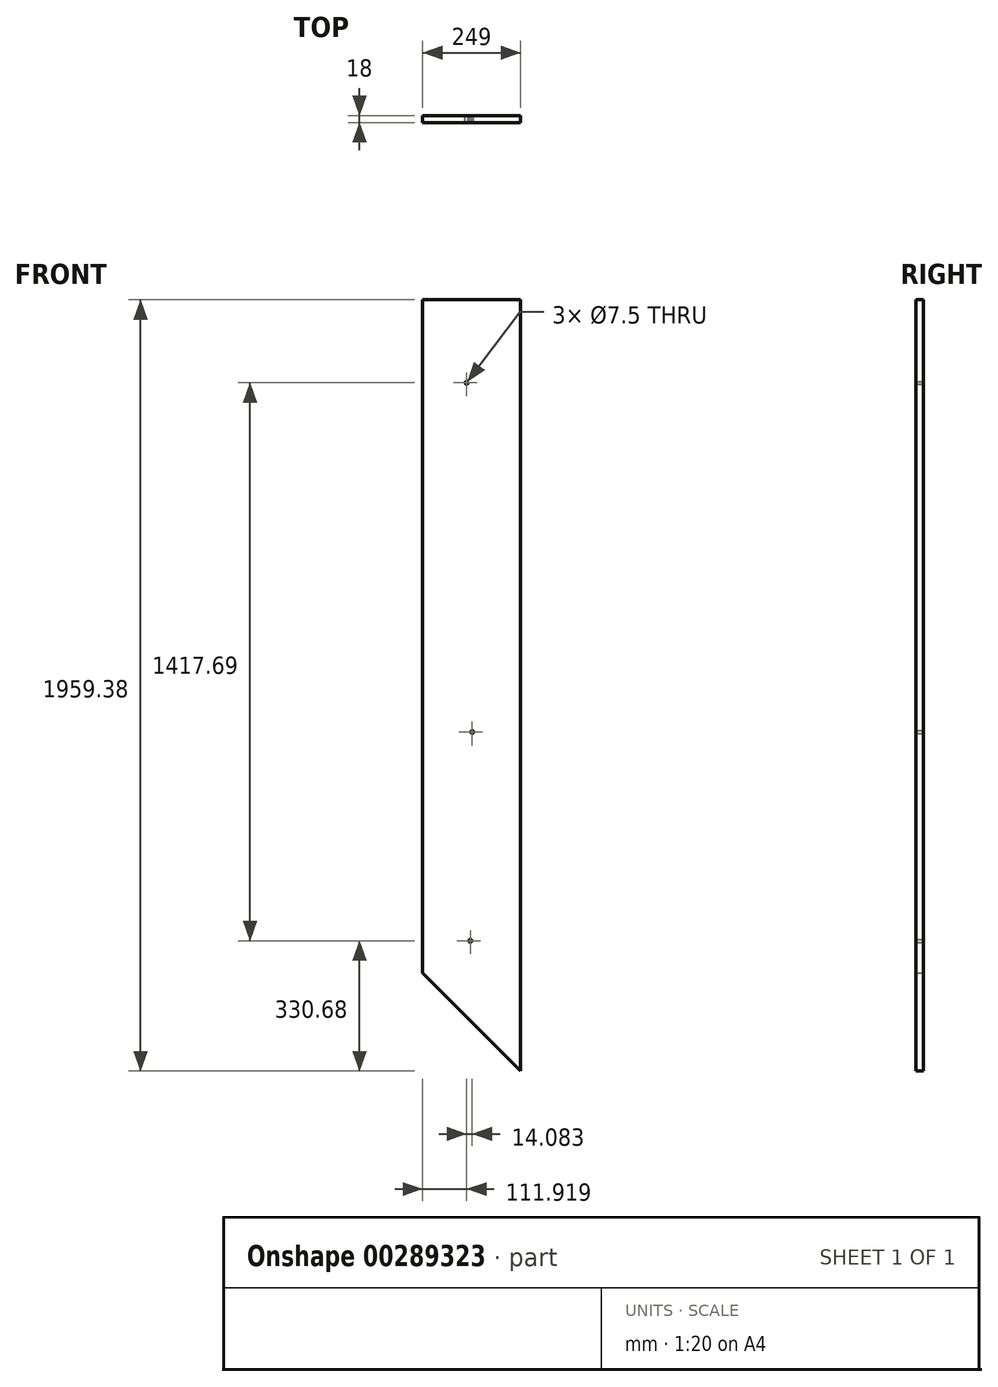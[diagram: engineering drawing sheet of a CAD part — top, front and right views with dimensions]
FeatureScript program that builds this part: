
annotation { "Feature Type Name" : "Feature", "Feature Type Description" : "" }
export const myFeature = defineFeature(function(context is Context, id is Id, definition is map)
    precondition{}
    {
        {
            var Q0;
            Q0=qCreatedBy(makeId("Front.planeOp"),FACE);
            var sketch = newSketch(context, id + "F0", { "sketchPlane" : qUnion([Q0])});
            skLineSegment(sketch, "E0", {"start": v(-600, -1200) * mm, "end": v(600, -1200) * mm});
            skLineSegment(sketch, "E1", {"start": v(600, -1200) * mm, "end": v(600, 1200) * mm});
            skLineSegment(sketch, "E2", {"start": v(600, 1200) * mm, "end": v(-600, 1200) * mm});
            skLineSegment(sketch, "E3", {"start": v(-600, 1200) * mm, "end": v(-600, -1200) * mm});
            skLineSegment(sketch, "E4", {"start": v(-283.65, 1167.87) * mm, "end": v(-532.65, 1167.87) * mm});
            skLineSegment(sketch, "E5", {"start": v(-532.65, 1167.87) * mm, "end": v(-532.65, -542.5) * mm});
            skLineSegment(sketch, "E6", {"start": v(-532.65, -542.5) * mm, "end": v(-283.65, -791.5) * mm});
            skLineSegment(sketch, "E7", {"start": v(-283.65, -791.5) * mm, "end": v(-283.65, 1167.87) * mm});
            skLineSegment(sketch, "E8", {"start": v(276.35, 1167.87) * mm, "end": v(27.35, 1167.87) * mm});
            skLineSegment(sketch, "E9", {"start": v(27.35, 1167.87) * mm, "end": v(27.35, -791.5) * mm});
            skLineSegment(sketch, "E10", {"start": v(27.35, -791.5) * mm, "end": v(276.35, -542.5) * mm});
            skLineSegment(sketch, "E11", {"start": v(276.35, -542.5) * mm, "end": v(276.35, 1167.87) * mm});
            skLineSegment(sketch, "E12", {"start": v(-3.65, 1167.87) * mm, "end": v(-252.65, 1167.87) * mm});
            skLineSegment(sketch, "E13", {"start": v(-252.65, 1167.87) * mm, "end": v(-252.65, -791.5) * mm});
            skLineSegment(sketch, "E14", {"start": v(-252.65, -791.5) * mm, "end": v(-3.65, -542.5) * mm});
            skLineSegment(sketch, "E15", {"start": v(-3.65, -542.5) * mm, "end": v(-3.65, 1167.87) * mm});
            skLineSegment(sketch, "E16", {"start": v(556.35, 1167.87) * mm, "end": v(307.35, 1167.87) * mm});
            skLineSegment(sketch, "E17", {"start": v(307.35, 1167.87) * mm, "end": v(307.35, -542.5) * mm});
            skLineSegment(sketch, "E18", {"start": v(307.35, -542.5) * mm, "end": v(556.35, -791.5) * mm});
            skLineSegment(sketch, "E19", {"start": v(556.35, -791.5) * mm, "end": v(556.35, 1167.87) * mm});
            skLineSegment(sketch, "E20", {"start": v(454.53, 163.58) * mm, "end": v(414.54, 163.58) * mm});
            skLineSegment(sketch, "E21", {"start": v(414.54, 163.58) * mm, "end": v(414.54, 188.44) * mm});
            skLineSegment(sketch, "E22", {"start": v(433.65, 163.58) * mm, "end": v(433.65, 186.65) * mm});
            skLineSegment(sketch, "E23", {"start": v(454.5, 220.74) * mm, "end": v(454.5, 197.24) * mm});
            skLineSegment(sketch, "E24", {"start": v(454.5, 197.24) * mm, "end": v(414.55, 197.24) * mm});
            skLineSegment(sketch, "E25", {"start": v(455.07, 235.9) * mm, "end": v(455.07, 235.48) * mm});
            skLineSegment(sketch, "E26", {"start": v(455.07, 235.48) * mm, "end": v(455.06, 235.06) * mm});
            skLineSegment(sketch, "E27", {"start": v(455.06, 235.06) * mm, "end": v(455.04, 234.64) * mm});
            skLineSegment(sketch, "E28", {"start": v(455.04, 234.64) * mm, "end": v(455.02, 234.22) * mm});
            skLineSegment(sketch, "E29", {"start": v(455.02, 234.22) * mm, "end": v(454.98, 233.8) * mm});
            skLineSegment(sketch, "E30", {"start": v(454.98, 233.8) * mm, "end": v(454.93, 233.4) * mm});
            skLineSegment(sketch, "E31", {"start": v(454.93, 233.4) * mm, "end": v(454.87, 232.98) * mm});
            skLineSegment(sketch, "E32", {"start": v(454.87, 232.98) * mm, "end": v(454.8, 232.58) * mm});
            skLineSegment(sketch, "E33", {"start": v(454.8, 232.58) * mm, "end": v(454.72, 232.17) * mm});
            skLineSegment(sketch, "E34", {"start": v(454.72, 232.17) * mm, "end": v(454.63, 231.76) * mm});
            skLineSegment(sketch, "E35", {"start": v(454.63, 231.76) * mm, "end": v(454.53, 231.36) * mm});
            skLineSegment(sketch, "E36", {"start": v(454.53, 231.36) * mm, "end": v(454.42, 230.96) * mm});
            skLineSegment(sketch, "E37", {"start": v(454.42, 230.96) * mm, "end": v(454.3, 230.56) * mm});
            skLineSegment(sketch, "E38", {"start": v(454.3, 230.56) * mm, "end": v(454.17, 230.17) * mm});
            skLineSegment(sketch, "E39", {"start": v(454.17, 230.17) * mm, "end": v(454.03, 229.78) * mm});
            skLineSegment(sketch, "E40", {"start": v(454.03, 229.78) * mm, "end": v(453.89, 229.4) * mm});
            skLineSegment(sketch, "E41", {"start": v(453.89, 229.4) * mm, "end": v(453.73, 229.01) * mm});
            skLineSegment(sketch, "E42", {"start": v(453.73, 229.01) * mm, "end": v(453.56, 228.64) * mm});
            skLineSegment(sketch, "E43", {"start": v(453.56, 228.64) * mm, "end": v(453.38, 228.26) * mm});
            skLineSegment(sketch, "E44", {"start": v(453.38, 228.26) * mm, "end": v(453.2, 227.9) * mm});
            skLineSegment(sketch, "E45", {"start": v(453.2, 227.9) * mm, "end": v(453, 227.53) * mm});
            skLineSegment(sketch, "E46", {"start": v(453, 227.53) * mm, "end": v(452.8, 227.17) * mm});
            skLineSegment(sketch, "E47", {"start": v(452.8, 227.17) * mm, "end": v(452.58, 226.8) * mm});
            skLineSegment(sketch, "E48", {"start": v(452.58, 226.8) * mm, "end": v(452.36, 226.46) * mm});
            skLineSegment(sketch, "E49", {"start": v(452.36, 226.46) * mm, "end": v(452.13, 226.11) * mm});
            skLineSegment(sketch, "E50", {"start": v(452.13, 226.11) * mm, "end": v(451.9, 225.77) * mm});
            skLineSegment(sketch, "E51", {"start": v(451.9, 225.77) * mm, "end": v(451.64, 225.44) * mm});
            skLineSegment(sketch, "E52", {"start": v(451.64, 225.44) * mm, "end": v(451.39, 225.11) * mm});
            skLineSegment(sketch, "E53", {"start": v(451.39, 225.11) * mm, "end": v(451.12, 224.8) * mm});
            skLineSegment(sketch, "E54", {"start": v(451.12, 224.8) * mm, "end": v(450.85, 224.47) * mm});
            skLineSegment(sketch, "E55", {"start": v(450.85, 224.47) * mm, "end": v(450.56, 224.17) * mm});
            skLineSegment(sketch, "E56", {"start": v(450.56, 224.17) * mm, "end": v(450.27, 223.86) * mm});
            skLineSegment(sketch, "E57", {"start": v(450.27, 223.86) * mm, "end": v(449.9, 223.51) * mm});
            skLineSegment(sketch, "E58", {"start": v(449.9, 223.51) * mm, "end": v(449.5, 223.17) * mm});
            skLineSegment(sketch, "E59", {"start": v(449.5, 223.17) * mm, "end": v(449.1, 222.85) * mm});
            skLineSegment(sketch, "E60", {"start": v(449.1, 222.85) * mm, "end": v(448.7, 222.53) * mm});
            skLineSegment(sketch, "E61", {"start": v(448.7, 222.53) * mm, "end": v(448.3, 222.22) * mm});
            skLineSegment(sketch, "E62", {"start": v(448.3, 222.22) * mm, "end": v(447.88, 221.92) * mm});
            skLineSegment(sketch, "E63", {"start": v(447.88, 221.92) * mm, "end": v(447.45, 221.63) * mm});
            skLineSegment(sketch, "E64", {"start": v(447.45, 221.63) * mm, "end": v(447.02, 221.36) * mm});
            skLineSegment(sketch, "E65", {"start": v(447.02, 221.36) * mm, "end": v(446.58, 221.1) * mm});
            skLineSegment(sketch, "E66", {"start": v(446.58, 221.1) * mm, "end": v(446.14, 220.84) * mm});
            skLineSegment(sketch, "E67", {"start": v(446.14, 220.84) * mm, "end": v(445.7, 220.6) * mm});
            skLineSegment(sketch, "E68", {"start": v(445.7, 220.6) * mm, "end": v(445.24, 220.37) * mm});
            skLineSegment(sketch, "E69", {"start": v(445.24, 220.37) * mm, "end": v(444.78, 220.15) * mm});
            skLineSegment(sketch, "E70", {"start": v(444.78, 220.15) * mm, "end": v(444.31, 219.94) * mm});
            skLineSegment(sketch, "E71", {"start": v(444.31, 219.94) * mm, "end": v(443.84, 219.74) * mm});
            skLineSegment(sketch, "E72", {"start": v(443.84, 219.74) * mm, "end": v(443.37, 219.56) * mm});
            skLineSegment(sketch, "E73", {"start": v(443.37, 219.56) * mm, "end": v(442.89, 219.38) * mm});
            skLineSegment(sketch, "E74", {"start": v(442.89, 219.38) * mm, "end": v(442.4, 219.22) * mm});
            skLineSegment(sketch, "E75", {"start": v(442.4, 219.22) * mm, "end": v(441.92, 219.07) * mm});
            skLineSegment(sketch, "E76", {"start": v(441.92, 219.07) * mm, "end": v(441.43, 218.93) * mm});
            skLineSegment(sketch, "E77", {"start": v(441.43, 218.93) * mm, "end": v(440.94, 218.8) * mm});
            skLineSegment(sketch, "E78", {"start": v(440.94, 218.8) * mm, "end": v(440.44, 218.7) * mm});
            skLineSegment(sketch, "E79", {"start": v(440.44, 218.7) * mm, "end": v(439.94, 218.59) * mm});
            skLineSegment(sketch, "E80", {"start": v(439.94, 218.59) * mm, "end": v(439.44, 218.5) * mm});
            skLineSegment(sketch, "E81", {"start": v(439.44, 218.5) * mm, "end": v(438.93, 218.42) * mm});
            skLineSegment(sketch, "E82", {"start": v(438.93, 218.42) * mm, "end": v(438.42, 218.36) * mm});
            skLineSegment(sketch, "E83", {"start": v(438.42, 218.36) * mm, "end": v(437.91, 218.3) * mm});
            skLineSegment(sketch, "E84", {"start": v(437.91, 218.3) * mm, "end": v(437.4, 218.27) * mm});
            skLineSegment(sketch, "E85", {"start": v(437.4, 218.27) * mm, "end": v(436.89, 218.24) * mm});
            skLineSegment(sketch, "E86", {"start": v(436.89, 218.24) * mm, "end": v(436.37, 218.23) * mm});
            skLineSegment(sketch, "E87", {"start": v(436.37, 218.23) * mm, "end": v(435.86, 218.22) * mm});
            skLineSegment(sketch, "E88", {"start": v(435.86, 218.22) * mm, "end": v(435.34, 218.24) * mm});
            skLineSegment(sketch, "E89", {"start": v(435.34, 218.24) * mm, "end": v(434.78, 218.22) * mm});
            skLineSegment(sketch, "E90", {"start": v(434.78, 218.22) * mm, "end": v(434.22, 218.22) * mm});
            skLineSegment(sketch, "E91", {"start": v(434.22, 218.22) * mm, "end": v(433.66, 218.23) * mm});
            skLineSegment(sketch, "E92", {"start": v(433.66, 218.23) * mm, "end": v(433.1, 218.26) * mm});
            skLineSegment(sketch, "E93", {"start": v(433.1, 218.26) * mm, "end": v(432.55, 218.3) * mm});
            skLineSegment(sketch, "E94", {"start": v(432.55, 218.3) * mm, "end": v(432, 218.35) * mm});
            skLineSegment(sketch, "E95", {"start": v(432, 218.35) * mm, "end": v(431.44, 218.42) * mm});
            skLineSegment(sketch, "E96", {"start": v(431.44, 218.42) * mm, "end": v(430.9, 218.5) * mm});
            skLineSegment(sketch, "E97", {"start": v(430.9, 218.5) * mm, "end": v(430.35, 218.6) * mm});
            skLineSegment(sketch, "E98", {"start": v(430.35, 218.6) * mm, "end": v(429.8, 218.7) * mm});
            skLineSegment(sketch, "E99", {"start": v(429.8, 218.7) * mm, "end": v(429.26, 218.83) * mm});
            skLineSegment(sketch, "E100", {"start": v(429.26, 218.83) * mm, "end": v(428.73, 218.97) * mm});
            skLineSegment(sketch, "E101", {"start": v(428.73, 218.97) * mm, "end": v(428.2, 219.11) * mm});
            skLineSegment(sketch, "E102", {"start": v(428.2, 219.11) * mm, "end": v(427.66, 219.28) * mm});
            skLineSegment(sketch, "E103", {"start": v(427.66, 219.28) * mm, "end": v(427.14, 219.45) * mm});
            skLineSegment(sketch, "E104", {"start": v(427.14, 219.45) * mm, "end": v(426.62, 219.64) * mm});
            skLineSegment(sketch, "E105", {"start": v(426.62, 219.64) * mm, "end": v(426.1, 219.84) * mm});
            skLineSegment(sketch, "E106", {"start": v(426.1, 219.84) * mm, "end": v(425.6, 220.05) * mm});
            skLineSegment(sketch, "E107", {"start": v(425.6, 220.05) * mm, "end": v(425.09, 220.28) * mm});
            skLineSegment(sketch, "E108", {"start": v(425.09, 220.28) * mm, "end": v(424.6, 220.52) * mm});
            skLineSegment(sketch, "E109", {"start": v(424.6, 220.52) * mm, "end": v(424.1, 220.77) * mm});
            skLineSegment(sketch, "E110", {"start": v(424.1, 220.77) * mm, "end": v(423.6, 221.03) * mm});
            skLineSegment(sketch, "E111", {"start": v(423.6, 221.03) * mm, "end": v(423.13, 221.31) * mm});
            skLineSegment(sketch, "E112", {"start": v(423.13, 221.31) * mm, "end": v(422.65, 221.6) * mm});
            skLineSegment(sketch, "E113", {"start": v(422.65, 221.6) * mm, "end": v(422.19, 221.9) * mm});
            skLineSegment(sketch, "E114", {"start": v(422.19, 221.9) * mm, "end": v(421.73, 222.21) * mm});
            skLineSegment(sketch, "E115", {"start": v(421.73, 222.21) * mm, "end": v(421.27, 222.53) * mm});
            skLineSegment(sketch, "E116", {"start": v(421.27, 222.53) * mm, "end": v(420.83, 222.87) * mm});
            skLineSegment(sketch, "E117", {"start": v(420.83, 222.87) * mm, "end": v(420.4, 223.22) * mm});
            skLineSegment(sketch, "E118", {"start": v(420.4, 223.22) * mm, "end": v(419.96, 223.58) * mm});
            skLineSegment(sketch, "E119", {"start": v(419.96, 223.58) * mm, "end": v(419.54, 223.95) * mm});
            skLineSegment(sketch, "E120", {"start": v(419.54, 223.95) * mm, "end": v(419.13, 224.33) * mm});
            skLineSegment(sketch, "E121", {"start": v(419.13, 224.33) * mm, "end": v(418.84, 224.61) * mm});
            skLineSegment(sketch, "E122", {"start": v(418.84, 224.61) * mm, "end": v(418.56, 224.9) * mm});
            skLineSegment(sketch, "E123", {"start": v(418.56, 224.9) * mm, "end": v(418.28, 225.2) * mm});
            skLineSegment(sketch, "E124", {"start": v(418.28, 225.2) * mm, "end": v(418.02, 225.51) * mm});
            skLineSegment(sketch, "E125", {"start": v(418.02, 225.51) * mm, "end": v(417.76, 225.82) * mm});
            skLineSegment(sketch, "E126", {"start": v(417.76, 225.82) * mm, "end": v(417.51, 226.14) * mm});
            skLineSegment(sketch, "E127", {"start": v(417.51, 226.14) * mm, "end": v(417.27, 226.47) * mm});
            skLineSegment(sketch, "E128", {"start": v(417.27, 226.47) * mm, "end": v(417.04, 226.8) * mm});
            skLineSegment(sketch, "E129", {"start": v(417.04, 226.8) * mm, "end": v(416.82, 227.13) * mm});
            skLineSegment(sketch, "E130", {"start": v(416.82, 227.13) * mm, "end": v(416.6, 227.47) * mm});
            skLineSegment(sketch, "E131", {"start": v(416.6, 227.47) * mm, "end": v(416.4, 227.82) * mm});
            skLineSegment(sketch, "E132", {"start": v(416.4, 227.82) * mm, "end": v(416.2, 228.17) * mm});
            skLineSegment(sketch, "E133", {"start": v(416.2, 228.17) * mm, "end": v(416.02, 228.52) * mm});
            skLineSegment(sketch, "E134", {"start": v(416.02, 228.52) * mm, "end": v(415.84, 228.88) * mm});
            skLineSegment(sketch, "E135", {"start": v(415.84, 228.88) * mm, "end": v(415.67, 229.25) * mm});
            skLineSegment(sketch, "E136", {"start": v(415.67, 229.25) * mm, "end": v(415.51, 229.61) * mm});
            skLineSegment(sketch, "E137", {"start": v(415.51, 229.61) * mm, "end": v(415.36, 229.99) * mm});
            skLineSegment(sketch, "E138", {"start": v(415.36, 229.99) * mm, "end": v(415.22, 230.36) * mm});
            skLineSegment(sketch, "E139", {"start": v(415.22, 230.36) * mm, "end": v(415.1, 230.74) * mm});
            skLineSegment(sketch, "E140", {"start": v(415.1, 230.74) * mm, "end": v(414.97, 231.12) * mm});
            skLineSegment(sketch, "E141", {"start": v(414.97, 231.12) * mm, "end": v(414.86, 231.5) * mm});
            skLineSegment(sketch, "E142", {"start": v(414.86, 231.5) * mm, "end": v(414.76, 231.9) * mm});
            skLineSegment(sketch, "E143", {"start": v(414.76, 231.9) * mm, "end": v(414.67, 232.3) * mm});
            skLineSegment(sketch, "E144", {"start": v(414.67, 232.3) * mm, "end": v(414.59, 232.68) * mm});
            skLineSegment(sketch, "E145", {"start": v(414.59, 232.68) * mm, "end": v(414.51, 233.08) * mm});
            skLineSegment(sketch, "E146", {"start": v(414.51, 233.08) * mm, "end": v(414.45, 233.48) * mm});
            skLineSegment(sketch, "E147", {"start": v(414.45, 233.48) * mm, "end": v(414.4, 233.88) * mm});
            skLineSegment(sketch, "E148", {"start": v(414.4, 233.88) * mm, "end": v(414.36, 234.28) * mm});
            skLineSegment(sketch, "E149", {"start": v(414.36, 234.28) * mm, "end": v(414.33, 234.69) * mm});
            skLineSegment(sketch, "E150", {"start": v(414.33, 234.69) * mm, "end": v(414.31, 235.1) * mm});
            skLineSegment(sketch, "E151", {"start": v(414.31, 235.1) * mm, "end": v(414.3, 235.5) * mm});
            skLineSegment(sketch, "E152", {"start": v(414.3, 235.5) * mm, "end": v(414.3, 235.9) * mm});
            skLineSegment(sketch, "E153", {"start": v(414.3, 235.9) * mm, "end": v(414.3, 236.32) * mm});
            skLineSegment(sketch, "E154", {"start": v(414.3, 236.32) * mm, "end": v(414.32, 236.73) * mm});
            skLineSegment(sketch, "E155", {"start": v(414.32, 236.73) * mm, "end": v(414.35, 237.15) * mm});
            skLineSegment(sketch, "E156", {"start": v(414.35, 237.15) * mm, "end": v(414.38, 237.56) * mm});
            skLineSegment(sketch, "E157", {"start": v(414.38, 237.56) * mm, "end": v(414.43, 237.96) * mm});
            skLineSegment(sketch, "E158", {"start": v(414.43, 237.96) * mm, "end": v(414.49, 238.37) * mm});
            skLineSegment(sketch, "E159", {"start": v(414.49, 238.37) * mm, "end": v(414.55, 238.78) * mm});
            skLineSegment(sketch, "E160", {"start": v(414.55, 238.78) * mm, "end": v(414.63, 239.18) * mm});
            skLineSegment(sketch, "E161", {"start": v(414.63, 239.18) * mm, "end": v(414.72, 239.58) * mm});
            skLineSegment(sketch, "E162", {"start": v(414.72, 239.58) * mm, "end": v(414.82, 239.97) * mm});
            skLineSegment(sketch, "E163", {"start": v(414.82, 239.97) * mm, "end": v(414.93, 240.37) * mm});
            skLineSegment(sketch, "E164", {"start": v(414.93, 240.37) * mm, "end": v(415.04, 240.76) * mm});
            skLineSegment(sketch, "E165", {"start": v(415.04, 240.76) * mm, "end": v(415.17, 241.15) * mm});
            skLineSegment(sketch, "E166", {"start": v(415.17, 241.15) * mm, "end": v(415.3, 241.53) * mm});
            skLineSegment(sketch, "E167", {"start": v(415.3, 241.53) * mm, "end": v(415.46, 241.91) * mm});
            skLineSegment(sketch, "E168", {"start": v(415.46, 241.91) * mm, "end": v(415.61, 242.29) * mm});
            skLineSegment(sketch, "E169", {"start": v(415.61, 242.29) * mm, "end": v(415.78, 242.66) * mm});
            skLineSegment(sketch, "E170", {"start": v(415.78, 242.66) * mm, "end": v(415.95, 243.03) * mm});
            skLineSegment(sketch, "E171", {"start": v(415.95, 243.03) * mm, "end": v(416.14, 243.4) * mm});
            skLineSegment(sketch, "E172", {"start": v(416.14, 243.4) * mm, "end": v(416.33, 243.75) * mm});
            skLineSegment(sketch, "E173", {"start": v(416.33, 243.75) * mm, "end": v(416.54, 244.1) * mm});
            skLineSegment(sketch, "E174", {"start": v(416.54, 244.1) * mm, "end": v(416.75, 244.45) * mm});
            skLineSegment(sketch, "E175", {"start": v(416.75, 244.45) * mm, "end": v(416.97, 244.8) * mm});
            skLineSegment(sketch, "E176", {"start": v(416.97, 244.8) * mm, "end": v(417.2, 245.13) * mm});
            skLineSegment(sketch, "E177", {"start": v(417.2, 245.13) * mm, "end": v(417.44, 245.47) * mm});
            skLineSegment(sketch, "E178", {"start": v(417.44, 245.47) * mm, "end": v(417.69, 245.8) * mm});
            skLineSegment(sketch, "E179", {"start": v(417.69, 245.8) * mm, "end": v(417.94, 246.11) * mm});
            skLineSegment(sketch, "E180", {"start": v(417.94, 246.11) * mm, "end": v(418.21, 246.43) * mm});
            skLineSegment(sketch, "E181", {"start": v(418.21, 246.43) * mm, "end": v(418.48, 246.73) * mm});
            skLineSegment(sketch, "E182", {"start": v(418.48, 246.73) * mm, "end": v(418.77, 247.03) * mm});
            skLineSegment(sketch, "E183", {"start": v(418.77, 247.03) * mm, "end": v(419.06, 247.33) * mm});
            skLineSegment(sketch, "E184", {"start": v(419.06, 247.33) * mm, "end": v(419.36, 247.62) * mm});
            skLineSegment(sketch, "E185", {"start": v(419.36, 247.62) * mm, "end": v(419.77, 247.99) * mm});
            skLineSegment(sketch, "E186", {"start": v(419.77, 247.99) * mm, "end": v(420.18, 248.34) * mm});
            skLineSegment(sketch, "E187", {"start": v(420.18, 248.34) * mm, "end": v(420.6, 248.7) * mm});
            skLineSegment(sketch, "E188", {"start": v(420.6, 248.7) * mm, "end": v(421.04, 249.03) * mm});
            skLineSegment(sketch, "E189", {"start": v(421.04, 249.03) * mm, "end": v(421.49, 249.35) * mm});
            skLineSegment(sketch, "E190", {"start": v(421.49, 249.35) * mm, "end": v(421.93, 249.67) * mm});
            skLineSegment(sketch, "E191", {"start": v(421.93, 249.67) * mm, "end": v(422.39, 249.97) * mm});
            skLineSegment(sketch, "E192", {"start": v(422.39, 249.97) * mm, "end": v(422.85, 250.26) * mm});
            skLineSegment(sketch, "E193", {"start": v(422.85, 250.26) * mm, "end": v(423.32, 250.54) * mm});
            skLineSegment(sketch, "E194", {"start": v(423.32, 250.54) * mm, "end": v(423.8, 250.8) * mm});
            skLineSegment(sketch, "E195", {"start": v(423.8, 250.8) * mm, "end": v(424.28, 251.06) * mm});
            skLineSegment(sketch, "E196", {"start": v(424.28, 251.06) * mm, "end": v(424.77, 251.3) * mm});
            skLineSegment(sketch, "E197", {"start": v(424.77, 251.3) * mm, "end": v(425.26, 251.53) * mm});
            skLineSegment(sketch, "E198", {"start": v(425.26, 251.53) * mm, "end": v(425.76, 251.75) * mm});
            skLineSegment(sketch, "E199", {"start": v(425.76, 251.75) * mm, "end": v(426.26, 251.95) * mm});
            skLineSegment(sketch, "E200", {"start": v(426.26, 251.95) * mm, "end": v(426.77, 252.14) * mm});
            skLineSegment(sketch, "E201", {"start": v(426.77, 252.14) * mm, "end": v(427.29, 252.32) * mm});
            skLineSegment(sketch, "E202", {"start": v(427.29, 252.32) * mm, "end": v(427.8, 252.5) * mm});
            skLineSegment(sketch, "E203", {"start": v(427.8, 252.5) * mm, "end": v(428.33, 252.64) * mm});
            skLineSegment(sketch, "E204", {"start": v(428.33, 252.64) * mm, "end": v(428.85, 252.79) * mm});
            skLineSegment(sketch, "E205", {"start": v(428.85, 252.79) * mm, "end": v(429.38, 252.91) * mm});
            skLineSegment(sketch, "E206", {"start": v(429.38, 252.91) * mm, "end": v(429.91, 253.03) * mm});
            skLineSegment(sketch, "E207", {"start": v(429.91, 253.03) * mm, "end": v(430.45, 253.13) * mm});
            skLineSegment(sketch, "E208", {"start": v(430.45, 253.13) * mm, "end": v(430.99, 253.22) * mm});
            skLineSegment(sketch, "E209", {"start": v(430.99, 253.22) * mm, "end": v(431.53, 253.3) * mm});
            skLineSegment(sketch, "E210", {"start": v(431.53, 253.3) * mm, "end": v(432.07, 253.36) * mm});
            skLineSegment(sketch, "E211", {"start": v(432.07, 253.36) * mm, "end": v(432.62, 253.41) * mm});
            skLineSegment(sketch, "E212", {"start": v(432.62, 253.41) * mm, "end": v(433.16, 253.45) * mm});
            skLineSegment(sketch, "E213", {"start": v(433.16, 253.45) * mm, "end": v(433.71, 253.47) * mm});
            skLineSegment(sketch, "E214", {"start": v(433.71, 253.47) * mm, "end": v(434.26, 253.48) * mm});
            skLineSegment(sketch, "E215", {"start": v(434.26, 253.48) * mm, "end": v(434.81, 253.47) * mm});
            skLineSegment(sketch, "E216", {"start": v(434.81, 253.47) * mm, "end": v(435.36, 253.45) * mm});
            skLineSegment(sketch, "E217", {"start": v(435.36, 253.45) * mm, "end": v(435.88, 253.46) * mm});
            skLineSegment(sketch, "E218", {"start": v(435.88, 253.46) * mm, "end": v(436.4, 253.45) * mm});
            skLineSegment(sketch, "E219", {"start": v(436.4, 253.45) * mm, "end": v(436.9, 253.44) * mm});
            skLineSegment(sketch, "E220", {"start": v(436.9, 253.44) * mm, "end": v(437.42, 253.4) * mm});
            skLineSegment(sketch, "E221", {"start": v(437.42, 253.4) * mm, "end": v(437.93, 253.36) * mm});
            skLineSegment(sketch, "E222", {"start": v(437.93, 253.36) * mm, "end": v(438.43, 253.3) * mm});
            skLineSegment(sketch, "E223", {"start": v(438.43, 253.3) * mm, "end": v(438.94, 253.24) * mm});
            skLineSegment(sketch, "E224", {"start": v(438.94, 253.24) * mm, "end": v(439.44, 253.16) * mm});
            skLineSegment(sketch, "E225", {"start": v(439.44, 253.16) * mm, "end": v(439.94, 253.06) * mm});
            skLineSegment(sketch, "E226", {"start": v(439.94, 253.06) * mm, "end": v(440.44, 252.96) * mm});
            skLineSegment(sketch, "E227", {"start": v(440.44, 252.96) * mm, "end": v(440.93, 252.84) * mm});
            skLineSegment(sketch, "E228", {"start": v(440.93, 252.84) * mm, "end": v(441.42, 252.7) * mm});
            skLineSegment(sketch, "E229", {"start": v(441.42, 252.7) * mm, "end": v(441.91, 252.57) * mm});
            skLineSegment(sketch, "E230", {"start": v(441.91, 252.57) * mm, "end": v(442.4, 252.41) * mm});
            skLineSegment(sketch, "E231", {"start": v(442.4, 252.41) * mm, "end": v(442.87, 252.24) * mm});
            skLineSegment(sketch, "E232", {"start": v(442.87, 252.24) * mm, "end": v(443.35, 252.07) * mm});
            skLineSegment(sketch, "E233", {"start": v(443.35, 252.07) * mm, "end": v(443.82, 251.88) * mm});
            skLineSegment(sketch, "E234", {"start": v(443.82, 251.88) * mm, "end": v(444.28, 251.68) * mm});
            skLineSegment(sketch, "E235", {"start": v(444.28, 251.68) * mm, "end": v(444.74, 251.46) * mm});
            skLineSegment(sketch, "E236", {"start": v(444.74, 251.46) * mm, "end": v(445.2, 251.24) * mm});
            skLineSegment(sketch, "E237", {"start": v(445.2, 251.24) * mm, "end": v(445.65, 251) * mm});
            skLineSegment(sketch, "E238", {"start": v(445.65, 251) * mm, "end": v(446.1, 250.76) * mm});
            skLineSegment(sketch, "E239", {"start": v(446.1, 250.76) * mm, "end": v(446.53, 250.5) * mm});
            skLineSegment(sketch, "E240", {"start": v(446.53, 250.5) * mm, "end": v(446.96, 250.23) * mm});
            skLineSegment(sketch, "E241", {"start": v(446.96, 250.23) * mm, "end": v(447.39, 249.95) * mm});
            skLineSegment(sketch, "E242", {"start": v(447.39, 249.95) * mm, "end": v(447.8, 249.66) * mm});
            skLineSegment(sketch, "E243", {"start": v(447.8, 249.66) * mm, "end": v(448.22, 249.36) * mm});
            skLineSegment(sketch, "E244", {"start": v(448.22, 249.36) * mm, "end": v(448.62, 249.04) * mm});
            skLineSegment(sketch, "E245", {"start": v(448.62, 249.04) * mm, "end": v(449.02, 248.72) * mm});
            skLineSegment(sketch, "E246", {"start": v(449.02, 248.72) * mm, "end": v(449.41, 248.39) * mm});
            skLineSegment(sketch, "E247", {"start": v(449.41, 248.39) * mm, "end": v(449.8, 248.04) * mm});
            skLineSegment(sketch, "E248", {"start": v(449.8, 248.04) * mm, "end": v(450.17, 247.69) * mm});
            skLineSegment(sketch, "E249", {"start": v(450.17, 247.69) * mm, "end": v(450.46, 247.4) * mm});
            skLineSegment(sketch, "E250", {"start": v(450.46, 247.4) * mm, "end": v(450.74, 247.1) * mm});
            skLineSegment(sketch, "E251", {"start": v(450.74, 247.1) * mm, "end": v(451.02, 246.79) * mm});
            skLineSegment(sketch, "E252", {"start": v(451.02, 246.79) * mm, "end": v(451.28, 246.47) * mm});
            skLineSegment(sketch, "E253", {"start": v(451.28, 246.47) * mm, "end": v(451.54, 246.15) * mm});
            skLineSegment(sketch, "E254", {"start": v(451.54, 246.15) * mm, "end": v(451.8, 245.83) * mm});
            skLineSegment(sketch, "E255", {"start": v(451.8, 245.83) * mm, "end": v(452.03, 245.5) * mm});
            skLineSegment(sketch, "E256", {"start": v(452.03, 245.5) * mm, "end": v(452.26, 245.16) * mm});
            skLineSegment(sketch, "E257", {"start": v(452.26, 245.16) * mm, "end": v(452.49, 244.82) * mm});
            skLineSegment(sketch, "E258", {"start": v(452.49, 244.82) * mm, "end": v(452.7, 244.47) * mm});
            skLineSegment(sketch, "E259", {"start": v(452.7, 244.47) * mm, "end": v(452.91, 244.12) * mm});
            skLineSegment(sketch, "E260", {"start": v(452.91, 244.12) * mm, "end": v(453.1, 243.76) * mm});
            skLineSegment(sketch, "E261", {"start": v(453.1, 243.76) * mm, "end": v(453.3, 243.4) * mm});
            skLineSegment(sketch, "E262", {"start": v(453.3, 243.4) * mm, "end": v(453.48, 243.03) * mm});
            skLineSegment(sketch, "E263", {"start": v(453.48, 243.03) * mm, "end": v(453.65, 242.66) * mm});
            skLineSegment(sketch, "E264", {"start": v(453.65, 242.66) * mm, "end": v(453.8, 242.29) * mm});
            skLineSegment(sketch, "E265", {"start": v(453.8, 242.29) * mm, "end": v(453.96, 241.9) * mm});
            skLineSegment(sketch, "E266", {"start": v(453.96, 241.9) * mm, "end": v(454.1, 241.53) * mm});
            skLineSegment(sketch, "E267", {"start": v(454.1, 241.53) * mm, "end": v(454.23, 241.14) * mm});
            skLineSegment(sketch, "E268", {"start": v(454.23, 241.14) * mm, "end": v(454.36, 240.75) * mm});
            skLineSegment(sketch, "E269", {"start": v(454.36, 240.75) * mm, "end": v(454.47, 240.36) * mm});
            skLineSegment(sketch, "E270", {"start": v(454.47, 240.36) * mm, "end": v(454.58, 239.97) * mm});
            skLineSegment(sketch, "E271", {"start": v(454.58, 239.97) * mm, "end": v(454.67, 239.57) * mm});
            skLineSegment(sketch, "E272", {"start": v(454.67, 239.57) * mm, "end": v(454.75, 239.17) * mm});
            skLineSegment(sketch, "E273", {"start": v(454.75, 239.17) * mm, "end": v(454.83, 238.77) * mm});
            skLineSegment(sketch, "E274", {"start": v(454.83, 238.77) * mm, "end": v(454.9, 238.36) * mm});
            skLineSegment(sketch, "E275", {"start": v(454.9, 238.36) * mm, "end": v(454.95, 237.95) * mm});
            skLineSegment(sketch, "E276", {"start": v(454.95, 237.95) * mm, "end": v(455, 237.55) * mm});
            skLineSegment(sketch, "E277", {"start": v(455, 237.55) * mm, "end": v(455.03, 237.14) * mm});
            skLineSegment(sketch, "E278", {"start": v(455.03, 237.14) * mm, "end": v(455.05, 236.72) * mm});
            skLineSegment(sketch, "E279", {"start": v(455.05, 236.72) * mm, "end": v(455.06, 236.31) * mm});
            skLineSegment(sketch, "E280", {"start": v(455.06, 236.31) * mm, "end": v(455.07, 235.9) * mm});
            skLineSegment(sketch, "E281", {"start": v(455.07, 280.14) * mm, "end": v(455.07, 279.72) * mm});
            skLineSegment(sketch, "E282", {"start": v(455.07, 279.72) * mm, "end": v(455.06, 279.3) * mm});
            skLineSegment(sketch, "E283", {"start": v(455.06, 279.3) * mm, "end": v(455.04, 278.89) * mm});
            skLineSegment(sketch, "E284", {"start": v(455.04, 278.89) * mm, "end": v(455.02, 278.47) * mm});
            skLineSegment(sketch, "E285", {"start": v(455.02, 278.47) * mm, "end": v(454.98, 278.06) * mm});
            skLineSegment(sketch, "E286", {"start": v(454.98, 278.06) * mm, "end": v(454.93, 277.64) * mm});
            skLineSegment(sketch, "E287", {"start": v(454.93, 277.64) * mm, "end": v(454.87, 277.23) * mm});
            skLineSegment(sketch, "E288", {"start": v(454.87, 277.23) * mm, "end": v(454.8, 276.82) * mm});
            skLineSegment(sketch, "E289", {"start": v(454.8, 276.82) * mm, "end": v(454.72, 276.41) * mm});
            skLineSegment(sketch, "E290", {"start": v(454.72, 276.41) * mm, "end": v(454.63, 276) * mm});
            skLineSegment(sketch, "E291", {"start": v(454.63, 276) * mm, "end": v(454.53, 275.6) * mm});
            skLineSegment(sketch, "E292", {"start": v(454.53, 275.6) * mm, "end": v(454.42, 275.2) * mm});
            skLineSegment(sketch, "E293", {"start": v(454.42, 275.2) * mm, "end": v(454.3, 274.81) * mm});
            skLineSegment(sketch, "E294", {"start": v(454.3, 274.81) * mm, "end": v(454.17, 274.42) * mm});
            skLineSegment(sketch, "E295", {"start": v(454.17, 274.42) * mm, "end": v(454.03, 274.03) * mm});
            skLineSegment(sketch, "E296", {"start": v(454.03, 274.03) * mm, "end": v(453.89, 273.64) * mm});
            skLineSegment(sketch, "E297", {"start": v(453.89, 273.64) * mm, "end": v(453.73, 273.26) * mm});
            skLineSegment(sketch, "E298", {"start": v(453.73, 273.26) * mm, "end": v(453.56, 272.88) * mm});
            skLineSegment(sketch, "E299", {"start": v(453.56, 272.88) * mm, "end": v(453.38, 272.5) * mm});
            skLineSegment(sketch, "E300", {"start": v(453.38, 272.5) * mm, "end": v(453.2, 272.14) * mm});
            skLineSegment(sketch, "E301", {"start": v(453.2, 272.14) * mm, "end": v(453, 271.77) * mm});
            skLineSegment(sketch, "E302", {"start": v(453, 271.77) * mm, "end": v(452.8, 271.41) * mm});
            skLineSegment(sketch, "E303", {"start": v(452.8, 271.41) * mm, "end": v(452.58, 271.05) * mm});
            skLineSegment(sketch, "E304", {"start": v(452.58, 271.05) * mm, "end": v(452.36, 270.7) * mm});
            skLineSegment(sketch, "E305", {"start": v(452.36, 270.7) * mm, "end": v(452.13, 270.36) * mm});
            skLineSegment(sketch, "E306", {"start": v(452.13, 270.36) * mm, "end": v(451.9, 270.02) * mm});
            skLineSegment(sketch, "E307", {"start": v(451.9, 270.02) * mm, "end": v(451.64, 269.69) * mm});
            skLineSegment(sketch, "E308", {"start": v(451.64, 269.69) * mm, "end": v(451.39, 269.36) * mm});
            skLineSegment(sketch, "E309", {"start": v(451.39, 269.36) * mm, "end": v(451.12, 269.04) * mm});
            skLineSegment(sketch, "E310", {"start": v(451.12, 269.04) * mm, "end": v(450.85, 268.72) * mm});
            skLineSegment(sketch, "E311", {"start": v(450.85, 268.72) * mm, "end": v(450.56, 268.41) * mm});
            skLineSegment(sketch, "E312", {"start": v(450.56, 268.41) * mm, "end": v(450.27, 268.1) * mm});
            skLineSegment(sketch, "E313", {"start": v(450.27, 268.1) * mm, "end": v(449.9, 267.76) * mm});
            skLineSegment(sketch, "E314", {"start": v(449.9, 267.76) * mm, "end": v(449.5, 267.42) * mm});
            skLineSegment(sketch, "E315", {"start": v(449.5, 267.42) * mm, "end": v(449.1, 267.1) * mm});
            skLineSegment(sketch, "E316", {"start": v(449.1, 267.1) * mm, "end": v(448.7, 266.77) * mm});
            skLineSegment(sketch, "E317", {"start": v(448.7, 266.77) * mm, "end": v(448.3, 266.46) * mm});
            skLineSegment(sketch, "E318", {"start": v(448.3, 266.46) * mm, "end": v(447.88, 266.17) * mm});
            skLineSegment(sketch, "E319", {"start": v(447.88, 266.17) * mm, "end": v(447.45, 265.88) * mm});
            skLineSegment(sketch, "E320", {"start": v(447.45, 265.88) * mm, "end": v(447.02, 265.6) * mm});
            skLineSegment(sketch, "E321", {"start": v(447.02, 265.6) * mm, "end": v(446.58, 265.34) * mm});
            skLineSegment(sketch, "E322", {"start": v(446.58, 265.34) * mm, "end": v(446.14, 265.09) * mm});
            skLineSegment(sketch, "E323", {"start": v(446.14, 265.09) * mm, "end": v(445.7, 264.84) * mm});
            skLineSegment(sketch, "E324", {"start": v(445.7, 264.84) * mm, "end": v(445.24, 264.61) * mm});
            skLineSegment(sketch, "E325", {"start": v(445.24, 264.61) * mm, "end": v(444.78, 264.4) * mm});
            skLineSegment(sketch, "E326", {"start": v(444.78, 264.4) * mm, "end": v(444.31, 264.18) * mm});
            skLineSegment(sketch, "E327", {"start": v(444.31, 264.18) * mm, "end": v(443.84, 263.99) * mm});
            skLineSegment(sketch, "E328", {"start": v(443.84, 263.99) * mm, "end": v(443.37, 263.8) * mm});
            skLineSegment(sketch, "E329", {"start": v(443.37, 263.8) * mm, "end": v(442.89, 263.63) * mm});
            skLineSegment(sketch, "E330", {"start": v(442.89, 263.63) * mm, "end": v(442.4, 263.47) * mm});
            skLineSegment(sketch, "E331", {"start": v(442.4, 263.47) * mm, "end": v(441.92, 263.32) * mm});
            skLineSegment(sketch, "E332", {"start": v(441.92, 263.32) * mm, "end": v(441.43, 263.18) * mm});
            skLineSegment(sketch, "E333", {"start": v(441.43, 263.18) * mm, "end": v(440.94, 263.05) * mm});
            skLineSegment(sketch, "E334", {"start": v(440.94, 263.05) * mm, "end": v(440.44, 262.94) * mm});
            skLineSegment(sketch, "E335", {"start": v(440.44, 262.94) * mm, "end": v(439.94, 262.84) * mm});
            skLineSegment(sketch, "E336", {"start": v(439.94, 262.84) * mm, "end": v(439.44, 262.75) * mm});
            skLineSegment(sketch, "E337", {"start": v(439.44, 262.75) * mm, "end": v(438.93, 262.67) * mm});
            skLineSegment(sketch, "E338", {"start": v(438.93, 262.67) * mm, "end": v(438.42, 262.6) * mm});
            skLineSegment(sketch, "E339", {"start": v(438.42, 262.6) * mm, "end": v(437.91, 262.55) * mm});
            skLineSegment(sketch, "E340", {"start": v(437.91, 262.55) * mm, "end": v(437.4, 262.51) * mm});
            skLineSegment(sketch, "E341", {"start": v(437.4, 262.51) * mm, "end": v(436.89, 262.49) * mm});
            skLineSegment(sketch, "E342", {"start": v(436.89, 262.49) * mm, "end": v(436.37, 262.47) * mm});
            skLineSegment(sketch, "E343", {"start": v(436.37, 262.47) * mm, "end": v(435.86, 262.47) * mm});
            skLineSegment(sketch, "E344", {"start": v(435.86, 262.47) * mm, "end": v(435.34, 262.48) * mm});
            skLineSegment(sketch, "E345", {"start": v(435.34, 262.48) * mm, "end": v(434.78, 262.47) * mm});
            skLineSegment(sketch, "E346", {"start": v(434.78, 262.47) * mm, "end": v(434.22, 262.46) * mm});
            skLineSegment(sketch, "E347", {"start": v(434.22, 262.46) * mm, "end": v(433.66, 262.48) * mm});
            skLineSegment(sketch, "E348", {"start": v(433.66, 262.48) * mm, "end": v(433.1, 262.5) * mm});
            skLineSegment(sketch, "E349", {"start": v(433.1, 262.5) * mm, "end": v(432.55, 262.54) * mm});
            skLineSegment(sketch, "E350", {"start": v(432.55, 262.54) * mm, "end": v(432, 262.6) * mm});
            skLineSegment(sketch, "E351", {"start": v(432, 262.6) * mm, "end": v(431.44, 262.67) * mm});
            skLineSegment(sketch, "E352", {"start": v(431.44, 262.67) * mm, "end": v(430.9, 262.75) * mm});
            skLineSegment(sketch, "E353", {"start": v(430.9, 262.75) * mm, "end": v(430.35, 262.84) * mm});
            skLineSegment(sketch, "E354", {"start": v(430.35, 262.84) * mm, "end": v(429.8, 262.95) * mm});
            skLineSegment(sketch, "E355", {"start": v(429.8, 262.95) * mm, "end": v(429.26, 263.08) * mm});
            skLineSegment(sketch, "E356", {"start": v(429.26, 263.08) * mm, "end": v(428.73, 263.21) * mm});
            skLineSegment(sketch, "E357", {"start": v(428.73, 263.21) * mm, "end": v(428.2, 263.36) * mm});
            skLineSegment(sketch, "E358", {"start": v(428.2, 263.36) * mm, "end": v(427.66, 263.52) * mm});
            skLineSegment(sketch, "E359", {"start": v(427.66, 263.52) * mm, "end": v(427.14, 263.7) * mm});
            skLineSegment(sketch, "E360", {"start": v(427.14, 263.7) * mm, "end": v(426.62, 263.89) * mm});
            skLineSegment(sketch, "E361", {"start": v(426.62, 263.89) * mm, "end": v(426.1, 264.09) * mm});
            skLineSegment(sketch, "E362", {"start": v(426.1, 264.09) * mm, "end": v(425.6, 264.3) * mm});
            skLineSegment(sketch, "E363", {"start": v(425.6, 264.3) * mm, "end": v(425.09, 264.53) * mm});
            skLineSegment(sketch, "E364", {"start": v(425.09, 264.53) * mm, "end": v(424.6, 264.77) * mm});
            skLineSegment(sketch, "E365", {"start": v(424.6, 264.77) * mm, "end": v(424.1, 265.02) * mm});
            skLineSegment(sketch, "E366", {"start": v(424.1, 265.02) * mm, "end": v(423.6, 265.28) * mm});
            skLineSegment(sketch, "E367", {"start": v(423.6, 265.28) * mm, "end": v(423.13, 265.56) * mm});
            skLineSegment(sketch, "E368", {"start": v(423.13, 265.56) * mm, "end": v(422.65, 265.84) * mm});
            skLineSegment(sketch, "E369", {"start": v(422.65, 265.84) * mm, "end": v(422.19, 266.14) * mm});
            skLineSegment(sketch, "E370", {"start": v(422.19, 266.14) * mm, "end": v(421.73, 266.46) * mm});
            skLineSegment(sketch, "E371", {"start": v(421.73, 266.46) * mm, "end": v(421.27, 266.78) * mm});
            skLineSegment(sketch, "E372", {"start": v(421.27, 266.78) * mm, "end": v(420.83, 267.11) * mm});
            skLineSegment(sketch, "E373", {"start": v(420.83, 267.11) * mm, "end": v(420.4, 267.46) * mm});
            skLineSegment(sketch, "E374", {"start": v(420.4, 267.46) * mm, "end": v(419.96, 267.82) * mm});
            skLineSegment(sketch, "E375", {"start": v(419.96, 267.82) * mm, "end": v(419.54, 268.2) * mm});
            skLineSegment(sketch, "E376", {"start": v(419.54, 268.2) * mm, "end": v(419.13, 268.57) * mm});
            skLineSegment(sketch, "E377", {"start": v(419.13, 268.57) * mm, "end": v(418.84, 268.86) * mm});
            skLineSegment(sketch, "E378", {"start": v(418.84, 268.86) * mm, "end": v(418.56, 269.15) * mm});
            skLineSegment(sketch, "E379", {"start": v(418.56, 269.15) * mm, "end": v(418.28, 269.45) * mm});
            skLineSegment(sketch, "E380", {"start": v(418.28, 269.45) * mm, "end": v(418.02, 269.76) * mm});
            skLineSegment(sketch, "E381", {"start": v(418.02, 269.76) * mm, "end": v(417.76, 270.07) * mm});
            skLineSegment(sketch, "E382", {"start": v(417.76, 270.07) * mm, "end": v(417.51, 270.39) * mm});
            skLineSegment(sketch, "E383", {"start": v(417.51, 270.39) * mm, "end": v(417.27, 270.71) * mm});
            skLineSegment(sketch, "E384", {"start": v(417.27, 270.71) * mm, "end": v(417.04, 271.04) * mm});
            skLineSegment(sketch, "E385", {"start": v(417.04, 271.04) * mm, "end": v(416.82, 271.38) * mm});
            skLineSegment(sketch, "E386", {"start": v(416.82, 271.38) * mm, "end": v(416.6, 271.72) * mm});
            skLineSegment(sketch, "E387", {"start": v(416.6, 271.72) * mm, "end": v(416.4, 272.06) * mm});
            skLineSegment(sketch, "E388", {"start": v(416.4, 272.06) * mm, "end": v(416.2, 272.41) * mm});
            skLineSegment(sketch, "E389", {"start": v(416.2, 272.41) * mm, "end": v(416.02, 272.77) * mm});
            skLineSegment(sketch, "E390", {"start": v(416.02, 272.77) * mm, "end": v(415.84, 273.13) * mm});
            skLineSegment(sketch, "E391", {"start": v(415.84, 273.13) * mm, "end": v(415.67, 273.5) * mm});
            skLineSegment(sketch, "E392", {"start": v(415.67, 273.5) * mm, "end": v(415.51, 273.86) * mm});
            skLineSegment(sketch, "E393", {"start": v(415.51, 273.86) * mm, "end": v(415.36, 274.23) * mm});
            skLineSegment(sketch, "E394", {"start": v(415.36, 274.23) * mm, "end": v(415.22, 274.6) * mm});
            skLineSegment(sketch, "E395", {"start": v(415.22, 274.6) * mm, "end": v(415.1, 274.99) * mm});
            skLineSegment(sketch, "E396", {"start": v(415.1, 274.99) * mm, "end": v(414.97, 275.37) * mm});
            skLineSegment(sketch, "E397", {"start": v(414.97, 275.37) * mm, "end": v(414.86, 275.76) * mm});
            skLineSegment(sketch, "E398", {"start": v(414.86, 275.76) * mm, "end": v(414.76, 276.14) * mm});
            skLineSegment(sketch, "E399", {"start": v(414.76, 276.14) * mm, "end": v(414.67, 276.54) * mm});
            skLineSegment(sketch, "E400", {"start": v(414.67, 276.54) * mm, "end": v(414.59, 276.93) * mm});
            skLineSegment(sketch, "E401", {"start": v(414.59, 276.93) * mm, "end": v(414.51, 277.33) * mm});
            skLineSegment(sketch, "E402", {"start": v(414.51, 277.33) * mm, "end": v(414.45, 277.72) * mm});
            skLineSegment(sketch, "E403", {"start": v(414.45, 277.72) * mm, "end": v(414.4, 278.13) * mm});
            skLineSegment(sketch, "E404", {"start": v(414.4, 278.13) * mm, "end": v(414.36, 278.53) * mm});
            skLineSegment(sketch, "E405", {"start": v(414.36, 278.53) * mm, "end": v(414.33, 278.93) * mm});
            skLineSegment(sketch, "E406", {"start": v(414.33, 278.93) * mm, "end": v(414.31, 279.34) * mm});
            skLineSegment(sketch, "E407", {"start": v(414.31, 279.34) * mm, "end": v(414.3, 279.74) * mm});
            skLineSegment(sketch, "E408", {"start": v(414.3, 279.74) * mm, "end": v(414.3, 280.15) * mm});
            skLineSegment(sketch, "E409", {"start": v(414.3, 280.15) * mm, "end": v(414.3, 280.57) * mm});
            skLineSegment(sketch, "E410", {"start": v(414.3, 280.57) * mm, "end": v(414.32, 280.98) * mm});
            skLineSegment(sketch, "E411", {"start": v(414.32, 280.98) * mm, "end": v(414.35, 281.4) * mm});
            skLineSegment(sketch, "E412", {"start": v(414.35, 281.4) * mm, "end": v(414.38, 281.8) * mm});
            skLineSegment(sketch, "E413", {"start": v(414.38, 281.8) * mm, "end": v(414.43, 282.2) * mm});
            skLineSegment(sketch, "E414", {"start": v(414.43, 282.2) * mm, "end": v(414.49, 282.62) * mm});
            skLineSegment(sketch, "E415", {"start": v(414.49, 282.62) * mm, "end": v(414.55, 283.02) * mm});
            skLineSegment(sketch, "E416", {"start": v(414.55, 283.02) * mm, "end": v(414.63, 283.42) * mm});
            skLineSegment(sketch, "E417", {"start": v(414.63, 283.42) * mm, "end": v(414.72, 283.82) * mm});
            skLineSegment(sketch, "E418", {"start": v(414.72, 283.82) * mm, "end": v(414.82, 284.22) * mm});
            skLineSegment(sketch, "E419", {"start": v(414.82, 284.22) * mm, "end": v(414.93, 284.61) * mm});
            skLineSegment(sketch, "E420", {"start": v(414.93, 284.61) * mm, "end": v(415.04, 285) * mm});
            skLineSegment(sketch, "E421", {"start": v(415.04, 285) * mm, "end": v(415.17, 285.4) * mm});
            skLineSegment(sketch, "E422", {"start": v(415.17, 285.4) * mm, "end": v(415.3, 285.78) * mm});
            skLineSegment(sketch, "E423", {"start": v(415.3, 285.78) * mm, "end": v(415.46, 286.16) * mm});
            skLineSegment(sketch, "E424", {"start": v(415.46, 286.16) * mm, "end": v(415.61, 286.53) * mm});
            skLineSegment(sketch, "E425", {"start": v(415.61, 286.53) * mm, "end": v(415.78, 286.9) * mm});
            skLineSegment(sketch, "E426", {"start": v(415.78, 286.9) * mm, "end": v(415.95, 287.27) * mm});
            skLineSegment(sketch, "E427", {"start": v(415.95, 287.27) * mm, "end": v(416.14, 287.64) * mm});
            skLineSegment(sketch, "E428", {"start": v(416.14, 287.64) * mm, "end": v(416.33, 288) * mm});
            skLineSegment(sketch, "E429", {"start": v(416.33, 288) * mm, "end": v(416.54, 288.35) * mm});
            skLineSegment(sketch, "E430", {"start": v(416.54, 288.35) * mm, "end": v(416.75, 288.7) * mm});
            skLineSegment(sketch, "E431", {"start": v(416.75, 288.7) * mm, "end": v(416.97, 289.04) * mm});
            skLineSegment(sketch, "E432", {"start": v(416.97, 289.04) * mm, "end": v(417.2, 289.38) * mm});
            skLineSegment(sketch, "E433", {"start": v(417.2, 289.38) * mm, "end": v(417.44, 289.71) * mm});
            skLineSegment(sketch, "E434", {"start": v(417.44, 289.71) * mm, "end": v(417.69, 290.04) * mm});
            skLineSegment(sketch, "E435", {"start": v(417.69, 290.04) * mm, "end": v(417.94, 290.36) * mm});
            skLineSegment(sketch, "E436", {"start": v(417.94, 290.36) * mm, "end": v(418.21, 290.67) * mm});
            skLineSegment(sketch, "E437", {"start": v(418.21, 290.67) * mm, "end": v(418.48, 290.98) * mm});
            skLineSegment(sketch, "E438", {"start": v(418.48, 290.98) * mm, "end": v(418.77, 291.28) * mm});
            skLineSegment(sketch, "E439", {"start": v(418.77, 291.28) * mm, "end": v(419.06, 291.57) * mm});
            skLineSegment(sketch, "E440", {"start": v(419.06, 291.57) * mm, "end": v(419.36, 291.86) * mm});
            skLineSegment(sketch, "E441", {"start": v(419.36, 291.86) * mm, "end": v(419.77, 292.23) * mm});
            skLineSegment(sketch, "E442", {"start": v(419.77, 292.23) * mm, "end": v(420.18, 292.59) * mm});
            skLineSegment(sketch, "E443", {"start": v(420.18, 292.59) * mm, "end": v(420.6, 292.94) * mm});
            skLineSegment(sketch, "E444", {"start": v(420.6, 292.94) * mm, "end": v(421.04, 293.27) * mm});
            skLineSegment(sketch, "E445", {"start": v(421.04, 293.27) * mm, "end": v(421.49, 293.6) * mm});
            skLineSegment(sketch, "E446", {"start": v(421.49, 293.6) * mm, "end": v(421.93, 293.91) * mm});
            skLineSegment(sketch, "E447", {"start": v(421.93, 293.91) * mm, "end": v(422.39, 294.21) * mm});
            skLineSegment(sketch, "E448", {"start": v(422.39, 294.21) * mm, "end": v(422.85, 294.5) * mm});
            skLineSegment(sketch, "E449", {"start": v(422.85, 294.5) * mm, "end": v(423.32, 294.78) * mm});
            skLineSegment(sketch, "E450", {"start": v(423.32, 294.78) * mm, "end": v(423.8, 295.05) * mm});
            skLineSegment(sketch, "E451", {"start": v(423.8, 295.05) * mm, "end": v(424.28, 295.3) * mm});
            skLineSegment(sketch, "E452", {"start": v(424.28, 295.3) * mm, "end": v(424.77, 295.54) * mm});
            skLineSegment(sketch, "E453", {"start": v(424.77, 295.54) * mm, "end": v(425.26, 295.77) * mm});
            skLineSegment(sketch, "E454", {"start": v(425.26, 295.77) * mm, "end": v(425.76, 296) * mm});
            skLineSegment(sketch, "E455", {"start": v(425.76, 296) * mm, "end": v(426.26, 296.2) * mm});
            skLineSegment(sketch, "E456", {"start": v(426.26, 296.2) * mm, "end": v(426.77, 296.39) * mm});
            skLineSegment(sketch, "E457", {"start": v(426.77, 296.39) * mm, "end": v(427.29, 296.57) * mm});
            skLineSegment(sketch, "E458", {"start": v(427.29, 296.57) * mm, "end": v(427.8, 296.74) * mm});
            skLineSegment(sketch, "E459", {"start": v(427.8, 296.74) * mm, "end": v(428.33, 296.89) * mm});
            skLineSegment(sketch, "E460", {"start": v(428.33, 296.89) * mm, "end": v(428.85, 297.03) * mm});
            skLineSegment(sketch, "E461", {"start": v(428.85, 297.03) * mm, "end": v(429.38, 297.16) * mm});
            skLineSegment(sketch, "E462", {"start": v(429.38, 297.16) * mm, "end": v(429.91, 297.28) * mm});
            skLineSegment(sketch, "E463", {"start": v(429.91, 297.28) * mm, "end": v(430.45, 297.38) * mm});
            skLineSegment(sketch, "E464", {"start": v(430.45, 297.38) * mm, "end": v(430.99, 297.47) * mm});
            skLineSegment(sketch, "E465", {"start": v(430.99, 297.47) * mm, "end": v(431.53, 297.54) * mm});
            skLineSegment(sketch, "E466", {"start": v(431.53, 297.54) * mm, "end": v(432.07, 297.6) * mm});
            skLineSegment(sketch, "E467", {"start": v(432.07, 297.6) * mm, "end": v(432.62, 297.66) * mm});
            skLineSegment(sketch, "E468", {"start": v(432.62, 297.66) * mm, "end": v(433.16, 297.7) * mm});
            skLineSegment(sketch, "E469", {"start": v(433.16, 297.7) * mm, "end": v(433.71, 297.71) * mm});
            skLineSegment(sketch, "E470", {"start": v(433.71, 297.71) * mm, "end": v(434.26, 297.72) * mm});
            skLineSegment(sketch, "E471", {"start": v(434.26, 297.72) * mm, "end": v(434.81, 297.72) * mm});
            skLineSegment(sketch, "E472", {"start": v(434.81, 297.72) * mm, "end": v(435.36, 297.7) * mm});
            skLineSegment(sketch, "E473", {"start": v(435.36, 297.7) * mm, "end": v(435.88, 297.7) * mm});
            skLineSegment(sketch, "E474", {"start": v(435.88, 297.7) * mm, "end": v(436.4, 297.7) * mm});
            skLineSegment(sketch, "E475", {"start": v(436.4, 297.7) * mm, "end": v(436.9, 297.68) * mm});
            skLineSegment(sketch, "E476", {"start": v(436.9, 297.68) * mm, "end": v(437.42, 297.65) * mm});
            skLineSegment(sketch, "E477", {"start": v(437.42, 297.65) * mm, "end": v(437.93, 297.6) * mm});
            skLineSegment(sketch, "E478", {"start": v(437.93, 297.6) * mm, "end": v(438.43, 297.55) * mm});
            skLineSegment(sketch, "E479", {"start": v(438.43, 297.55) * mm, "end": v(438.94, 297.48) * mm});
            skLineSegment(sketch, "E480", {"start": v(438.94, 297.48) * mm, "end": v(439.44, 297.4) * mm});
            skLineSegment(sketch, "E481", {"start": v(439.44, 297.4) * mm, "end": v(439.94, 297.3) * mm});
            skLineSegment(sketch, "E482", {"start": v(439.94, 297.3) * mm, "end": v(440.44, 297.2) * mm});
            skLineSegment(sketch, "E483", {"start": v(440.44, 297.2) * mm, "end": v(440.93, 297.08) * mm});
            skLineSegment(sketch, "E484", {"start": v(440.93, 297.08) * mm, "end": v(441.42, 296.95) * mm});
            skLineSegment(sketch, "E485", {"start": v(441.42, 296.95) * mm, "end": v(441.91, 296.81) * mm});
            skLineSegment(sketch, "E486", {"start": v(441.91, 296.81) * mm, "end": v(442.4, 296.66) * mm});
            skLineSegment(sketch, "E487", {"start": v(442.4, 296.66) * mm, "end": v(442.87, 296.5) * mm});
            skLineSegment(sketch, "E488", {"start": v(442.87, 296.5) * mm, "end": v(443.35, 296.31) * mm});
            skLineSegment(sketch, "E489", {"start": v(443.35, 296.31) * mm, "end": v(443.82, 296.12) * mm});
            skLineSegment(sketch, "E490", {"start": v(443.82, 296.12) * mm, "end": v(444.28, 295.92) * mm});
            skLineSegment(sketch, "E491", {"start": v(444.28, 295.92) * mm, "end": v(444.74, 295.7) * mm});
            skLineSegment(sketch, "E492", {"start": v(444.74, 295.7) * mm, "end": v(445.2, 295.48) * mm});
            skLineSegment(sketch, "E493", {"start": v(445.2, 295.48) * mm, "end": v(445.65, 295.25) * mm});
            skLineSegment(sketch, "E494", {"start": v(445.65, 295.25) * mm, "end": v(446.1, 295) * mm});
            skLineSegment(sketch, "E495", {"start": v(446.1, 295) * mm, "end": v(446.53, 294.74) * mm});
            skLineSegment(sketch, "E496", {"start": v(446.53, 294.74) * mm, "end": v(446.96, 294.47) * mm});
            skLineSegment(sketch, "E497", {"start": v(446.96, 294.47) * mm, "end": v(447.39, 294.2) * mm});
            skLineSegment(sketch, "E498", {"start": v(447.39, 294.2) * mm, "end": v(447.8, 293.9) * mm});
            skLineSegment(sketch, "E499", {"start": v(447.8, 293.9) * mm, "end": v(448.22, 293.6) * mm});
            skLineSegment(sketch, "E500", {"start": v(448.22, 293.6) * mm, "end": v(448.62, 293.29) * mm});
            skLineSegment(sketch, "E501", {"start": v(448.62, 293.29) * mm, "end": v(449.02, 292.96) * mm});
            skLineSegment(sketch, "E502", {"start": v(449.02, 292.96) * mm, "end": v(449.41, 292.63) * mm});
            skLineSegment(sketch, "E503", {"start": v(449.41, 292.63) * mm, "end": v(449.8, 292.29) * mm});
            skLineSegment(sketch, "E504", {"start": v(449.8, 292.29) * mm, "end": v(450.17, 291.93) * mm});
            skLineSegment(sketch, "E505", {"start": v(450.17, 291.93) * mm, "end": v(450.46, 291.64) * mm});
            skLineSegment(sketch, "E506", {"start": v(450.46, 291.64) * mm, "end": v(450.74, 291.34) * mm});
            skLineSegment(sketch, "E507", {"start": v(450.74, 291.34) * mm, "end": v(451.02, 291.03) * mm});
            skLineSegment(sketch, "E508", {"start": v(451.02, 291.03) * mm, "end": v(451.28, 290.72) * mm});
            skLineSegment(sketch, "E509", {"start": v(451.28, 290.72) * mm, "end": v(451.54, 290.4) * mm});
            skLineSegment(sketch, "E510", {"start": v(451.54, 290.4) * mm, "end": v(451.8, 290.07) * mm});
            skLineSegment(sketch, "E511", {"start": v(451.8, 290.07) * mm, "end": v(452.03, 289.74) * mm});
            skLineSegment(sketch, "E512", {"start": v(452.03, 289.74) * mm, "end": v(452.26, 289.4) * mm});
            skLineSegment(sketch, "E513", {"start": v(452.26, 289.4) * mm, "end": v(452.49, 289.06) * mm});
            skLineSegment(sketch, "E514", {"start": v(452.49, 289.06) * mm, "end": v(452.7, 288.72) * mm});
            skLineSegment(sketch, "E515", {"start": v(452.7, 288.72) * mm, "end": v(452.91, 288.36) * mm});
            skLineSegment(sketch, "E516", {"start": v(452.91, 288.36) * mm, "end": v(453.1, 288) * mm});
            skLineSegment(sketch, "E517", {"start": v(453.1, 288) * mm, "end": v(453.3, 287.64) * mm});
            skLineSegment(sketch, "E518", {"start": v(453.3, 287.64) * mm, "end": v(453.48, 287.28) * mm});
            skLineSegment(sketch, "E519", {"start": v(453.48, 287.28) * mm, "end": v(453.65, 286.9) * mm});
            skLineSegment(sketch, "E520", {"start": v(453.65, 286.9) * mm, "end": v(453.8, 286.53) * mm});
            skLineSegment(sketch, "E521", {"start": v(453.8, 286.53) * mm, "end": v(453.96, 286.15) * mm});
            skLineSegment(sketch, "E522", {"start": v(453.96, 286.15) * mm, "end": v(454.1, 285.77) * mm});
            skLineSegment(sketch, "E523", {"start": v(454.1, 285.77) * mm, "end": v(454.23, 285.39) * mm});
            skLineSegment(sketch, "E524", {"start": v(454.23, 285.39) * mm, "end": v(454.36, 285) * mm});
            skLineSegment(sketch, "E525", {"start": v(454.36, 285) * mm, "end": v(454.47, 284.6) * mm});
            skLineSegment(sketch, "E526", {"start": v(454.47, 284.6) * mm, "end": v(454.58, 284.21) * mm});
            skLineSegment(sketch, "E527", {"start": v(454.58, 284.21) * mm, "end": v(454.67, 283.81) * mm});
            skLineSegment(sketch, "E528", {"start": v(454.67, 283.81) * mm, "end": v(454.75, 283.41) * mm});
            skLineSegment(sketch, "E529", {"start": v(454.75, 283.41) * mm, "end": v(454.83, 283.01) * mm});
            skLineSegment(sketch, "E530", {"start": v(454.83, 283.01) * mm, "end": v(454.9, 282.6) * mm});
            skLineSegment(sketch, "E531", {"start": v(454.9, 282.6) * mm, "end": v(454.95, 282.2) * mm});
            skLineSegment(sketch, "E532", {"start": v(454.95, 282.2) * mm, "end": v(455, 281.8) * mm});
            skLineSegment(sketch, "E533", {"start": v(455, 281.8) * mm, "end": v(455.03, 281.38) * mm});
            skLineSegment(sketch, "E534", {"start": v(455.03, 281.38) * mm, "end": v(455.05, 280.97) * mm});
            skLineSegment(sketch, "E535", {"start": v(455.05, 280.97) * mm, "end": v(455.06, 280.56) * mm});
            skLineSegment(sketch, "E536", {"start": v(455.06, 280.56) * mm, "end": v(455.07, 280.14) * mm});
            skLineSegment(sketch, "E537", {"start": v(454.5, 306.72) * mm, "end": v(414.55, 306.72) * mm});
            skLineSegment(sketch, "E538", {"start": v(414.55, 306.72) * mm, "end": v(414.55, 324.28) * mm});
            skLineSegment(sketch, "E539", {"start": v(414.55, 324.28) * mm, "end": v(414.55, 324.77) * mm});
            skLineSegment(sketch, "E540", {"start": v(414.55, 324.77) * mm, "end": v(414.58, 325.26) * mm});
            skLineSegment(sketch, "E541", {"start": v(414.58, 325.26) * mm, "end": v(414.63, 325.75) * mm});
            skLineSegment(sketch, "E542", {"start": v(414.63, 325.75) * mm, "end": v(414.71, 326.23) * mm});
            skLineSegment(sketch, "E543", {"start": v(414.71, 326.23) * mm, "end": v(414.81, 326.71) * mm});
            skLineSegment(sketch, "E544", {"start": v(414.81, 326.71) * mm, "end": v(414.94, 327.18) * mm});
            skLineSegment(sketch, "E545", {"start": v(414.94, 327.18) * mm, "end": v(415.1, 327.64) * mm});
            skLineSegment(sketch, "E546", {"start": v(415.1, 327.64) * mm, "end": v(415.27, 328.1) * mm});
            skLineSegment(sketch, "E547", {"start": v(415.27, 328.1) * mm, "end": v(415.46, 328.54) * mm});
            skLineSegment(sketch, "E548", {"start": v(415.46, 328.54) * mm, "end": v(415.68, 328.98) * mm});
            skLineSegment(sketch, "E549", {"start": v(415.68, 328.98) * mm, "end": v(415.92, 329.4) * mm});
            skLineSegment(sketch, "E550", {"start": v(415.92, 329.4) * mm, "end": v(416.19, 329.81) * mm});
            skLineSegment(sketch, "E551", {"start": v(416.19, 329.81) * mm, "end": v(416.47, 330.21) * mm});
            skLineSegment(sketch, "E552", {"start": v(416.47, 330.21) * mm, "end": v(416.78, 330.6) * mm});
            skLineSegment(sketch, "E553", {"start": v(416.78, 330.6) * mm, "end": v(417.1, 330.97) * mm});
            skLineSegment(sketch, "E554", {"start": v(417.1, 330.97) * mm, "end": v(417.45, 331.32) * mm});
            skLineSegment(sketch, "E555", {"start": v(417.45, 331.32) * mm, "end": v(417.8, 331.66) * mm});
            skLineSegment(sketch, "E556", {"start": v(417.8, 331.66) * mm, "end": v(418.17, 331.98) * mm});
            skLineSegment(sketch, "E557", {"start": v(418.17, 331.98) * mm, "end": v(418.55, 332.28) * mm});
            skLineSegment(sketch, "E558", {"start": v(418.55, 332.28) * mm, "end": v(418.94, 332.56) * mm});
            skLineSegment(sketch, "E559", {"start": v(418.94, 332.56) * mm, "end": v(419.35, 332.82) * mm});
            skLineSegment(sketch, "E560", {"start": v(419.35, 332.82) * mm, "end": v(419.77, 333.06) * mm});
            skLineSegment(sketch, "E561", {"start": v(419.77, 333.06) * mm, "end": v(420.2, 333.28) * mm});
            skLineSegment(sketch, "E562", {"start": v(420.2, 333.28) * mm, "end": v(420.64, 333.48) * mm});
            skLineSegment(sketch, "E563", {"start": v(420.64, 333.48) * mm, "end": v(421.1, 333.66) * mm});
            skLineSegment(sketch, "E564", {"start": v(421.1, 333.66) * mm, "end": v(421.55, 333.8) * mm});
            skLineSegment(sketch, "E565", {"start": v(421.55, 333.8) * mm, "end": v(422.01, 333.94) * mm});
            skLineSegment(sketch, "E566", {"start": v(422.01, 333.94) * mm, "end": v(422.49, 334.05) * mm});
            skLineSegment(sketch, "E567", {"start": v(422.49, 334.05) * mm, "end": v(422.96, 334.13) * mm});
            skLineSegment(sketch, "E568", {"start": v(422.96, 334.13) * mm, "end": v(423.45, 334.19) * mm});
            skLineSegment(sketch, "E569", {"start": v(423.45, 334.19) * mm, "end": v(423.93, 334.23) * mm});
            skLineSegment(sketch, "E570", {"start": v(423.93, 334.23) * mm, "end": v(424.42, 334.24) * mm});
            skLineSegment(sketch, "E571", {"start": v(424.42, 334.24) * mm, "end": v(424.92, 334.24) * mm});
            skLineSegment(sketch, "E572", {"start": v(424.92, 334.24) * mm, "end": v(425.42, 334.22) * mm});
            skLineSegment(sketch, "E573", {"start": v(425.42, 334.22) * mm, "end": v(425.92, 334.17) * mm});
            skLineSegment(sketch, "E574", {"start": v(425.92, 334.17) * mm, "end": v(426.41, 334.1) * mm});
            skLineSegment(sketch, "E575", {"start": v(426.41, 334.1) * mm, "end": v(426.9, 334) * mm});
            skLineSegment(sketch, "E576", {"start": v(426.9, 334) * mm, "end": v(427.38, 333.88) * mm});
            skLineSegment(sketch, "E577", {"start": v(427.38, 333.88) * mm, "end": v(427.85, 333.73) * mm});
            skLineSegment(sketch, "E578", {"start": v(427.85, 333.73) * mm, "end": v(428.31, 333.56) * mm});
            skLineSegment(sketch, "E579", {"start": v(428.31, 333.56) * mm, "end": v(428.77, 333.37) * mm});
            skLineSegment(sketch, "E580", {"start": v(428.77, 333.37) * mm, "end": v(429.21, 333.15) * mm});
            skLineSegment(sketch, "E581", {"start": v(429.21, 333.15) * mm, "end": v(429.65, 332.91) * mm});
            skLineSegment(sketch, "E582", {"start": v(429.65, 332.91) * mm, "end": v(430.07, 332.65) * mm});
            skLineSegment(sketch, "E583", {"start": v(430.07, 332.65) * mm, "end": v(430.48, 332.37) * mm});
            skLineSegment(sketch, "E584", {"start": v(430.48, 332.37) * mm, "end": v(430.87, 332.07) * mm});
            skLineSegment(sketch, "E585", {"start": v(430.87, 332.07) * mm, "end": v(431.25, 331.74) * mm});
            skLineSegment(sketch, "E586", {"start": v(431.25, 331.74) * mm, "end": v(431.62, 331.4) * mm});
            skLineSegment(sketch, "E587", {"start": v(431.62, 331.4) * mm, "end": v(431.96, 331.04) * mm});
            skLineSegment(sketch, "E588", {"start": v(431.96, 331.04) * mm, "end": v(432.29, 330.66) * mm});
            skLineSegment(sketch, "E589", {"start": v(432.29, 330.66) * mm, "end": v(432.59, 330.27) * mm});
            skLineSegment(sketch, "E590", {"start": v(432.59, 330.27) * mm, "end": v(432.87, 329.87) * mm});
            skLineSegment(sketch, "E591", {"start": v(432.87, 329.87) * mm, "end": v(433.13, 329.45) * mm});
            skLineSegment(sketch, "E592", {"start": v(433.13, 329.45) * mm, "end": v(433.37, 329.02) * mm});
            skLineSegment(sketch, "E593", {"start": v(433.37, 329.02) * mm, "end": v(433.6, 328.58) * mm});
            skLineSegment(sketch, "E594", {"start": v(433.6, 328.58) * mm, "end": v(433.79, 328.13) * mm});
            skLineSegment(sketch, "E595", {"start": v(433.79, 328.13) * mm, "end": v(433.96, 327.67) * mm});
            skLineSegment(sketch, "E596", {"start": v(433.96, 327.67) * mm, "end": v(434.11, 327.2) * mm});
            skLineSegment(sketch, "E597", {"start": v(434.11, 327.2) * mm, "end": v(434.24, 326.73) * mm});
            skLineSegment(sketch, "E598", {"start": v(434.24, 326.73) * mm, "end": v(434.35, 326.25) * mm});
            skLineSegment(sketch, "E599", {"start": v(434.35, 326.25) * mm, "end": v(434.43, 325.76) * mm});
            skLineSegment(sketch, "E600", {"start": v(434.43, 325.76) * mm, "end": v(434.48, 325.27) * mm});
            skLineSegment(sketch, "E601", {"start": v(434.48, 325.27) * mm, "end": v(434.51, 324.77) * mm});
            skLineSegment(sketch, "E602", {"start": v(434.51, 324.77) * mm, "end": v(434.52, 324.28) * mm});
            skLineSegment(sketch, "E603", {"start": v(434.52, 324.28) * mm, "end": v(434.52, 306.72) * mm});
            skLineSegment(sketch, "E604", {"start": v(434.52, 324.28) * mm, "end": v(434.52, 324.69) * mm});
            skLineSegment(sketch, "E605", {"start": v(434.52, 324.69) * mm, "end": v(434.54, 325.1) * mm});
            skLineSegment(sketch, "E606", {"start": v(434.54, 325.1) * mm, "end": v(434.58, 325.5) * mm});
            skLineSegment(sketch, "E607", {"start": v(434.58, 325.5) * mm, "end": v(434.65, 325.9) * mm});
            skLineSegment(sketch, "E608", {"start": v(434.65, 325.9) * mm, "end": v(434.73, 326.3) * mm});
            skLineSegment(sketch, "E609", {"start": v(434.73, 326.3) * mm, "end": v(434.84, 326.69) * mm});
            skLineSegment(sketch, "E610", {"start": v(434.84, 326.69) * mm, "end": v(434.96, 327.07) * mm});
            skLineSegment(sketch, "E611", {"start": v(434.96, 327.07) * mm, "end": v(435.1, 327.45) * mm});
            skLineSegment(sketch, "E612", {"start": v(435.1, 327.45) * mm, "end": v(435.26, 327.82) * mm});
            skLineSegment(sketch, "E613", {"start": v(435.26, 327.82) * mm, "end": v(435.45, 328.18) * mm});
            skLineSegment(sketch, "E614", {"start": v(435.45, 328.18) * mm, "end": v(435.64, 328.53) * mm});
            skLineSegment(sketch, "E615", {"start": v(435.64, 328.53) * mm, "end": v(435.86, 328.87) * mm});
            skLineSegment(sketch, "E616", {"start": v(435.86, 328.87) * mm, "end": v(436.1, 329.2) * mm});
            skLineSegment(sketch, "E617", {"start": v(436.1, 329.2) * mm, "end": v(436.35, 329.53) * mm});
            skLineSegment(sketch, "E618", {"start": v(436.35, 329.53) * mm, "end": v(436.61, 329.83) * mm});
            skLineSegment(sketch, "E619", {"start": v(436.61, 329.83) * mm, "end": v(436.9, 330.13) * mm});
            skLineSegment(sketch, "E620", {"start": v(436.9, 330.13) * mm, "end": v(437.4, 330.47) * mm});
            skLineSegment(sketch, "E621", {"start": v(437.4, 330.47) * mm, "end": v(437.91, 330.79) * mm});
            skLineSegment(sketch, "E622", {"start": v(437.91, 330.79) * mm, "end": v(438.44, 331.08) * mm});
            skLineSegment(sketch, "E623", {"start": v(438.44, 331.08) * mm, "end": v(438.98, 331.35) * mm});
            skLineSegment(sketch, "E624", {"start": v(438.98, 331.35) * mm, "end": v(439.52, 331.6) * mm});
            skLineSegment(sketch, "E625", {"start": v(439.52, 331.6) * mm, "end": v(440.08, 331.81) * mm});
            skLineSegment(sketch, "E626", {"start": v(440.08, 331.81) * mm, "end": v(440.65, 332) * mm});
            skLineSegment(sketch, "E627", {"start": v(440.65, 332) * mm, "end": v(441.22, 332.18) * mm});
            skLineSegment(sketch, "E628", {"start": v(441.22, 332.18) * mm, "end": v(441.8, 332.32) * mm});
            skLineSegment(sketch, "E629", {"start": v(441.8, 332.32) * mm, "end": v(442.39, 332.44) * mm});
            skLineSegment(sketch, "E630", {"start": v(442.39, 332.44) * mm, "end": v(442.98, 332.53) * mm});
            skLineSegment(sketch, "E631", {"start": v(442.98, 332.53) * mm, "end": v(443.58, 332.6) * mm});
            skLineSegment(sketch, "E632", {"start": v(443.58, 332.6) * mm, "end": v(444.18, 332.63) * mm});
            skLineSegment(sketch, "E633", {"start": v(444.18, 332.63) * mm, "end": v(444.78, 332.65) * mm});
            skLineSegment(sketch, "E634", {"start": v(444.78, 332.65) * mm, "end": v(445.38, 332.63) * mm});
            skLineSegment(sketch, "E635", {"start": v(445.38, 332.63) * mm, "end": v(445.99, 332.59) * mm});
            skLineSegment(sketch, "E636", {"start": v(445.99, 332.59) * mm, "end": v(446.52, 332.58) * mm});
            skLineSegment(sketch, "E637", {"start": v(446.52, 332.58) * mm, "end": v(447.06, 332.58) * mm});
            skLineSegment(sketch, "E638", {"start": v(447.06, 332.58) * mm, "end": v(447.6, 332.6) * mm});
            skLineSegment(sketch, "E639", {"start": v(447.6, 332.6) * mm, "end": v(448.14, 332.62) * mm});
            skLineSegment(sketch, "E640", {"start": v(448.14, 332.62) * mm, "end": v(448.67, 332.65) * mm});
            skLineSegment(sketch, "E641", {"start": v(448.67, 332.65) * mm, "end": v(449.21, 332.69) * mm});
            skLineSegment(sketch, "E642", {"start": v(449.21, 332.69) * mm, "end": v(449.75, 332.74) * mm});
            skLineSegment(sketch, "E643", {"start": v(449.75, 332.74) * mm, "end": v(450.28, 332.8) * mm});
            skLineSegment(sketch, "E644", {"start": v(450.28, 332.8) * mm, "end": v(450.82, 332.87) * mm});
            skLineSegment(sketch, "E645", {"start": v(450.82, 332.87) * mm, "end": v(451.35, 332.95) * mm});
            skLineSegment(sketch, "E646", {"start": v(451.35, 332.95) * mm, "end": v(451.88, 333.03) * mm});
            skLineSegment(sketch, "E647", {"start": v(451.88, 333.03) * mm, "end": v(452.4, 333.13) * mm});
            skLineSegment(sketch, "E648", {"start": v(452.4, 333.13) * mm, "end": v(452.94, 333.24) * mm});
            skLineSegment(sketch, "E649", {"start": v(452.94, 333.24) * mm, "end": v(453.46, 333.36) * mm});
            skLineSegment(sketch, "E650", {"start": v(453.46, 333.36) * mm, "end": v(453.99, 333.48) * mm});
            skLineSegment(sketch, "E651", {"start": v(453.99, 333.48) * mm, "end": v(454.5, 333.62) * mm});
            skLineSegment(sketch, "E652", {"start": v(129.17, 345.3) * mm, "end": v(169.16, 345.3) * mm});
            skLineSegment(sketch, "E653", {"start": v(169.16, 345.3) * mm, "end": v(169.16, 320.43) * mm});
            skLineSegment(sketch, "E654", {"start": v(150.05, 345.3) * mm, "end": v(150.05, 322.22) * mm});
            skLineSegment(sketch, "E655", {"start": v(129.2, 288.13) * mm, "end": v(129.2, 311.63) * mm});
            skLineSegment(sketch, "E656", {"start": v(129.2, 311.63) * mm, "end": v(169.14, 311.63) * mm});
            skLineSegment(sketch, "E657", {"start": v(128.63, 272.97) * mm, "end": v(128.63, 273.39) * mm});
            skLineSegment(sketch, "E658", {"start": v(128.63, 273.39) * mm, "end": v(128.64, 273.8) * mm});
            skLineSegment(sketch, "E659", {"start": v(128.64, 273.8) * mm, "end": v(128.65, 274.23) * mm});
            skLineSegment(sketch, "E660", {"start": v(128.65, 274.23) * mm, "end": v(128.68, 274.64) * mm});
            skLineSegment(sketch, "E661", {"start": v(128.68, 274.64) * mm, "end": v(128.72, 275.06) * mm});
            skLineSegment(sketch, "E662", {"start": v(128.72, 275.06) * mm, "end": v(128.77, 275.47) * mm});
            skLineSegment(sketch, "E663", {"start": v(128.77, 275.47) * mm, "end": v(128.83, 275.88) * mm});
            skLineSegment(sketch, "E664", {"start": v(128.83, 275.88) * mm, "end": v(128.9, 276.3) * mm});
            skLineSegment(sketch, "E665", {"start": v(128.9, 276.3) * mm, "end": v(128.98, 276.7) * mm});
            skLineSegment(sketch, "E666", {"start": v(128.98, 276.7) * mm, "end": v(129.07, 277.1) * mm});
            skLineSegment(sketch, "E667", {"start": v(129.07, 277.1) * mm, "end": v(129.17, 277.5) * mm});
            skLineSegment(sketch, "E668", {"start": v(129.17, 277.5) * mm, "end": v(129.28, 277.9) * mm});
            skLineSegment(sketch, "E669", {"start": v(129.28, 277.9) * mm, "end": v(129.4, 278.3) * mm});
            skLineSegment(sketch, "E670", {"start": v(129.4, 278.3) * mm, "end": v(129.52, 278.7) * mm});
            skLineSegment(sketch, "E671", {"start": v(129.52, 278.7) * mm, "end": v(129.66, 279.08) * mm});
            skLineSegment(sketch, "E672", {"start": v(129.66, 279.08) * mm, "end": v(129.81, 279.47) * mm});
            skLineSegment(sketch, "E673", {"start": v(129.81, 279.47) * mm, "end": v(129.97, 279.85) * mm});
            skLineSegment(sketch, "E674", {"start": v(129.97, 279.85) * mm, "end": v(130.14, 280.23) * mm});
            skLineSegment(sketch, "E675", {"start": v(130.14, 280.23) * mm, "end": v(130.31, 280.6) * mm});
            skLineSegment(sketch, "E676", {"start": v(130.31, 280.6) * mm, "end": v(130.5, 280.98) * mm});
            skLineSegment(sketch, "E677", {"start": v(130.5, 280.98) * mm, "end": v(130.7, 281.34) * mm});
            skLineSegment(sketch, "E678", {"start": v(130.7, 281.34) * mm, "end": v(130.9, 281.7) * mm});
            skLineSegment(sketch, "E679", {"start": v(130.9, 281.7) * mm, "end": v(131.11, 282.06) * mm});
            skLineSegment(sketch, "E680", {"start": v(131.11, 282.06) * mm, "end": v(131.33, 282.4) * mm});
            skLineSegment(sketch, "E681", {"start": v(131.33, 282.4) * mm, "end": v(131.57, 282.75) * mm});
            skLineSegment(sketch, "E682", {"start": v(131.57, 282.75) * mm, "end": v(131.8, 283.1) * mm});
            skLineSegment(sketch, "E683", {"start": v(131.8, 283.1) * mm, "end": v(132.05, 283.43) * mm});
            skLineSegment(sketch, "E684", {"start": v(132.05, 283.43) * mm, "end": v(132.31, 283.75) * mm});
            skLineSegment(sketch, "E685", {"start": v(132.31, 283.75) * mm, "end": v(132.58, 284.08) * mm});
            skLineSegment(sketch, "E686", {"start": v(132.58, 284.08) * mm, "end": v(132.85, 284.4) * mm});
            skLineSegment(sketch, "E687", {"start": v(132.85, 284.4) * mm, "end": v(133.13, 284.7) * mm});
            skLineSegment(sketch, "E688", {"start": v(133.13, 284.7) * mm, "end": v(133.43, 285) * mm});
            skLineSegment(sketch, "E689", {"start": v(133.43, 285) * mm, "end": v(133.8, 285.35) * mm});
            skLineSegment(sketch, "E690", {"start": v(133.8, 285.35) * mm, "end": v(134.2, 285.7) * mm});
            skLineSegment(sketch, "E691", {"start": v(134.2, 285.7) * mm, "end": v(134.6, 286.02) * mm});
            skLineSegment(sketch, "E692", {"start": v(134.6, 286.02) * mm, "end": v(135, 286.34) * mm});
            skLineSegment(sketch, "E693", {"start": v(135, 286.34) * mm, "end": v(135.4, 286.65) * mm});
            skLineSegment(sketch, "E694", {"start": v(135.4, 286.65) * mm, "end": v(135.82, 286.95) * mm});
            skLineSegment(sketch, "E695", {"start": v(135.82, 286.95) * mm, "end": v(136.25, 287.23) * mm});
            skLineSegment(sketch, "E696", {"start": v(136.25, 287.23) * mm, "end": v(136.68, 287.5) * mm});
            skLineSegment(sketch, "E697", {"start": v(136.68, 287.5) * mm, "end": v(137.11, 287.77) * mm});
            skLineSegment(sketch, "E698", {"start": v(137.11, 287.77) * mm, "end": v(137.56, 288.03) * mm});
            skLineSegment(sketch, "E699", {"start": v(137.56, 288.03) * mm, "end": v(138, 288.27) * mm});
            skLineSegment(sketch, "E700", {"start": v(138, 288.27) * mm, "end": v(138.46, 288.5) * mm});
            skLineSegment(sketch, "E701", {"start": v(138.46, 288.5) * mm, "end": v(138.92, 288.72) * mm});
            skLineSegment(sketch, "E702", {"start": v(138.92, 288.72) * mm, "end": v(139.38, 288.93) * mm});
            skLineSegment(sketch, "E703", {"start": v(139.38, 288.93) * mm, "end": v(139.85, 289.13) * mm});
            skLineSegment(sketch, "E704", {"start": v(139.85, 289.13) * mm, "end": v(140.33, 289.31) * mm});
            skLineSegment(sketch, "E705", {"start": v(140.33, 289.31) * mm, "end": v(140.8, 289.48) * mm});
            skLineSegment(sketch, "E706", {"start": v(140.8, 289.48) * mm, "end": v(141.29, 289.65) * mm});
            skLineSegment(sketch, "E707", {"start": v(141.29, 289.65) * mm, "end": v(141.78, 289.8) * mm});
            skLineSegment(sketch, "E708", {"start": v(141.78, 289.8) * mm, "end": v(142.27, 289.93) * mm});
            skLineSegment(sketch, "E709", {"start": v(142.27, 289.93) * mm, "end": v(142.76, 290.06) * mm});
            skLineSegment(sketch, "E710", {"start": v(142.76, 290.06) * mm, "end": v(143.26, 290.18) * mm});
            skLineSegment(sketch, "E711", {"start": v(143.26, 290.18) * mm, "end": v(143.76, 290.28) * mm});
            skLineSegment(sketch, "E712", {"start": v(143.76, 290.28) * mm, "end": v(144.26, 290.37) * mm});
            skLineSegment(sketch, "E713", {"start": v(144.26, 290.37) * mm, "end": v(144.77, 290.44) * mm});
            skLineSegment(sketch, "E714", {"start": v(144.77, 290.44) * mm, "end": v(145.27, 290.5) * mm});
            skLineSegment(sketch, "E715", {"start": v(145.27, 290.5) * mm, "end": v(145.78, 290.56) * mm});
            skLineSegment(sketch, "E716", {"start": v(145.78, 290.56) * mm, "end": v(146.3, 290.6) * mm});
            skLineSegment(sketch, "E717", {"start": v(146.3, 290.6) * mm, "end": v(146.8, 290.63) * mm});
            skLineSegment(sketch, "E718", {"start": v(146.8, 290.63) * mm, "end": v(147.32, 290.64) * mm});
            skLineSegment(sketch, "E719", {"start": v(147.32, 290.64) * mm, "end": v(147.84, 290.64) * mm});
            skLineSegment(sketch, "E720", {"start": v(147.84, 290.64) * mm, "end": v(148.36, 290.63) * mm});
            skLineSegment(sketch, "E721", {"start": v(148.36, 290.63) * mm, "end": v(148.92, 290.65) * mm});
            skLineSegment(sketch, "E722", {"start": v(148.92, 290.65) * mm, "end": v(149.48, 290.65) * mm});
            skLineSegment(sketch, "E723", {"start": v(149.48, 290.65) * mm, "end": v(150.04, 290.64) * mm});
            skLineSegment(sketch, "E724", {"start": v(150.04, 290.64) * mm, "end": v(150.6, 290.6) * mm});
            skLineSegment(sketch, "E725", {"start": v(150.6, 290.6) * mm, "end": v(151.15, 290.57) * mm});
            skLineSegment(sketch, "E726", {"start": v(151.15, 290.57) * mm, "end": v(151.7, 290.51) * mm});
            skLineSegment(sketch, "E727", {"start": v(151.7, 290.51) * mm, "end": v(152.26, 290.45) * mm});
            skLineSegment(sketch, "E728", {"start": v(152.26, 290.45) * mm, "end": v(152.8, 290.36) * mm});
            skLineSegment(sketch, "E729", {"start": v(152.8, 290.36) * mm, "end": v(153.35, 290.27) * mm});
            skLineSegment(sketch, "E730", {"start": v(153.35, 290.27) * mm, "end": v(153.9, 290.16) * mm});
            skLineSegment(sketch, "E731", {"start": v(153.9, 290.16) * mm, "end": v(154.44, 290.04) * mm});
            skLineSegment(sketch, "E732", {"start": v(154.44, 290.04) * mm, "end": v(154.97, 289.9) * mm});
            skLineSegment(sketch, "E733", {"start": v(154.97, 289.9) * mm, "end": v(155.5, 289.75) * mm});
            skLineSegment(sketch, "E734", {"start": v(155.5, 289.75) * mm, "end": v(156.03, 289.59) * mm});
            skLineSegment(sketch, "E735", {"start": v(156.03, 289.59) * mm, "end": v(156.56, 289.41) * mm});
            skLineSegment(sketch, "E736", {"start": v(156.56, 289.41) * mm, "end": v(157.08, 289.23) * mm});
            skLineSegment(sketch, "E737", {"start": v(157.08, 289.23) * mm, "end": v(157.6, 289.03) * mm});
            skLineSegment(sketch, "E738", {"start": v(157.6, 289.03) * mm, "end": v(158.1, 288.81) * mm});
            skLineSegment(sketch, "E739", {"start": v(158.1, 288.81) * mm, "end": v(158.6, 288.59) * mm});
            skLineSegment(sketch, "E740", {"start": v(158.6, 288.59) * mm, "end": v(159.1, 288.35) * mm});
            skLineSegment(sketch, "E741", {"start": v(159.1, 288.35) * mm, "end": v(159.6, 288.1) * mm});
            skLineSegment(sketch, "E742", {"start": v(159.6, 288.1) * mm, "end": v(160.09, 287.83) * mm});
            skLineSegment(sketch, "E743", {"start": v(160.09, 287.83) * mm, "end": v(160.57, 287.56) * mm});
            skLineSegment(sketch, "E744", {"start": v(160.57, 287.56) * mm, "end": v(161.04, 287.27) * mm});
            skLineSegment(sketch, "E745", {"start": v(161.04, 287.27) * mm, "end": v(161.5, 286.97) * mm});
            skLineSegment(sketch, "E746", {"start": v(161.5, 286.97) * mm, "end": v(161.97, 286.66) * mm});
            skLineSegment(sketch, "E747", {"start": v(161.97, 286.66) * mm, "end": v(162.42, 286.33) * mm});
            skLineSegment(sketch, "E748", {"start": v(162.42, 286.33) * mm, "end": v(162.87, 286) * mm});
            skLineSegment(sketch, "E749", {"start": v(162.87, 286) * mm, "end": v(163.3, 285.65) * mm});
            skLineSegment(sketch, "E750", {"start": v(163.3, 285.65) * mm, "end": v(163.73, 285.3) * mm});
            skLineSegment(sketch, "E751", {"start": v(163.73, 285.3) * mm, "end": v(164.15, 284.92) * mm});
            skLineSegment(sketch, "E752", {"start": v(164.15, 284.92) * mm, "end": v(164.56, 284.54) * mm});
            skLineSegment(sketch, "E753", {"start": v(164.56, 284.54) * mm, "end": v(164.86, 284.25) * mm});
            skLineSegment(sketch, "E754", {"start": v(164.86, 284.25) * mm, "end": v(165.14, 283.96) * mm});
            skLineSegment(sketch, "E755", {"start": v(165.14, 283.96) * mm, "end": v(165.41, 283.66) * mm});
            skLineSegment(sketch, "E756", {"start": v(165.41, 283.66) * mm, "end": v(165.68, 283.36) * mm});
            skLineSegment(sketch, "E757", {"start": v(165.68, 283.36) * mm, "end": v(165.94, 283.04) * mm});
            skLineSegment(sketch, "E758", {"start": v(165.94, 283.04) * mm, "end": v(166.18, 282.73) * mm});
            skLineSegment(sketch, "E759", {"start": v(166.18, 282.73) * mm, "end": v(166.42, 282.4) * mm});
            skLineSegment(sketch, "E760", {"start": v(166.42, 282.4) * mm, "end": v(166.66, 282.07) * mm});
            skLineSegment(sketch, "E761", {"start": v(166.66, 282.07) * mm, "end": v(166.88, 281.74) * mm});
            skLineSegment(sketch, "E762", {"start": v(166.88, 281.74) * mm, "end": v(167.1, 281.4) * mm});
            skLineSegment(sketch, "E763", {"start": v(167.1, 281.4) * mm, "end": v(167.3, 281.05) * mm});
            skLineSegment(sketch, "E764", {"start": v(167.3, 281.05) * mm, "end": v(167.5, 280.7) * mm});
            skLineSegment(sketch, "E765", {"start": v(167.5, 280.7) * mm, "end": v(167.68, 280.34) * mm});
            skLineSegment(sketch, "E766", {"start": v(167.68, 280.34) * mm, "end": v(167.86, 279.99) * mm});
            skLineSegment(sketch, "E767", {"start": v(167.86, 279.99) * mm, "end": v(168.03, 279.62) * mm});
            skLineSegment(sketch, "E768", {"start": v(168.03, 279.62) * mm, "end": v(168.19, 279.25) * mm});
            skLineSegment(sketch, "E769", {"start": v(168.19, 279.25) * mm, "end": v(168.33, 278.88) * mm});
            skLineSegment(sketch, "E770", {"start": v(168.33, 278.88) * mm, "end": v(168.47, 278.5) * mm});
            skLineSegment(sketch, "E771", {"start": v(168.47, 278.5) * mm, "end": v(168.6, 278.13) * mm});
            skLineSegment(sketch, "E772", {"start": v(168.6, 278.13) * mm, "end": v(168.73, 277.74) * mm});
            skLineSegment(sketch, "E773", {"start": v(168.73, 277.74) * mm, "end": v(168.84, 277.36) * mm});
            skLineSegment(sketch, "E774", {"start": v(168.84, 277.36) * mm, "end": v(168.94, 276.97) * mm});
            skLineSegment(sketch, "E775", {"start": v(168.94, 276.97) * mm, "end": v(169.03, 276.58) * mm});
            skLineSegment(sketch, "E776", {"start": v(169.03, 276.58) * mm, "end": v(169.11, 276.18) * mm});
            skLineSegment(sketch, "E777", {"start": v(169.11, 276.18) * mm, "end": v(169.18, 275.79) * mm});
            skLineSegment(sketch, "E778", {"start": v(169.18, 275.79) * mm, "end": v(169.24, 275.39) * mm});
            skLineSegment(sketch, "E779", {"start": v(169.24, 275.39) * mm, "end": v(169.3, 274.99) * mm});
            skLineSegment(sketch, "E780", {"start": v(169.3, 274.99) * mm, "end": v(169.33, 274.58) * mm});
            skLineSegment(sketch, "E781", {"start": v(169.33, 274.58) * mm, "end": v(169.36, 274.18) * mm});
            skLineSegment(sketch, "E782", {"start": v(169.36, 274.18) * mm, "end": v(169.38, 273.77) * mm});
            skLineSegment(sketch, "E783", {"start": v(169.38, 273.77) * mm, "end": v(169.4, 273.37) * mm});
            skLineSegment(sketch, "E784", {"start": v(169.4, 273.37) * mm, "end": v(169.4, 272.96) * mm});
            skLineSegment(sketch, "E785", {"start": v(169.4, 272.96) * mm, "end": v(169.39, 272.55) * mm});
            skLineSegment(sketch, "E786", {"start": v(169.39, 272.55) * mm, "end": v(169.37, 272.13) * mm});
            skLineSegment(sketch, "E787", {"start": v(169.37, 272.13) * mm, "end": v(169.35, 271.72) * mm});
            skLineSegment(sketch, "E788", {"start": v(169.35, 271.72) * mm, "end": v(169.31, 271.31) * mm});
            skLineSegment(sketch, "E789", {"start": v(169.31, 271.31) * mm, "end": v(169.27, 270.9) * mm});
            skLineSegment(sketch, "E790", {"start": v(169.27, 270.9) * mm, "end": v(169.2, 270.5) * mm});
            skLineSegment(sketch, "E791", {"start": v(169.2, 270.5) * mm, "end": v(169.14, 270.1) * mm});
            skLineSegment(sketch, "E792", {"start": v(169.14, 270.1) * mm, "end": v(169.06, 269.69) * mm});
            skLineSegment(sketch, "E793", {"start": v(169.06, 269.69) * mm, "end": v(168.98, 269.29) * mm});
            skLineSegment(sketch, "E794", {"start": v(168.98, 269.29) * mm, "end": v(168.88, 268.9) * mm});
            skLineSegment(sketch, "E795", {"start": v(168.88, 268.9) * mm, "end": v(168.77, 268.5) * mm});
            skLineSegment(sketch, "E796", {"start": v(168.77, 268.5) * mm, "end": v(168.65, 268.1) * mm});
            skLineSegment(sketch, "E797", {"start": v(168.65, 268.1) * mm, "end": v(168.53, 267.72) * mm});
            skLineSegment(sketch, "E798", {"start": v(168.53, 267.72) * mm, "end": v(168.39, 267.34) * mm});
            skLineSegment(sketch, "E799", {"start": v(168.39, 267.34) * mm, "end": v(168.24, 266.96) * mm});
            skLineSegment(sketch, "E800", {"start": v(168.24, 266.96) * mm, "end": v(168.09, 266.58) * mm});
            skLineSegment(sketch, "E801", {"start": v(168.09, 266.58) * mm, "end": v(167.92, 266.2) * mm});
            skLineSegment(sketch, "E802", {"start": v(167.92, 266.2) * mm, "end": v(167.74, 265.84) * mm});
            skLineSegment(sketch, "E803", {"start": v(167.74, 265.84) * mm, "end": v(167.56, 265.48) * mm});
            skLineSegment(sketch, "E804", {"start": v(167.56, 265.48) * mm, "end": v(167.36, 265.12) * mm});
            skLineSegment(sketch, "E805", {"start": v(167.36, 265.12) * mm, "end": v(167.16, 264.76) * mm});
            skLineSegment(sketch, "E806", {"start": v(167.16, 264.76) * mm, "end": v(166.95, 264.41) * mm});
            skLineSegment(sketch, "E807", {"start": v(166.95, 264.41) * mm, "end": v(166.73, 264.07) * mm});
            skLineSegment(sketch, "E808", {"start": v(166.73, 264.07) * mm, "end": v(166.5, 263.73) * mm});
            skLineSegment(sketch, "E809", {"start": v(166.5, 263.73) * mm, "end": v(166.26, 263.4) * mm});
            skLineSegment(sketch, "E810", {"start": v(166.26, 263.4) * mm, "end": v(166, 263.07) * mm});
            skLineSegment(sketch, "E811", {"start": v(166, 263.07) * mm, "end": v(165.75, 262.75) * mm});
            skLineSegment(sketch, "E812", {"start": v(165.75, 262.75) * mm, "end": v(165.49, 262.44) * mm});
            skLineSegment(sketch, "E813", {"start": v(165.49, 262.44) * mm, "end": v(165.21, 262.13) * mm});
            skLineSegment(sketch, "E814", {"start": v(165.21, 262.13) * mm, "end": v(164.93, 261.83) * mm});
            skLineSegment(sketch, "E815", {"start": v(164.93, 261.83) * mm, "end": v(164.64, 261.54) * mm});
            skLineSegment(sketch, "E816", {"start": v(164.64, 261.54) * mm, "end": v(164.34, 261.25) * mm});
            skLineSegment(sketch, "E817", {"start": v(164.34, 261.25) * mm, "end": v(163.93, 260.88) * mm});
            skLineSegment(sketch, "E818", {"start": v(163.93, 260.88) * mm, "end": v(163.51, 260.52) * mm});
            skLineSegment(sketch, "E819", {"start": v(163.51, 260.52) * mm, "end": v(163.09, 260.17) * mm});
            skLineSegment(sketch, "E820", {"start": v(163.09, 260.17) * mm, "end": v(162.65, 259.84) * mm});
            skLineSegment(sketch, "E821", {"start": v(162.65, 259.84) * mm, "end": v(162.21, 259.51) * mm});
            skLineSegment(sketch, "E822", {"start": v(162.21, 259.51) * mm, "end": v(161.76, 259.2) * mm});
            skLineSegment(sketch, "E823", {"start": v(161.76, 259.2) * mm, "end": v(161.3, 258.9) * mm});
            skLineSegment(sketch, "E824", {"start": v(161.3, 258.9) * mm, "end": v(160.84, 258.6) * mm});
            skLineSegment(sketch, "E825", {"start": v(160.84, 258.6) * mm, "end": v(160.37, 258.33) * mm});
            skLineSegment(sketch, "E826", {"start": v(160.37, 258.33) * mm, "end": v(159.9, 258.06) * mm});
            skLineSegment(sketch, "E827", {"start": v(159.9, 258.06) * mm, "end": v(159.42, 257.81) * mm});
            skLineSegment(sketch, "E828", {"start": v(159.42, 257.81) * mm, "end": v(158.93, 257.57) * mm});
            skLineSegment(sketch, "E829", {"start": v(158.93, 257.57) * mm, "end": v(158.44, 257.34) * mm});
            skLineSegment(sketch, "E830", {"start": v(158.44, 257.34) * mm, "end": v(157.94, 257.12) * mm});
            skLineSegment(sketch, "E831", {"start": v(157.94, 257.12) * mm, "end": v(157.43, 256.92) * mm});
            skLineSegment(sketch, "E832", {"start": v(157.43, 256.92) * mm, "end": v(156.92, 256.72) * mm});
            skLineSegment(sketch, "E833", {"start": v(156.92, 256.72) * mm, "end": v(156.41, 256.54) * mm});
            skLineSegment(sketch, "E834", {"start": v(156.41, 256.54) * mm, "end": v(155.9, 256.38) * mm});
            skLineSegment(sketch, "E835", {"start": v(155.9, 256.38) * mm, "end": v(155.37, 256.22) * mm});
            skLineSegment(sketch, "E836", {"start": v(155.37, 256.22) * mm, "end": v(154.85, 256.08) * mm});
            skLineSegment(sketch, "E837", {"start": v(154.85, 256.08) * mm, "end": v(154.32, 255.95) * mm});
            skLineSegment(sketch, "E838", {"start": v(154.32, 255.95) * mm, "end": v(153.78, 255.84) * mm});
            skLineSegment(sketch, "E839", {"start": v(153.78, 255.84) * mm, "end": v(153.25, 255.73) * mm});
            skLineSegment(sketch, "E840", {"start": v(153.25, 255.73) * mm, "end": v(152.71, 255.64) * mm});
            skLineSegment(sketch, "E841", {"start": v(152.71, 255.64) * mm, "end": v(152.17, 255.57) * mm});
            skLineSegment(sketch, "E842", {"start": v(152.17, 255.57) * mm, "end": v(151.63, 255.5) * mm});
            skLineSegment(sketch, "E843", {"start": v(151.63, 255.5) * mm, "end": v(151.08, 255.46) * mm});
            skLineSegment(sketch, "E844", {"start": v(151.08, 255.46) * mm, "end": v(150.53, 255.42) * mm});
            skLineSegment(sketch, "E845", {"start": v(150.53, 255.42) * mm, "end": v(149.99, 255.4) * mm});
            skLineSegment(sketch, "E846", {"start": v(149.99, 255.4) * mm, "end": v(149.44, 255.4) * mm});
            skLineSegment(sketch, "E847", {"start": v(149.44, 255.4) * mm, "end": v(148.88, 255.4) * mm});
            skLineSegment(sketch, "E848", {"start": v(148.88, 255.4) * mm, "end": v(148.33, 255.42) * mm});
            skLineSegment(sketch, "E849", {"start": v(148.33, 255.42) * mm, "end": v(147.82, 255.4) * mm});
            skLineSegment(sketch, "E850", {"start": v(147.82, 255.4) * mm, "end": v(147.3, 255.41) * mm});
            skLineSegment(sketch, "E851", {"start": v(147.3, 255.41) * mm, "end": v(146.8, 255.43) * mm});
            skLineSegment(sketch, "E852", {"start": v(146.8, 255.43) * mm, "end": v(146.28, 255.46) * mm});
            skLineSegment(sketch, "E853", {"start": v(146.28, 255.46) * mm, "end": v(145.77, 255.5) * mm});
            skLineSegment(sketch, "E854", {"start": v(145.77, 255.5) * mm, "end": v(145.26, 255.56) * mm});
            skLineSegment(sketch, "E855", {"start": v(145.26, 255.56) * mm, "end": v(144.76, 255.63) * mm});
            skLineSegment(sketch, "E856", {"start": v(144.76, 255.63) * mm, "end": v(144.26, 255.71) * mm});
            skLineSegment(sketch, "E857", {"start": v(144.26, 255.71) * mm, "end": v(143.76, 255.8) * mm});
            skLineSegment(sketch, "E858", {"start": v(143.76, 255.8) * mm, "end": v(143.26, 255.9) * mm});
            skLineSegment(sketch, "E859", {"start": v(143.26, 255.9) * mm, "end": v(142.76, 256.03) * mm});
            skLineSegment(sketch, "E860", {"start": v(142.76, 256.03) * mm, "end": v(142.27, 256.16) * mm});
            skLineSegment(sketch, "E861", {"start": v(142.27, 256.16) * mm, "end": v(141.79, 256.3) * mm});
            skLineSegment(sketch, "E862", {"start": v(141.79, 256.3) * mm, "end": v(141.3, 256.46) * mm});
            skLineSegment(sketch, "E863", {"start": v(141.3, 256.46) * mm, "end": v(140.82, 256.62) * mm});
            skLineSegment(sketch, "E864", {"start": v(140.82, 256.62) * mm, "end": v(140.35, 256.8) * mm});
            skLineSegment(sketch, "E865", {"start": v(140.35, 256.8) * mm, "end": v(139.88, 256.99) * mm});
            skLineSegment(sketch, "E866", {"start": v(139.88, 256.99) * mm, "end": v(139.41, 257.2) * mm});
            skLineSegment(sketch, "E867", {"start": v(139.41, 257.2) * mm, "end": v(138.95, 257.4) * mm});
            skLineSegment(sketch, "E868", {"start": v(138.95, 257.4) * mm, "end": v(138.5, 257.63) * mm});
            skLineSegment(sketch, "E869", {"start": v(138.5, 257.63) * mm, "end": v(138.05, 257.86) * mm});
            skLineSegment(sketch, "E870", {"start": v(138.05, 257.86) * mm, "end": v(137.6, 258.11) * mm});
            skLineSegment(sketch, "E871", {"start": v(137.6, 258.11) * mm, "end": v(137.16, 258.37) * mm});
            skLineSegment(sketch, "E872", {"start": v(137.16, 258.37) * mm, "end": v(136.73, 258.64) * mm});
            skLineSegment(sketch, "E873", {"start": v(136.73, 258.64) * mm, "end": v(136.3, 258.92) * mm});
            skLineSegment(sketch, "E874", {"start": v(136.3, 258.92) * mm, "end": v(135.89, 259.2) * mm});
            skLineSegment(sketch, "E875", {"start": v(135.89, 259.2) * mm, "end": v(135.48, 259.51) * mm});
            skLineSegment(sketch, "E876", {"start": v(135.48, 259.51) * mm, "end": v(135.07, 259.82) * mm});
            skLineSegment(sketch, "E877", {"start": v(135.07, 259.82) * mm, "end": v(134.68, 260.15) * mm});
            skLineSegment(sketch, "E878", {"start": v(134.68, 260.15) * mm, "end": v(134.29, 260.48) * mm});
            skLineSegment(sketch, "E879", {"start": v(134.29, 260.48) * mm, "end": v(133.9, 260.82) * mm});
            skLineSegment(sketch, "E880", {"start": v(133.9, 260.82) * mm, "end": v(133.53, 261.18) * mm});
            skLineSegment(sketch, "E881", {"start": v(133.53, 261.18) * mm, "end": v(133.24, 261.47) * mm});
            skLineSegment(sketch, "E882", {"start": v(133.24, 261.47) * mm, "end": v(132.96, 261.77) * mm});
            skLineSegment(sketch, "E883", {"start": v(132.96, 261.77) * mm, "end": v(132.68, 262.08) * mm});
            skLineSegment(sketch, "E884", {"start": v(132.68, 262.08) * mm, "end": v(132.41, 262.4) * mm});
            skLineSegment(sketch, "E885", {"start": v(132.41, 262.4) * mm, "end": v(132.16, 262.71) * mm});
            skLineSegment(sketch, "E886", {"start": v(132.16, 262.71) * mm, "end": v(131.9, 263.04) * mm});
            skLineSegment(sketch, "E887", {"start": v(131.9, 263.04) * mm, "end": v(131.66, 263.37) * mm});
            skLineSegment(sketch, "E888", {"start": v(131.66, 263.37) * mm, "end": v(131.43, 263.7) * mm});
            skLineSegment(sketch, "E889", {"start": v(131.43, 263.7) * mm, "end": v(131.2, 264.05) * mm});
            skLineSegment(sketch, "E890", {"start": v(131.2, 264.05) * mm, "end": v(131, 264.4) * mm});
            skLineSegment(sketch, "E891", {"start": v(131, 264.4) * mm, "end": v(130.79, 264.75) * mm});
            skLineSegment(sketch, "E892", {"start": v(130.79, 264.75) * mm, "end": v(130.59, 265.1) * mm});
            skLineSegment(sketch, "E893", {"start": v(130.59, 265.1) * mm, "end": v(130.4, 265.47) * mm});
            skLineSegment(sketch, "E894", {"start": v(130.4, 265.47) * mm, "end": v(130.22, 265.83) * mm});
            skLineSegment(sketch, "E895", {"start": v(130.22, 265.83) * mm, "end": v(130.05, 266.2) * mm});
            skLineSegment(sketch, "E896", {"start": v(130.05, 266.2) * mm, "end": v(129.89, 266.58) * mm});
            skLineSegment(sketch, "E897", {"start": v(129.89, 266.58) * mm, "end": v(129.74, 266.96) * mm});
            skLineSegment(sketch, "E898", {"start": v(129.74, 266.96) * mm, "end": v(129.6, 267.34) * mm});
            skLineSegment(sketch, "E899", {"start": v(129.6, 267.34) * mm, "end": v(129.46, 267.72) * mm});
            skLineSegment(sketch, "E900", {"start": v(129.46, 267.72) * mm, "end": v(129.34, 268.11) * mm});
            skLineSegment(sketch, "E901", {"start": v(129.34, 268.11) * mm, "end": v(129.23, 268.5) * mm});
            skLineSegment(sketch, "E902", {"start": v(129.23, 268.5) * mm, "end": v(129.12, 268.9) * mm});
            skLineSegment(sketch, "E903", {"start": v(129.12, 268.9) * mm, "end": v(129.03, 269.3) * mm});
            skLineSegment(sketch, "E904", {"start": v(129.03, 269.3) * mm, "end": v(128.94, 269.7) * mm});
            skLineSegment(sketch, "E905", {"start": v(128.94, 269.7) * mm, "end": v(128.87, 270.1) * mm});
            skLineSegment(sketch, "E906", {"start": v(128.87, 270.1) * mm, "end": v(128.8, 270.5) * mm});
            skLineSegment(sketch, "E907", {"start": v(128.8, 270.5) * mm, "end": v(128.75, 270.91) * mm});
            skLineSegment(sketch, "E908", {"start": v(128.75, 270.91) * mm, "end": v(128.7, 271.32) * mm});
            skLineSegment(sketch, "E909", {"start": v(128.7, 271.32) * mm, "end": v(128.67, 271.73) * mm});
            skLineSegment(sketch, "E910", {"start": v(128.67, 271.73) * mm, "end": v(128.65, 272.14) * mm});
            skLineSegment(sketch, "E911", {"start": v(128.65, 272.14) * mm, "end": v(128.63, 272.55) * mm});
            skLineSegment(sketch, "E912", {"start": v(128.63, 272.55) * mm, "end": v(128.63, 272.97) * mm});
            skLineSegment(sketch, "E913", {"start": v(128.63, 228.72) * mm, "end": v(128.63, 229.14) * mm});
            skLineSegment(sketch, "E914", {"start": v(128.63, 229.14) * mm, "end": v(128.64, 229.56) * mm});
            skLineSegment(sketch, "E915", {"start": v(128.64, 229.56) * mm, "end": v(128.65, 229.98) * mm});
            skLineSegment(sketch, "E916", {"start": v(128.65, 229.98) * mm, "end": v(128.68, 230.4) * mm});
            skLineSegment(sketch, "E917", {"start": v(128.68, 230.4) * mm, "end": v(128.72, 230.81) * mm});
            skLineSegment(sketch, "E918", {"start": v(128.72, 230.81) * mm, "end": v(128.77, 231.23) * mm});
            skLineSegment(sketch, "E919", {"start": v(128.77, 231.23) * mm, "end": v(128.83, 231.64) * mm});
            skLineSegment(sketch, "E920", {"start": v(128.83, 231.64) * mm, "end": v(128.9, 232.05) * mm});
            skLineSegment(sketch, "E921", {"start": v(128.9, 232.05) * mm, "end": v(128.98, 232.45) * mm});
            skLineSegment(sketch, "E922", {"start": v(128.98, 232.45) * mm, "end": v(129.07, 232.86) * mm});
            skLineSegment(sketch, "E923", {"start": v(129.07, 232.86) * mm, "end": v(129.17, 233.26) * mm});
            skLineSegment(sketch, "E924", {"start": v(129.17, 233.26) * mm, "end": v(129.28, 233.66) * mm});
            skLineSegment(sketch, "E925", {"start": v(129.28, 233.66) * mm, "end": v(129.4, 234.06) * mm});
            skLineSegment(sketch, "E926", {"start": v(129.4, 234.06) * mm, "end": v(129.52, 234.45) * mm});
            skLineSegment(sketch, "E927", {"start": v(129.52, 234.45) * mm, "end": v(129.66, 234.84) * mm});
            skLineSegment(sketch, "E928", {"start": v(129.66, 234.84) * mm, "end": v(129.81, 235.23) * mm});
            skLineSegment(sketch, "E929", {"start": v(129.81, 235.23) * mm, "end": v(129.97, 235.6) * mm});
            skLineSegment(sketch, "E930", {"start": v(129.97, 235.6) * mm, "end": v(130.14, 235.99) * mm});
            skLineSegment(sketch, "E931", {"start": v(130.14, 235.99) * mm, "end": v(130.31, 236.36) * mm});
            skLineSegment(sketch, "E932", {"start": v(130.31, 236.36) * mm, "end": v(130.5, 236.73) * mm});
            skLineSegment(sketch, "E933", {"start": v(130.5, 236.73) * mm, "end": v(130.7, 237.1) * mm});
            skLineSegment(sketch, "E934", {"start": v(130.7, 237.1) * mm, "end": v(130.9, 237.46) * mm});
            skLineSegment(sketch, "E935", {"start": v(130.9, 237.46) * mm, "end": v(131.11, 237.81) * mm});
            skLineSegment(sketch, "E936", {"start": v(131.11, 237.81) * mm, "end": v(131.33, 238.16) * mm});
            skLineSegment(sketch, "E937", {"start": v(131.33, 238.16) * mm, "end": v(131.57, 238.5) * mm});
            skLineSegment(sketch, "E938", {"start": v(131.57, 238.5) * mm, "end": v(131.8, 238.85) * mm});
            skLineSegment(sketch, "E939", {"start": v(131.8, 238.85) * mm, "end": v(132.05, 239.18) * mm});
            skLineSegment(sketch, "E940", {"start": v(132.05, 239.18) * mm, "end": v(132.31, 239.5) * mm});
            skLineSegment(sketch, "E941", {"start": v(132.31, 239.5) * mm, "end": v(132.58, 239.83) * mm});
            skLineSegment(sketch, "E942", {"start": v(132.58, 239.83) * mm, "end": v(132.85, 240.15) * mm});
            skLineSegment(sketch, "E943", {"start": v(132.85, 240.15) * mm, "end": v(133.13, 240.46) * mm});
            skLineSegment(sketch, "E944", {"start": v(133.13, 240.46) * mm, "end": v(133.43, 240.76) * mm});
            skLineSegment(sketch, "E945", {"start": v(133.43, 240.76) * mm, "end": v(133.8, 241.1) * mm});
            skLineSegment(sketch, "E946", {"start": v(133.8, 241.1) * mm, "end": v(134.2, 241.45) * mm});
            skLineSegment(sketch, "E947", {"start": v(134.2, 241.45) * mm, "end": v(134.6, 241.78) * mm});
            skLineSegment(sketch, "E948", {"start": v(134.6, 241.78) * mm, "end": v(135, 242.1) * mm});
            skLineSegment(sketch, "E949", {"start": v(135, 242.1) * mm, "end": v(135.4, 242.4) * mm});
            skLineSegment(sketch, "E950", {"start": v(135.4, 242.4) * mm, "end": v(135.82, 242.7) * mm});
            skLineSegment(sketch, "E951", {"start": v(135.82, 242.7) * mm, "end": v(136.25, 242.99) * mm});
            skLineSegment(sketch, "E952", {"start": v(136.25, 242.99) * mm, "end": v(136.68, 243.26) * mm});
            skLineSegment(sketch, "E953", {"start": v(136.68, 243.26) * mm, "end": v(137.11, 243.53) * mm});
            skLineSegment(sketch, "E954", {"start": v(137.11, 243.53) * mm, "end": v(137.56, 243.78) * mm});
            skLineSegment(sketch, "E955", {"start": v(137.56, 243.78) * mm, "end": v(138, 244.02) * mm});
            skLineSegment(sketch, "E956", {"start": v(138, 244.02) * mm, "end": v(138.46, 244.25) * mm});
            skLineSegment(sketch, "E957", {"start": v(138.46, 244.25) * mm, "end": v(138.92, 244.47) * mm});
            skLineSegment(sketch, "E958", {"start": v(138.92, 244.47) * mm, "end": v(139.38, 244.68) * mm});
            skLineSegment(sketch, "E959", {"start": v(139.38, 244.68) * mm, "end": v(139.85, 244.88) * mm});
            skLineSegment(sketch, "E960", {"start": v(139.85, 244.88) * mm, "end": v(140.33, 245.07) * mm});
            skLineSegment(sketch, "E961", {"start": v(140.33, 245.07) * mm, "end": v(140.8, 245.24) * mm});
            skLineSegment(sketch, "E962", {"start": v(140.8, 245.24) * mm, "end": v(141.29, 245.4) * mm});
            skLineSegment(sketch, "E963", {"start": v(141.29, 245.4) * mm, "end": v(141.78, 245.55) * mm});
            skLineSegment(sketch, "E964", {"start": v(141.78, 245.55) * mm, "end": v(142.27, 245.69) * mm});
            skLineSegment(sketch, "E965", {"start": v(142.27, 245.69) * mm, "end": v(142.76, 245.82) * mm});
            skLineSegment(sketch, "E966", {"start": v(142.76, 245.82) * mm, "end": v(143.26, 245.93) * mm});
            skLineSegment(sketch, "E967", {"start": v(143.26, 245.93) * mm, "end": v(143.76, 246.03) * mm});
            skLineSegment(sketch, "E968", {"start": v(143.76, 246.03) * mm, "end": v(144.26, 246.12) * mm});
            skLineSegment(sketch, "E969", {"start": v(144.26, 246.12) * mm, "end": v(144.77, 246.2) * mm});
            skLineSegment(sketch, "E970", {"start": v(144.77, 246.2) * mm, "end": v(145.27, 246.26) * mm});
            skLineSegment(sketch, "E971", {"start": v(145.27, 246.26) * mm, "end": v(145.78, 246.32) * mm});
            skLineSegment(sketch, "E972", {"start": v(145.78, 246.32) * mm, "end": v(146.3, 246.35) * mm});
            skLineSegment(sketch, "E973", {"start": v(146.3, 246.35) * mm, "end": v(146.8, 246.38) * mm});
            skLineSegment(sketch, "E974", {"start": v(146.8, 246.38) * mm, "end": v(147.32, 246.4) * mm});
            skLineSegment(sketch, "E975", {"start": v(147.32, 246.4) * mm, "end": v(147.84, 246.4) * mm});
            skLineSegment(sketch, "E976", {"start": v(147.84, 246.4) * mm, "end": v(148.36, 246.38) * mm});
            skLineSegment(sketch, "E977", {"start": v(148.36, 246.38) * mm, "end": v(148.92, 246.4) * mm});
            skLineSegment(sketch, "E978", {"start": v(148.92, 246.4) * mm, "end": v(149.48, 246.4) * mm});
            skLineSegment(sketch, "E979", {"start": v(149.48, 246.4) * mm, "end": v(150.04, 246.4) * mm});
            skLineSegment(sketch, "E980", {"start": v(150.04, 246.4) * mm, "end": v(150.6, 246.36) * mm});
            skLineSegment(sketch, "E981", {"start": v(150.6, 246.36) * mm, "end": v(151.15, 246.32) * mm});
            skLineSegment(sketch, "E982", {"start": v(151.15, 246.32) * mm, "end": v(151.7, 246.27) * mm});
            skLineSegment(sketch, "E983", {"start": v(151.7, 246.27) * mm, "end": v(152.26, 246.2) * mm});
            skLineSegment(sketch, "E984", {"start": v(152.26, 246.2) * mm, "end": v(152.8, 246.12) * mm});
            skLineSegment(sketch, "E985", {"start": v(152.8, 246.12) * mm, "end": v(153.35, 246.02) * mm});
            skLineSegment(sketch, "E986", {"start": v(153.35, 246.02) * mm, "end": v(153.9, 245.91) * mm});
            skLineSegment(sketch, "E987", {"start": v(153.9, 245.91) * mm, "end": v(154.44, 245.8) * mm});
            skLineSegment(sketch, "E988", {"start": v(154.44, 245.8) * mm, "end": v(154.97, 245.66) * mm});
            skLineSegment(sketch, "E989", {"start": v(154.97, 245.66) * mm, "end": v(155.5, 245.5) * mm});
            skLineSegment(sketch, "E990", {"start": v(155.5, 245.5) * mm, "end": v(156.03, 245.34) * mm});
            skLineSegment(sketch, "E991", {"start": v(156.03, 245.34) * mm, "end": v(156.56, 245.17) * mm});
            skLineSegment(sketch, "E992", {"start": v(156.56, 245.17) * mm, "end": v(157.08, 244.98) * mm});
            skLineSegment(sketch, "E993", {"start": v(157.08, 244.98) * mm, "end": v(157.6, 244.78) * mm});
            skLineSegment(sketch, "E994", {"start": v(157.6, 244.78) * mm, "end": v(158.1, 244.57) * mm});
            skLineSegment(sketch, "E995", {"start": v(158.1, 244.57) * mm, "end": v(158.6, 244.34) * mm});
            skLineSegment(sketch, "E996", {"start": v(158.6, 244.34) * mm, "end": v(159.1, 244.1) * mm});
            skLineSegment(sketch, "E997", {"start": v(159.1, 244.1) * mm, "end": v(159.6, 243.85) * mm});
            skLineSegment(sketch, "E998", {"start": v(159.6, 243.85) * mm, "end": v(160.09, 243.59) * mm});
            skLineSegment(sketch, "E999", {"start": v(160.09, 243.59) * mm, "end": v(160.57, 243.31) * mm});
            skLineSegment(sketch, "E1000", {"start": v(160.57, 243.31) * mm, "end": v(161.04, 243.02) * mm});
            skLineSegment(sketch, "E1001", {"start": v(161.04, 243.02) * mm, "end": v(161.5, 242.72) * mm});
            skLineSegment(sketch, "E1002", {"start": v(161.5, 242.72) * mm, "end": v(161.97, 242.41) * mm});
            skLineSegment(sketch, "E1003", {"start": v(161.97, 242.41) * mm, "end": v(162.42, 242.09) * mm});
            skLineSegment(sketch, "E1004", {"start": v(162.42, 242.09) * mm, "end": v(162.87, 241.75) * mm});
            skLineSegment(sketch, "E1005", {"start": v(162.87, 241.75) * mm, "end": v(163.3, 241.4) * mm});
            skLineSegment(sketch, "E1006", {"start": v(163.3, 241.4) * mm, "end": v(163.73, 241.05) * mm});
            skLineSegment(sketch, "E1007", {"start": v(163.73, 241.05) * mm, "end": v(164.15, 240.68) * mm});
            skLineSegment(sketch, "E1008", {"start": v(164.15, 240.68) * mm, "end": v(164.56, 240.3) * mm});
            skLineSegment(sketch, "E1009", {"start": v(164.56, 240.3) * mm, "end": v(164.86, 240) * mm});
            skLineSegment(sketch, "E1010", {"start": v(164.86, 240) * mm, "end": v(165.14, 239.72) * mm});
            skLineSegment(sketch, "E1011", {"start": v(165.14, 239.72) * mm, "end": v(165.41, 239.42) * mm});
            skLineSegment(sketch, "E1012", {"start": v(165.41, 239.42) * mm, "end": v(165.68, 239.11) * mm});
            skLineSegment(sketch, "E1013", {"start": v(165.68, 239.11) * mm, "end": v(165.94, 238.8) * mm});
            skLineSegment(sketch, "E1014", {"start": v(165.94, 238.8) * mm, "end": v(166.18, 238.48) * mm});
            skLineSegment(sketch, "E1015", {"start": v(166.18, 238.48) * mm, "end": v(166.42, 238.16) * mm});
            skLineSegment(sketch, "E1016", {"start": v(166.42, 238.16) * mm, "end": v(166.66, 237.83) * mm});
            skLineSegment(sketch, "E1017", {"start": v(166.66, 237.83) * mm, "end": v(166.88, 237.5) * mm});
            skLineSegment(sketch, "E1018", {"start": v(166.88, 237.5) * mm, "end": v(167.1, 237.15) * mm});
            skLineSegment(sketch, "E1019", {"start": v(167.1, 237.15) * mm, "end": v(167.3, 236.8) * mm});
            skLineSegment(sketch, "E1020", {"start": v(167.3, 236.8) * mm, "end": v(167.5, 236.45) * mm});
            skLineSegment(sketch, "E1021", {"start": v(167.5, 236.45) * mm, "end": v(167.68, 236.1) * mm});
            skLineSegment(sketch, "E1022", {"start": v(167.68, 236.1) * mm, "end": v(167.86, 235.74) * mm});
            skLineSegment(sketch, "E1023", {"start": v(167.86, 235.74) * mm, "end": v(168.03, 235.38) * mm});
            skLineSegment(sketch, "E1024", {"start": v(168.03, 235.38) * mm, "end": v(168.19, 235) * mm});
            skLineSegment(sketch, "E1025", {"start": v(168.19, 235) * mm, "end": v(168.33, 234.64) * mm});
            skLineSegment(sketch, "E1026", {"start": v(168.33, 234.64) * mm, "end": v(168.47, 234.26) * mm});
            skLineSegment(sketch, "E1027", {"start": v(168.47, 234.26) * mm, "end": v(168.6, 233.88) * mm});
            skLineSegment(sketch, "E1028", {"start": v(168.6, 233.88) * mm, "end": v(168.73, 233.5) * mm});
            skLineSegment(sketch, "E1029", {"start": v(168.73, 233.5) * mm, "end": v(168.84, 233.11) * mm});
            skLineSegment(sketch, "E1030", {"start": v(168.84, 233.11) * mm, "end": v(168.94, 232.72) * mm});
            skLineSegment(sketch, "E1031", {"start": v(168.94, 232.72) * mm, "end": v(169.03, 232.33) * mm});
            skLineSegment(sketch, "E1032", {"start": v(169.03, 232.33) * mm, "end": v(169.11, 231.94) * mm});
            skLineSegment(sketch, "E1033", {"start": v(169.11, 231.94) * mm, "end": v(169.18, 231.54) * mm});
            skLineSegment(sketch, "E1034", {"start": v(169.18, 231.54) * mm, "end": v(169.24, 231.14) * mm});
            skLineSegment(sketch, "E1035", {"start": v(169.24, 231.14) * mm, "end": v(169.3, 230.74) * mm});
            skLineSegment(sketch, "E1036", {"start": v(169.3, 230.74) * mm, "end": v(169.33, 230.34) * mm});
            skLineSegment(sketch, "E1037", {"start": v(169.33, 230.34) * mm, "end": v(169.36, 229.93) * mm});
            skLineSegment(sketch, "E1038", {"start": v(169.36, 229.93) * mm, "end": v(169.38, 229.53) * mm});
            skLineSegment(sketch, "E1039", {"start": v(169.38, 229.53) * mm, "end": v(169.4, 229.12) * mm});
            skLineSegment(sketch, "E1040", {"start": v(169.4, 229.12) * mm, "end": v(169.4, 228.72) * mm});
            skLineSegment(sketch, "E1041", {"start": v(169.4, 228.72) * mm, "end": v(169.39, 228.3) * mm});
            skLineSegment(sketch, "E1042", {"start": v(169.39, 228.3) * mm, "end": v(169.37, 227.89) * mm});
            skLineSegment(sketch, "E1043", {"start": v(169.37, 227.89) * mm, "end": v(169.35, 227.48) * mm});
            skLineSegment(sketch, "E1044", {"start": v(169.35, 227.48) * mm, "end": v(169.31, 227.07) * mm});
            skLineSegment(sketch, "E1045", {"start": v(169.31, 227.07) * mm, "end": v(169.27, 226.66) * mm});
            skLineSegment(sketch, "E1046", {"start": v(169.27, 226.66) * mm, "end": v(169.2, 226.25) * mm});
            skLineSegment(sketch, "E1047", {"start": v(169.2, 226.25) * mm, "end": v(169.14, 225.85) * mm});
            skLineSegment(sketch, "E1048", {"start": v(169.14, 225.85) * mm, "end": v(169.06, 225.44) * mm});
            skLineSegment(sketch, "E1049", {"start": v(169.06, 225.44) * mm, "end": v(168.98, 225.04) * mm});
            skLineSegment(sketch, "E1050", {"start": v(168.98, 225.04) * mm, "end": v(168.88, 224.65) * mm});
            skLineSegment(sketch, "E1051", {"start": v(168.88, 224.65) * mm, "end": v(168.77, 224.25) * mm});
            skLineSegment(sketch, "E1052", {"start": v(168.77, 224.25) * mm, "end": v(168.65, 223.86) * mm});
            skLineSegment(sketch, "E1053", {"start": v(168.65, 223.86) * mm, "end": v(168.53, 223.48) * mm});
            skLineSegment(sketch, "E1054", {"start": v(168.53, 223.48) * mm, "end": v(168.39, 223.1) * mm});
            skLineSegment(sketch, "E1055", {"start": v(168.39, 223.1) * mm, "end": v(168.24, 222.71) * mm});
            skLineSegment(sketch, "E1056", {"start": v(168.24, 222.71) * mm, "end": v(168.09, 222.33) * mm});
            skLineSegment(sketch, "E1057", {"start": v(168.09, 222.33) * mm, "end": v(167.92, 221.96) * mm});
            skLineSegment(sketch, "E1058", {"start": v(167.92, 221.96) * mm, "end": v(167.74, 221.6) * mm});
            skLineSegment(sketch, "E1059", {"start": v(167.74, 221.6) * mm, "end": v(167.56, 221.23) * mm});
            skLineSegment(sketch, "E1060", {"start": v(167.56, 221.23) * mm, "end": v(167.36, 220.87) * mm});
            skLineSegment(sketch, "E1061", {"start": v(167.36, 220.87) * mm, "end": v(167.16, 220.52) * mm});
            skLineSegment(sketch, "E1062", {"start": v(167.16, 220.52) * mm, "end": v(166.95, 220.17) * mm});
            skLineSegment(sketch, "E1063", {"start": v(166.95, 220.17) * mm, "end": v(166.73, 219.83) * mm});
            skLineSegment(sketch, "E1064", {"start": v(166.73, 219.83) * mm, "end": v(166.5, 219.49) * mm});
            skLineSegment(sketch, "E1065", {"start": v(166.5, 219.49) * mm, "end": v(166.26, 219.16) * mm});
            skLineSegment(sketch, "E1066", {"start": v(166.26, 219.16) * mm, "end": v(166, 218.83) * mm});
            skLineSegment(sketch, "E1067", {"start": v(166, 218.83) * mm, "end": v(165.75, 218.5) * mm});
            skLineSegment(sketch, "E1068", {"start": v(165.75, 218.5) * mm, "end": v(165.49, 218.2) * mm});
            skLineSegment(sketch, "E1069", {"start": v(165.49, 218.2) * mm, "end": v(165.21, 217.89) * mm});
            skLineSegment(sketch, "E1070", {"start": v(165.21, 217.89) * mm, "end": v(164.93, 217.59) * mm});
            skLineSegment(sketch, "E1071", {"start": v(164.93, 217.59) * mm, "end": v(164.64, 217.3) * mm});
            skLineSegment(sketch, "E1072", {"start": v(164.64, 217.3) * mm, "end": v(164.34, 217) * mm});
            skLineSegment(sketch, "E1073", {"start": v(164.34, 217) * mm, "end": v(163.93, 216.64) * mm});
            skLineSegment(sketch, "E1074", {"start": v(163.93, 216.64) * mm, "end": v(163.51, 216.28) * mm});
            skLineSegment(sketch, "E1075", {"start": v(163.51, 216.28) * mm, "end": v(163.09, 215.93) * mm});
            skLineSegment(sketch, "E1076", {"start": v(163.09, 215.93) * mm, "end": v(162.65, 215.6) * mm});
            skLineSegment(sketch, "E1077", {"start": v(162.65, 215.6) * mm, "end": v(162.21, 215.27) * mm});
            skLineSegment(sketch, "E1078", {"start": v(162.21, 215.27) * mm, "end": v(161.76, 214.95) * mm});
            skLineSegment(sketch, "E1079", {"start": v(161.76, 214.95) * mm, "end": v(161.3, 214.65) * mm});
            skLineSegment(sketch, "E1080", {"start": v(161.3, 214.65) * mm, "end": v(160.84, 214.36) * mm});
            skLineSegment(sketch, "E1081", {"start": v(160.84, 214.36) * mm, "end": v(160.37, 214.09) * mm});
            skLineSegment(sketch, "E1082", {"start": v(160.37, 214.09) * mm, "end": v(159.9, 213.82) * mm});
            skLineSegment(sketch, "E1083", {"start": v(159.9, 213.82) * mm, "end": v(159.42, 213.57) * mm});
            skLineSegment(sketch, "E1084", {"start": v(159.42, 213.57) * mm, "end": v(158.93, 213.32) * mm});
            skLineSegment(sketch, "E1085", {"start": v(158.93, 213.32) * mm, "end": v(158.44, 213.1) * mm});
            skLineSegment(sketch, "E1086", {"start": v(158.44, 213.1) * mm, "end": v(157.94, 212.88) * mm});
            skLineSegment(sketch, "E1087", {"start": v(157.94, 212.88) * mm, "end": v(157.43, 212.67) * mm});
            skLineSegment(sketch, "E1088", {"start": v(157.43, 212.67) * mm, "end": v(156.92, 212.48) * mm});
            skLineSegment(sketch, "E1089", {"start": v(156.92, 212.48) * mm, "end": v(156.41, 212.3) * mm});
            skLineSegment(sketch, "E1090", {"start": v(156.41, 212.3) * mm, "end": v(155.9, 212.13) * mm});
            skLineSegment(sketch, "E1091", {"start": v(155.9, 212.13) * mm, "end": v(155.37, 211.98) * mm});
            skLineSegment(sketch, "E1092", {"start": v(155.37, 211.98) * mm, "end": v(154.85, 211.84) * mm});
            skLineSegment(sketch, "E1093", {"start": v(154.85, 211.84) * mm, "end": v(154.32, 211.7) * mm});
            skLineSegment(sketch, "E1094", {"start": v(154.32, 211.7) * mm, "end": v(153.78, 211.6) * mm});
            skLineSegment(sketch, "E1095", {"start": v(153.78, 211.6) * mm, "end": v(153.25, 211.49) * mm});
            skLineSegment(sketch, "E1096", {"start": v(153.25, 211.49) * mm, "end": v(152.71, 211.4) * mm});
            skLineSegment(sketch, "E1097", {"start": v(152.71, 211.4) * mm, "end": v(152.17, 211.32) * mm});
            skLineSegment(sketch, "E1098", {"start": v(152.17, 211.32) * mm, "end": v(151.63, 211.26) * mm});
            skLineSegment(sketch, "E1099", {"start": v(151.63, 211.26) * mm, "end": v(151.08, 211.21) * mm});
            skLineSegment(sketch, "E1100", {"start": v(151.08, 211.21) * mm, "end": v(150.53, 211.18) * mm});
            skLineSegment(sketch, "E1101", {"start": v(150.53, 211.18) * mm, "end": v(149.99, 211.15) * mm});
            skLineSegment(sketch, "E1102", {"start": v(149.99, 211.15) * mm, "end": v(149.44, 211.15) * mm});
            skLineSegment(sketch, "E1103", {"start": v(149.44, 211.15) * mm, "end": v(148.88, 211.15) * mm});
            skLineSegment(sketch, "E1104", {"start": v(148.88, 211.15) * mm, "end": v(148.33, 211.17) * mm});
            skLineSegment(sketch, "E1105", {"start": v(148.33, 211.17) * mm, "end": v(147.82, 211.16) * mm});
            skLineSegment(sketch, "E1106", {"start": v(147.82, 211.16) * mm, "end": v(147.3, 211.17) * mm});
            skLineSegment(sketch, "E1107", {"start": v(147.3, 211.17) * mm, "end": v(146.8, 211.19) * mm});
            skLineSegment(sketch, "E1108", {"start": v(146.8, 211.19) * mm, "end": v(146.28, 211.22) * mm});
            skLineSegment(sketch, "E1109", {"start": v(146.28, 211.22) * mm, "end": v(145.77, 211.26) * mm});
            skLineSegment(sketch, "E1110", {"start": v(145.77, 211.26) * mm, "end": v(145.26, 211.32) * mm});
            skLineSegment(sketch, "E1111", {"start": v(145.26, 211.32) * mm, "end": v(144.76, 211.38) * mm});
            skLineSegment(sketch, "E1112", {"start": v(144.76, 211.38) * mm, "end": v(144.26, 211.46) * mm});
            skLineSegment(sketch, "E1113", {"start": v(144.26, 211.46) * mm, "end": v(143.76, 211.56) * mm});
            skLineSegment(sketch, "E1114", {"start": v(143.76, 211.56) * mm, "end": v(143.26, 211.66) * mm});
            skLineSegment(sketch, "E1115", {"start": v(143.26, 211.66) * mm, "end": v(142.76, 211.78) * mm});
            skLineSegment(sketch, "E1116", {"start": v(142.76, 211.78) * mm, "end": v(142.27, 211.91) * mm});
            skLineSegment(sketch, "E1117", {"start": v(142.27, 211.91) * mm, "end": v(141.79, 212.06) * mm});
            skLineSegment(sketch, "E1118", {"start": v(141.79, 212.06) * mm, "end": v(141.3, 212.21) * mm});
            skLineSegment(sketch, "E1119", {"start": v(141.3, 212.21) * mm, "end": v(140.82, 212.38) * mm});
            skLineSegment(sketch, "E1120", {"start": v(140.82, 212.38) * mm, "end": v(140.35, 212.55) * mm});
            skLineSegment(sketch, "E1121", {"start": v(140.35, 212.55) * mm, "end": v(139.88, 212.74) * mm});
            skLineSegment(sketch, "E1122", {"start": v(139.88, 212.74) * mm, "end": v(139.41, 212.95) * mm});
            skLineSegment(sketch, "E1123", {"start": v(139.41, 212.95) * mm, "end": v(138.95, 213.16) * mm});
            skLineSegment(sketch, "E1124", {"start": v(138.95, 213.16) * mm, "end": v(138.5, 213.38) * mm});
            skLineSegment(sketch, "E1125", {"start": v(138.5, 213.38) * mm, "end": v(138.05, 213.62) * mm});
            skLineSegment(sketch, "E1126", {"start": v(138.05, 213.62) * mm, "end": v(137.6, 213.87) * mm});
            skLineSegment(sketch, "E1127", {"start": v(137.6, 213.87) * mm, "end": v(137.16, 214.12) * mm});
            skLineSegment(sketch, "E1128", {"start": v(137.16, 214.12) * mm, "end": v(136.73, 214.4) * mm});
            skLineSegment(sketch, "E1129", {"start": v(136.73, 214.4) * mm, "end": v(136.3, 214.67) * mm});
            skLineSegment(sketch, "E1130", {"start": v(136.3, 214.67) * mm, "end": v(135.89, 214.96) * mm});
            skLineSegment(sketch, "E1131", {"start": v(135.89, 214.96) * mm, "end": v(135.48, 215.27) * mm});
            skLineSegment(sketch, "E1132", {"start": v(135.48, 215.27) * mm, "end": v(135.07, 215.58) * mm});
            skLineSegment(sketch, "E1133", {"start": v(135.07, 215.58) * mm, "end": v(134.68, 215.9) * mm});
            skLineSegment(sketch, "E1134", {"start": v(134.68, 215.9) * mm, "end": v(134.29, 216.24) * mm});
            skLineSegment(sketch, "E1135", {"start": v(134.29, 216.24) * mm, "end": v(133.9, 216.58) * mm});
            skLineSegment(sketch, "E1136", {"start": v(133.9, 216.58) * mm, "end": v(133.53, 216.93) * mm});
            skLineSegment(sketch, "E1137", {"start": v(133.53, 216.93) * mm, "end": v(133.24, 217.23) * mm});
            skLineSegment(sketch, "E1138", {"start": v(133.24, 217.23) * mm, "end": v(132.96, 217.53) * mm});
            skLineSegment(sketch, "E1139", {"start": v(132.96, 217.53) * mm, "end": v(132.68, 217.84) * mm});
            skLineSegment(sketch, "E1140", {"start": v(132.68, 217.84) * mm, "end": v(132.41, 218.15) * mm});
            skLineSegment(sketch, "E1141", {"start": v(132.41, 218.15) * mm, "end": v(132.16, 218.47) * mm});
            skLineSegment(sketch, "E1142", {"start": v(132.16, 218.47) * mm, "end": v(131.9, 218.8) * mm});
            skLineSegment(sketch, "E1143", {"start": v(131.9, 218.8) * mm, "end": v(131.66, 219.13) * mm});
            skLineSegment(sketch, "E1144", {"start": v(131.66, 219.13) * mm, "end": v(131.43, 219.46) * mm});
            skLineSegment(sketch, "E1145", {"start": v(131.43, 219.46) * mm, "end": v(131.2, 219.8) * mm});
            skLineSegment(sketch, "E1146", {"start": v(131.2, 219.8) * mm, "end": v(131, 220.15) * mm});
            skLineSegment(sketch, "E1147", {"start": v(131, 220.15) * mm, "end": v(130.79, 220.5) * mm});
            skLineSegment(sketch, "E1148", {"start": v(130.79, 220.5) * mm, "end": v(130.59, 220.86) * mm});
            skLineSegment(sketch, "E1149", {"start": v(130.59, 220.86) * mm, "end": v(130.4, 221.22) * mm});
            skLineSegment(sketch, "E1150", {"start": v(130.4, 221.22) * mm, "end": v(130.22, 221.59) * mm});
            skLineSegment(sketch, "E1151", {"start": v(130.22, 221.59) * mm, "end": v(130.05, 221.96) * mm});
            skLineSegment(sketch, "E1152", {"start": v(130.05, 221.96) * mm, "end": v(129.89, 222.33) * mm});
            skLineSegment(sketch, "E1153", {"start": v(129.89, 222.33) * mm, "end": v(129.74, 222.71) * mm});
            skLineSegment(sketch, "E1154", {"start": v(129.74, 222.71) * mm, "end": v(129.6, 223.1) * mm});
            skLineSegment(sketch, "E1155", {"start": v(129.6, 223.1) * mm, "end": v(129.46, 223.48) * mm});
            skLineSegment(sketch, "E1156", {"start": v(129.46, 223.48) * mm, "end": v(129.34, 223.87) * mm});
            skLineSegment(sketch, "E1157", {"start": v(129.34, 223.87) * mm, "end": v(129.23, 224.26) * mm});
            skLineSegment(sketch, "E1158", {"start": v(129.23, 224.26) * mm, "end": v(129.12, 224.66) * mm});
            skLineSegment(sketch, "E1159", {"start": v(129.12, 224.66) * mm, "end": v(129.03, 225.05) * mm});
            skLineSegment(sketch, "E1160", {"start": v(129.03, 225.05) * mm, "end": v(128.94, 225.45) * mm});
            skLineSegment(sketch, "E1161", {"start": v(128.94, 225.45) * mm, "end": v(128.87, 225.86) * mm});
            skLineSegment(sketch, "E1162", {"start": v(128.87, 225.86) * mm, "end": v(128.8, 226.26) * mm});
            skLineSegment(sketch, "E1163", {"start": v(128.8, 226.26) * mm, "end": v(128.75, 226.67) * mm});
            skLineSegment(sketch, "E1164", {"start": v(128.75, 226.67) * mm, "end": v(128.7, 227.08) * mm});
            skLineSegment(sketch, "E1165", {"start": v(128.7, 227.08) * mm, "end": v(128.67, 227.49) * mm});
            skLineSegment(sketch, "E1166", {"start": v(128.67, 227.49) * mm, "end": v(128.65, 227.9) * mm});
            skLineSegment(sketch, "E1167", {"start": v(128.65, 227.9) * mm, "end": v(128.63, 228.3) * mm});
            skLineSegment(sketch, "E1168", {"start": v(128.63, 228.3) * mm, "end": v(128.63, 228.72) * mm});
            skLineSegment(sketch, "E1169", {"start": v(129.2, 202.15) * mm, "end": v(169.15, 202.15) * mm});
            skLineSegment(sketch, "E1170", {"start": v(169.15, 202.15) * mm, "end": v(169.15, 184.59) * mm});
            skLineSegment(sketch, "E1171", {"start": v(169.15, 184.59) * mm, "end": v(169.15, 184.1) * mm});
            skLineSegment(sketch, "E1172", {"start": v(169.15, 184.1) * mm, "end": v(169.12, 183.6) * mm});
            skLineSegment(sketch, "E1173", {"start": v(169.12, 183.6) * mm, "end": v(169.06, 183.12) * mm});
            skLineSegment(sketch, "E1174", {"start": v(169.06, 183.12) * mm, "end": v(168.99, 182.63) * mm});
            skLineSegment(sketch, "E1175", {"start": v(168.99, 182.63) * mm, "end": v(168.88, 182.16) * mm});
            skLineSegment(sketch, "E1176", {"start": v(168.88, 182.16) * mm, "end": v(168.76, 181.69) * mm});
            skLineSegment(sketch, "E1177", {"start": v(168.76, 181.69) * mm, "end": v(168.6, 181.22) * mm});
            skLineSegment(sketch, "E1178", {"start": v(168.6, 181.22) * mm, "end": v(168.43, 180.77) * mm});
            skLineSegment(sketch, "E1179", {"start": v(168.43, 180.77) * mm, "end": v(168.23, 180.32) * mm});
            skLineSegment(sketch, "E1180", {"start": v(168.23, 180.32) * mm, "end": v(168.01, 179.89) * mm});
            skLineSegment(sketch, "E1181", {"start": v(168.01, 179.89) * mm, "end": v(167.77, 179.46) * mm});
            skLineSegment(sketch, "E1182", {"start": v(167.77, 179.46) * mm, "end": v(167.51, 179.05) * mm});
            skLineSegment(sketch, "E1183", {"start": v(167.51, 179.05) * mm, "end": v(167.23, 178.65) * mm});
            skLineSegment(sketch, "E1184", {"start": v(167.23, 178.65) * mm, "end": v(166.92, 178.27) * mm});
            skLineSegment(sketch, "E1185", {"start": v(166.92, 178.27) * mm, "end": v(166.6, 177.9) * mm});
            skLineSegment(sketch, "E1186", {"start": v(166.6, 177.9) * mm, "end": v(166.25, 177.55) * mm});
            skLineSegment(sketch, "E1187", {"start": v(166.25, 177.55) * mm, "end": v(165.9, 177.2) * mm});
            skLineSegment(sketch, "E1188", {"start": v(165.9, 177.2) * mm, "end": v(165.53, 176.89) * mm});
            skLineSegment(sketch, "E1189", {"start": v(165.53, 176.89) * mm, "end": v(165.15, 176.58) * mm});
            skLineSegment(sketch, "E1190", {"start": v(165.15, 176.58) * mm, "end": v(164.76, 176.3) * mm});
            skLineSegment(sketch, "E1191", {"start": v(164.76, 176.3) * mm, "end": v(164.35, 176.04) * mm});
            skLineSegment(sketch, "E1192", {"start": v(164.35, 176.04) * mm, "end": v(163.93, 175.8) * mm});
            skLineSegment(sketch, "E1193", {"start": v(163.93, 175.8) * mm, "end": v(163.5, 175.58) * mm});
            skLineSegment(sketch, "E1194", {"start": v(163.5, 175.58) * mm, "end": v(163.06, 175.39) * mm});
            skLineSegment(sketch, "E1195", {"start": v(163.06, 175.39) * mm, "end": v(162.6, 175.21) * mm});
            skLineSegment(sketch, "E1196", {"start": v(162.6, 175.21) * mm, "end": v(162.15, 175.06) * mm});
            skLineSegment(sketch, "E1197", {"start": v(162.15, 175.06) * mm, "end": v(161.68, 174.93) * mm});
            skLineSegment(sketch, "E1198", {"start": v(161.68, 174.93) * mm, "end": v(161.21, 174.82) * mm});
            skLineSegment(sketch, "E1199", {"start": v(161.21, 174.82) * mm, "end": v(160.73, 174.74) * mm});
            skLineSegment(sketch, "E1200", {"start": v(160.73, 174.74) * mm, "end": v(160.25, 174.68) * mm});
            skLineSegment(sketch, "E1201", {"start": v(160.25, 174.68) * mm, "end": v(159.76, 174.64) * mm});
            skLineSegment(sketch, "E1202", {"start": v(159.76, 174.64) * mm, "end": v(159.27, 174.63) * mm});
            skLineSegment(sketch, "E1203", {"start": v(159.27, 174.63) * mm, "end": v(158.77, 174.63) * mm});
            skLineSegment(sketch, "E1204", {"start": v(158.77, 174.63) * mm, "end": v(158.27, 174.65) * mm});
            skLineSegment(sketch, "E1205", {"start": v(158.27, 174.65) * mm, "end": v(157.78, 174.7) * mm});
            skLineSegment(sketch, "E1206", {"start": v(157.78, 174.7) * mm, "end": v(157.29, 174.77) * mm});
            skLineSegment(sketch, "E1207", {"start": v(157.29, 174.77) * mm, "end": v(156.8, 174.87) * mm});
            skLineSegment(sketch, "E1208", {"start": v(156.8, 174.87) * mm, "end": v(156.32, 175) * mm});
            skLineSegment(sketch, "E1209", {"start": v(156.32, 175) * mm, "end": v(155.85, 175.14) * mm});
            skLineSegment(sketch, "E1210", {"start": v(155.85, 175.14) * mm, "end": v(155.38, 175.3) * mm});
            skLineSegment(sketch, "E1211", {"start": v(155.38, 175.3) * mm, "end": v(154.93, 175.5) * mm});
            skLineSegment(sketch, "E1212", {"start": v(154.93, 175.5) * mm, "end": v(154.48, 175.72) * mm});
            skLineSegment(sketch, "E1213", {"start": v(154.48, 175.72) * mm, "end": v(154.05, 175.95) * mm});
            skLineSegment(sketch, "E1214", {"start": v(154.05, 175.95) * mm, "end": v(153.63, 176.21) * mm});
            skLineSegment(sketch, "E1215", {"start": v(153.63, 176.21) * mm, "end": v(153.22, 176.5) * mm});
            skLineSegment(sketch, "E1216", {"start": v(153.22, 176.5) * mm, "end": v(152.82, 176.8) * mm});
            skLineSegment(sketch, "E1217", {"start": v(152.82, 176.8) * mm, "end": v(152.44, 177.12) * mm});
            skLineSegment(sketch, "E1218", {"start": v(152.44, 177.12) * mm, "end": v(152.08, 177.47) * mm});
            skLineSegment(sketch, "E1219", {"start": v(152.08, 177.47) * mm, "end": v(151.74, 177.83) * mm});
            skLineSegment(sketch, "E1220", {"start": v(151.74, 177.83) * mm, "end": v(151.41, 178.2) * mm});
            skLineSegment(sketch, "E1221", {"start": v(151.41, 178.2) * mm, "end": v(151.1, 178.6) * mm});
            skLineSegment(sketch, "E1222", {"start": v(151.1, 178.6) * mm, "end": v(150.82, 179) * mm});
            skLineSegment(sketch, "E1223", {"start": v(150.82, 179) * mm, "end": v(150.56, 179.42) * mm});
            skLineSegment(sketch, "E1224", {"start": v(150.56, 179.42) * mm, "end": v(150.32, 179.84) * mm});
            skLineSegment(sketch, "E1225", {"start": v(150.32, 179.84) * mm, "end": v(150.1, 180.28) * mm});
            skLineSegment(sketch, "E1226", {"start": v(150.1, 180.28) * mm, "end": v(149.9, 180.73) * mm});
            skLineSegment(sketch, "E1227", {"start": v(149.9, 180.73) * mm, "end": v(149.73, 181.2) * mm});
            skLineSegment(sketch, "E1228", {"start": v(149.73, 181.2) * mm, "end": v(149.58, 181.66) * mm});
            skLineSegment(sketch, "E1229", {"start": v(149.58, 181.66) * mm, "end": v(149.46, 182.14) * mm});
            skLineSegment(sketch, "E1230", {"start": v(149.46, 182.14) * mm, "end": v(149.35, 182.62) * mm});
            skLineSegment(sketch, "E1231", {"start": v(149.35, 182.62) * mm, "end": v(149.27, 183.1) * mm});
            skLineSegment(sketch, "E1232", {"start": v(149.27, 183.1) * mm, "end": v(149.22, 183.6) * mm});
            skLineSegment(sketch, "E1233", {"start": v(149.22, 183.6) * mm, "end": v(149.19, 184.1) * mm});
            skLineSegment(sketch, "E1234", {"start": v(149.19, 184.1) * mm, "end": v(149.18, 184.59) * mm});
            skLineSegment(sketch, "E1235", {"start": v(149.18, 184.59) * mm, "end": v(149.18, 202.15) * mm});
            skLineSegment(sketch, "E1236", {"start": v(149.18, 184.59) * mm, "end": v(149.18, 184.18) * mm});
            skLineSegment(sketch, "E1237", {"start": v(149.18, 184.18) * mm, "end": v(149.16, 183.77) * mm});
            skLineSegment(sketch, "E1238", {"start": v(149.16, 183.77) * mm, "end": v(149.11, 183.37) * mm});
            skLineSegment(sketch, "E1239", {"start": v(149.11, 183.37) * mm, "end": v(149.05, 182.97) * mm});
            skLineSegment(sketch, "E1240", {"start": v(149.05, 182.97) * mm, "end": v(148.96, 182.57) * mm});
            skLineSegment(sketch, "E1241", {"start": v(148.96, 182.57) * mm, "end": v(148.86, 182.18) * mm});
            skLineSegment(sketch, "E1242", {"start": v(148.86, 182.18) * mm, "end": v(148.74, 181.8) * mm});
            skLineSegment(sketch, "E1243", {"start": v(148.74, 181.8) * mm, "end": v(148.6, 181.42) * mm});
            skLineSegment(sketch, "E1244", {"start": v(148.6, 181.42) * mm, "end": v(148.43, 181.05) * mm});
            skLineSegment(sketch, "E1245", {"start": v(148.43, 181.05) * mm, "end": v(148.25, 180.69) * mm});
            skLineSegment(sketch, "E1246", {"start": v(148.25, 180.69) * mm, "end": v(148.05, 180.33) * mm});
            skLineSegment(sketch, "E1247", {"start": v(148.05, 180.33) * mm, "end": v(147.84, 180) * mm});
            skLineSegment(sketch, "E1248", {"start": v(147.84, 180) * mm, "end": v(147.6, 179.66) * mm});
            skLineSegment(sketch, "E1249", {"start": v(147.6, 179.66) * mm, "end": v(147.35, 179.34) * mm});
            skLineSegment(sketch, "E1250", {"start": v(147.35, 179.34) * mm, "end": v(147.08, 179.03) * mm});
            skLineSegment(sketch, "E1251", {"start": v(147.08, 179.03) * mm, "end": v(146.8, 178.74) * mm});
            skLineSegment(sketch, "E1252", {"start": v(146.8, 178.74) * mm, "end": v(146.3, 178.4) * mm});
            skLineSegment(sketch, "E1253", {"start": v(146.3, 178.4) * mm, "end": v(145.78, 178.08) * mm});
            skLineSegment(sketch, "E1254", {"start": v(145.78, 178.08) * mm, "end": v(145.26, 177.79) * mm});
            skLineSegment(sketch, "E1255", {"start": v(145.26, 177.79) * mm, "end": v(144.72, 177.52) * mm});
            skLineSegment(sketch, "E1256", {"start": v(144.72, 177.52) * mm, "end": v(144.17, 177.27) * mm});
            skLineSegment(sketch, "E1257", {"start": v(144.17, 177.27) * mm, "end": v(143.62, 177.05) * mm});
            skLineSegment(sketch, "E1258", {"start": v(143.62, 177.05) * mm, "end": v(143.05, 176.86) * mm});
            skLineSegment(sketch, "E1259", {"start": v(143.05, 176.86) * mm, "end": v(142.48, 176.7) * mm});
            skLineSegment(sketch, "E1260", {"start": v(142.48, 176.7) * mm, "end": v(141.9, 176.55) * mm});
            skLineSegment(sketch, "E1261", {"start": v(141.9, 176.55) * mm, "end": v(141.3, 176.43) * mm});
            skLineSegment(sketch, "E1262", {"start": v(141.3, 176.43) * mm, "end": v(140.72, 176.34) * mm});
            skLineSegment(sketch, "E1263", {"start": v(140.72, 176.34) * mm, "end": v(140.12, 176.27) * mm});
            skLineSegment(sketch, "E1264", {"start": v(140.12, 176.27) * mm, "end": v(139.52, 176.23) * mm});
            skLineSegment(sketch, "E1265", {"start": v(139.52, 176.23) * mm, "end": v(138.92, 176.22) * mm});
            skLineSegment(sketch, "E1266", {"start": v(138.92, 176.22) * mm, "end": v(138.31, 176.24) * mm});
            skLineSegment(sketch, "E1267", {"start": v(138.31, 176.24) * mm, "end": v(137.71, 176.28) * mm});
            skLineSegment(sketch, "E1268", {"start": v(137.71, 176.28) * mm, "end": v(137.17, 176.29) * mm});
            skLineSegment(sketch, "E1269", {"start": v(137.17, 176.29) * mm, "end": v(136.64, 176.28) * mm});
            skLineSegment(sketch, "E1270", {"start": v(136.64, 176.28) * mm, "end": v(136.1, 176.27) * mm});
            skLineSegment(sketch, "E1271", {"start": v(136.1, 176.27) * mm, "end": v(135.56, 176.25) * mm});
            skLineSegment(sketch, "E1272", {"start": v(135.56, 176.25) * mm, "end": v(135.02, 176.22) * mm});
            skLineSegment(sketch, "E1273", {"start": v(135.02, 176.22) * mm, "end": v(134.49, 176.18) * mm});
            skLineSegment(sketch, "E1274", {"start": v(134.49, 176.18) * mm, "end": v(133.95, 176.13) * mm});
            skLineSegment(sketch, "E1275", {"start": v(133.95, 176.13) * mm, "end": v(133.41, 176.07) * mm});
            skLineSegment(sketch, "E1276", {"start": v(133.41, 176.07) * mm, "end": v(132.88, 176) * mm});
            skLineSegment(sketch, "E1277", {"start": v(132.88, 176) * mm, "end": v(132.35, 175.92) * mm});
            skLineSegment(sketch, "E1278", {"start": v(132.35, 175.92) * mm, "end": v(131.82, 175.83) * mm});
            skLineSegment(sketch, "E1279", {"start": v(131.82, 175.83) * mm, "end": v(131.29, 175.73) * mm});
            skLineSegment(sketch, "E1280", {"start": v(131.29, 175.73) * mm, "end": v(130.76, 175.63) * mm});
            skLineSegment(sketch, "E1281", {"start": v(130.76, 175.63) * mm, "end": v(130.23, 175.5) * mm});
            skLineSegment(sketch, "E1282", {"start": v(130.23, 175.5) * mm, "end": v(129.71, 175.38) * mm});
            skLineSegment(sketch, "E1283", {"start": v(129.71, 175.38) * mm, "end": v(129.2, 175.25) * mm});
            skLineSegment(sketch, "E1284", {"start": v(-385.47, 163.58) * mm, "end": v(-425.46, 163.58) * mm});
            skLineSegment(sketch, "E1285", {"start": v(-425.46, 163.58) * mm, "end": v(-425.46, 188.44) * mm});
            skLineSegment(sketch, "E1286", {"start": v(-406.35, 163.58) * mm, "end": v(-406.35, 186.65) * mm});
            skLineSegment(sketch, "E1287", {"start": v(-385.5, 220.74) * mm, "end": v(-385.5, 197.24) * mm});
            skLineSegment(sketch, "E1288", {"start": v(-385.5, 197.24) * mm, "end": v(-425.45, 197.24) * mm});
            skLineSegment(sketch, "E1289", {"start": v(-384.93, 235.9) * mm, "end": v(-384.93, 235.48) * mm});
            skLineSegment(sketch, "E1290", {"start": v(-384.93, 235.48) * mm, "end": v(-384.94, 235.06) * mm});
            skLineSegment(sketch, "E1291", {"start": v(-384.94, 235.06) * mm, "end": v(-384.96, 234.64) * mm});
            skLineSegment(sketch, "E1292", {"start": v(-384.96, 234.64) * mm, "end": v(-384.98, 234.22) * mm});
            skLineSegment(sketch, "E1293", {"start": v(-384.98, 234.22) * mm, "end": v(-385.02, 233.8) * mm});
            skLineSegment(sketch, "E1294", {"start": v(-385.02, 233.8) * mm, "end": v(-385.07, 233.4) * mm});
            skLineSegment(sketch, "E1295", {"start": v(-385.07, 233.4) * mm, "end": v(-385.13, 232.98) * mm});
            skLineSegment(sketch, "E1296", {"start": v(-385.13, 232.98) * mm, "end": v(-385.2, 232.58) * mm});
            skLineSegment(sketch, "E1297", {"start": v(-385.2, 232.58) * mm, "end": v(-385.28, 232.17) * mm});
            skLineSegment(sketch, "E1298", {"start": v(-385.28, 232.17) * mm, "end": v(-385.37, 231.76) * mm});
            skLineSegment(sketch, "E1299", {"start": v(-385.37, 231.76) * mm, "end": v(-385.47, 231.36) * mm});
            skLineSegment(sketch, "E1300", {"start": v(-385.47, 231.36) * mm, "end": v(-385.58, 230.96) * mm});
            skLineSegment(sketch, "E1301", {"start": v(-385.58, 230.96) * mm, "end": v(-385.7, 230.56) * mm});
            skLineSegment(sketch, "E1302", {"start": v(-385.7, 230.56) * mm, "end": v(-385.83, 230.17) * mm});
            skLineSegment(sketch, "E1303", {"start": v(-385.83, 230.17) * mm, "end": v(-385.97, 229.78) * mm});
            skLineSegment(sketch, "E1304", {"start": v(-385.97, 229.78) * mm, "end": v(-386.11, 229.4) * mm});
            skLineSegment(sketch, "E1305", {"start": v(-386.11, 229.4) * mm, "end": v(-386.27, 229.01) * mm});
            skLineSegment(sketch, "E1306", {"start": v(-386.27, 229.01) * mm, "end": v(-386.44, 228.64) * mm});
            skLineSegment(sketch, "E1307", {"start": v(-386.44, 228.64) * mm, "end": v(-386.62, 228.26) * mm});
            skLineSegment(sketch, "E1308", {"start": v(-386.62, 228.26) * mm, "end": v(-386.8, 227.9) * mm});
            skLineSegment(sketch, "E1309", {"start": v(-386.8, 227.9) * mm, "end": v(-387, 227.53) * mm});
            skLineSegment(sketch, "E1310", {"start": v(-387, 227.53) * mm, "end": v(-387.2, 227.17) * mm});
            skLineSegment(sketch, "E1311", {"start": v(-387.2, 227.17) * mm, "end": v(-387.42, 226.8) * mm});
            skLineSegment(sketch, "E1312", {"start": v(-387.42, 226.8) * mm, "end": v(-387.64, 226.46) * mm});
            skLineSegment(sketch, "E1313", {"start": v(-387.64, 226.46) * mm, "end": v(-387.87, 226.11) * mm});
            skLineSegment(sketch, "E1314", {"start": v(-387.87, 226.11) * mm, "end": v(-388.1, 225.77) * mm});
            skLineSegment(sketch, "E1315", {"start": v(-388.1, 225.77) * mm, "end": v(-388.36, 225.44) * mm});
            skLineSegment(sketch, "E1316", {"start": v(-388.36, 225.44) * mm, "end": v(-388.61, 225.11) * mm});
            skLineSegment(sketch, "E1317", {"start": v(-388.61, 225.11) * mm, "end": v(-388.88, 224.8) * mm});
            skLineSegment(sketch, "E1318", {"start": v(-388.88, 224.8) * mm, "end": v(-389.15, 224.47) * mm});
            skLineSegment(sketch, "E1319", {"start": v(-389.15, 224.47) * mm, "end": v(-389.44, 224.17) * mm});
            skLineSegment(sketch, "E1320", {"start": v(-389.44, 224.17) * mm, "end": v(-389.73, 223.86) * mm});
            skLineSegment(sketch, "E1321", {"start": v(-389.73, 223.86) * mm, "end": v(-390.1, 223.51) * mm});
            skLineSegment(sketch, "E1322", {"start": v(-390.1, 223.51) * mm, "end": v(-390.5, 223.17) * mm});
            skLineSegment(sketch, "E1323", {"start": v(-390.5, 223.17) * mm, "end": v(-390.9, 222.85) * mm});
            skLineSegment(sketch, "E1324", {"start": v(-390.9, 222.85) * mm, "end": v(-391.3, 222.53) * mm});
            skLineSegment(sketch, "E1325", {"start": v(-391.3, 222.53) * mm, "end": v(-391.7, 222.22) * mm});
            skLineSegment(sketch, "E1326", {"start": v(-391.7, 222.22) * mm, "end": v(-392.12, 221.92) * mm});
            skLineSegment(sketch, "E1327", {"start": v(-392.12, 221.92) * mm, "end": v(-392.55, 221.63) * mm});
            skLineSegment(sketch, "E1328", {"start": v(-392.55, 221.63) * mm, "end": v(-392.98, 221.36) * mm});
            skLineSegment(sketch, "E1329", {"start": v(-392.98, 221.36) * mm, "end": v(-393.42, 221.1) * mm});
            skLineSegment(sketch, "E1330", {"start": v(-393.42, 221.1) * mm, "end": v(-393.86, 220.84) * mm});
            skLineSegment(sketch, "E1331", {"start": v(-393.86, 220.84) * mm, "end": v(-394.3, 220.6) * mm});
            skLineSegment(sketch, "E1332", {"start": v(-394.3, 220.6) * mm, "end": v(-394.76, 220.37) * mm});
            skLineSegment(sketch, "E1333", {"start": v(-394.76, 220.37) * mm, "end": v(-395.22, 220.15) * mm});
            skLineSegment(sketch, "E1334", {"start": v(-395.22, 220.15) * mm, "end": v(-395.69, 219.94) * mm});
            skLineSegment(sketch, "E1335", {"start": v(-395.69, 219.94) * mm, "end": v(-396.16, 219.74) * mm});
            skLineSegment(sketch, "E1336", {"start": v(-396.16, 219.74) * mm, "end": v(-396.63, 219.56) * mm});
            skLineSegment(sketch, "E1337", {"start": v(-396.63, 219.56) * mm, "end": v(-397.11, 219.38) * mm});
            skLineSegment(sketch, "E1338", {"start": v(-397.11, 219.38) * mm, "end": v(-397.6, 219.22) * mm});
            skLineSegment(sketch, "E1339", {"start": v(-397.6, 219.22) * mm, "end": v(-398.08, 219.07) * mm});
            skLineSegment(sketch, "E1340", {"start": v(-398.08, 219.07) * mm, "end": v(-398.57, 218.93) * mm});
            skLineSegment(sketch, "E1341", {"start": v(-398.57, 218.93) * mm, "end": v(-399.06, 218.8) * mm});
            skLineSegment(sketch, "E1342", {"start": v(-399.06, 218.8) * mm, "end": v(-399.56, 218.7) * mm});
            skLineSegment(sketch, "E1343", {"start": v(-399.56, 218.7) * mm, "end": v(-400.06, 218.59) * mm});
            skLineSegment(sketch, "E1344", {"start": v(-400.06, 218.59) * mm, "end": v(-400.56, 218.5) * mm});
            skLineSegment(sketch, "E1345", {"start": v(-400.56, 218.5) * mm, "end": v(-401.07, 218.42) * mm});
            skLineSegment(sketch, "E1346", {"start": v(-401.07, 218.42) * mm, "end": v(-401.58, 218.36) * mm});
            skLineSegment(sketch, "E1347", {"start": v(-401.58, 218.36) * mm, "end": v(-402.09, 218.3) * mm});
            skLineSegment(sketch, "E1348", {"start": v(-402.09, 218.3) * mm, "end": v(-402.6, 218.27) * mm});
            skLineSegment(sketch, "E1349", {"start": v(-402.6, 218.27) * mm, "end": v(-403.11, 218.24) * mm});
            skLineSegment(sketch, "E1350", {"start": v(-403.11, 218.24) * mm, "end": v(-403.63, 218.23) * mm});
            skLineSegment(sketch, "E1351", {"start": v(-403.63, 218.23) * mm, "end": v(-404.14, 218.22) * mm});
            skLineSegment(sketch, "E1352", {"start": v(-404.14, 218.22) * mm, "end": v(-404.66, 218.24) * mm});
            skLineSegment(sketch, "E1353", {"start": v(-404.66, 218.24) * mm, "end": v(-405.22, 218.22) * mm});
            skLineSegment(sketch, "E1354", {"start": v(-405.22, 218.22) * mm, "end": v(-405.78, 218.22) * mm});
            skLineSegment(sketch, "E1355", {"start": v(-405.78, 218.22) * mm, "end": v(-406.34, 218.23) * mm});
            skLineSegment(sketch, "E1356", {"start": v(-406.34, 218.23) * mm, "end": v(-406.9, 218.26) * mm});
            skLineSegment(sketch, "E1357", {"start": v(-406.9, 218.26) * mm, "end": v(-407.45, 218.3) * mm});
            skLineSegment(sketch, "E1358", {"start": v(-407.45, 218.3) * mm, "end": v(-408, 218.35) * mm});
            skLineSegment(sketch, "E1359", {"start": v(-408, 218.35) * mm, "end": v(-408.56, 218.42) * mm});
            skLineSegment(sketch, "E1360", {"start": v(-408.56, 218.42) * mm, "end": v(-409.1, 218.5) * mm});
            skLineSegment(sketch, "E1361", {"start": v(-409.1, 218.5) * mm, "end": v(-409.65, 218.6) * mm});
            skLineSegment(sketch, "E1362", {"start": v(-409.65, 218.6) * mm, "end": v(-410.2, 218.7) * mm});
            skLineSegment(sketch, "E1363", {"start": v(-410.2, 218.7) * mm, "end": v(-410.74, 218.83) * mm});
            skLineSegment(sketch, "E1364", {"start": v(-410.74, 218.83) * mm, "end": v(-411.27, 218.97) * mm});
            skLineSegment(sketch, "E1365", {"start": v(-411.27, 218.97) * mm, "end": v(-411.8, 219.11) * mm});
            skLineSegment(sketch, "E1366", {"start": v(-411.8, 219.11) * mm, "end": v(-412.34, 219.28) * mm});
            skLineSegment(sketch, "E1367", {"start": v(-412.34, 219.28) * mm, "end": v(-412.86, 219.45) * mm});
            skLineSegment(sketch, "E1368", {"start": v(-412.86, 219.45) * mm, "end": v(-413.38, 219.64) * mm});
            skLineSegment(sketch, "E1369", {"start": v(-413.38, 219.64) * mm, "end": v(-413.9, 219.84) * mm});
            skLineSegment(sketch, "E1370", {"start": v(-413.9, 219.84) * mm, "end": v(-414.4, 220.05) * mm});
            skLineSegment(sketch, "E1371", {"start": v(-414.4, 220.05) * mm, "end": v(-414.91, 220.28) * mm});
            skLineSegment(sketch, "E1372", {"start": v(-414.91, 220.28) * mm, "end": v(-415.4, 220.52) * mm});
            skLineSegment(sketch, "E1373", {"start": v(-415.4, 220.52) * mm, "end": v(-415.9, 220.77) * mm});
            skLineSegment(sketch, "E1374", {"start": v(-415.9, 220.77) * mm, "end": v(-416.4, 221.03) * mm});
            skLineSegment(sketch, "E1375", {"start": v(-416.4, 221.03) * mm, "end": v(-416.87, 221.31) * mm});
            skLineSegment(sketch, "E1376", {"start": v(-416.87, 221.31) * mm, "end": v(-417.35, 221.6) * mm});
            skLineSegment(sketch, "E1377", {"start": v(-417.35, 221.6) * mm, "end": v(-417.81, 221.9) * mm});
            skLineSegment(sketch, "E1378", {"start": v(-417.81, 221.9) * mm, "end": v(-418.27, 222.21) * mm});
            skLineSegment(sketch, "E1379", {"start": v(-418.27, 222.21) * mm, "end": v(-418.73, 222.53) * mm});
            skLineSegment(sketch, "E1380", {"start": v(-418.73, 222.53) * mm, "end": v(-419.17, 222.87) * mm});
            skLineSegment(sketch, "E1381", {"start": v(-419.17, 222.87) * mm, "end": v(-419.6, 223.22) * mm});
            skLineSegment(sketch, "E1382", {"start": v(-419.6, 223.22) * mm, "end": v(-420.04, 223.58) * mm});
            skLineSegment(sketch, "E1383", {"start": v(-420.04, 223.58) * mm, "end": v(-420.46, 223.95) * mm});
            skLineSegment(sketch, "E1384", {"start": v(-420.46, 223.95) * mm, "end": v(-420.87, 224.33) * mm});
            skLineSegment(sketch, "E1385", {"start": v(-420.87, 224.33) * mm, "end": v(-421.16, 224.61) * mm});
            skLineSegment(sketch, "E1386", {"start": v(-421.16, 224.61) * mm, "end": v(-421.44, 224.9) * mm});
            skLineSegment(sketch, "E1387", {"start": v(-421.44, 224.9) * mm, "end": v(-421.72, 225.2) * mm});
            skLineSegment(sketch, "E1388", {"start": v(-421.72, 225.2) * mm, "end": v(-421.98, 225.51) * mm});
            skLineSegment(sketch, "E1389", {"start": v(-421.98, 225.51) * mm, "end": v(-422.24, 225.82) * mm});
            skLineSegment(sketch, "E1390", {"start": v(-422.24, 225.82) * mm, "end": v(-422.49, 226.14) * mm});
            skLineSegment(sketch, "E1391", {"start": v(-422.49, 226.14) * mm, "end": v(-422.73, 226.47) * mm});
            skLineSegment(sketch, "E1392", {"start": v(-422.73, 226.47) * mm, "end": v(-422.96, 226.8) * mm});
            skLineSegment(sketch, "E1393", {"start": v(-422.96, 226.8) * mm, "end": v(-423.18, 227.13) * mm});
            skLineSegment(sketch, "E1394", {"start": v(-423.18, 227.13) * mm, "end": v(-423.4, 227.47) * mm});
            skLineSegment(sketch, "E1395", {"start": v(-423.4, 227.47) * mm, "end": v(-423.6, 227.82) * mm});
            skLineSegment(sketch, "E1396", {"start": v(-423.6, 227.82) * mm, "end": v(-423.8, 228.17) * mm});
            skLineSegment(sketch, "E1397", {"start": v(-423.8, 228.17) * mm, "end": v(-423.98, 228.52) * mm});
            skLineSegment(sketch, "E1398", {"start": v(-423.98, 228.52) * mm, "end": v(-424.16, 228.88) * mm});
            skLineSegment(sketch, "E1399", {"start": v(-424.16, 228.88) * mm, "end": v(-424.33, 229.25) * mm});
            skLineSegment(sketch, "E1400", {"start": v(-424.33, 229.25) * mm, "end": v(-424.49, 229.61) * mm});
            skLineSegment(sketch, "E1401", {"start": v(-424.49, 229.61) * mm, "end": v(-424.64, 229.99) * mm});
            skLineSegment(sketch, "E1402", {"start": v(-424.64, 229.99) * mm, "end": v(-424.78, 230.36) * mm});
            skLineSegment(sketch, "E1403", {"start": v(-424.78, 230.36) * mm, "end": v(-424.9, 230.74) * mm});
            skLineSegment(sketch, "E1404", {"start": v(-424.9, 230.74) * mm, "end": v(-425.03, 231.12) * mm});
            skLineSegment(sketch, "E1405", {"start": v(-425.03, 231.12) * mm, "end": v(-425.14, 231.5) * mm});
            skLineSegment(sketch, "E1406", {"start": v(-425.14, 231.5) * mm, "end": v(-425.24, 231.9) * mm});
            skLineSegment(sketch, "E1407", {"start": v(-425.24, 231.9) * mm, "end": v(-425.33, 232.3) * mm});
            skLineSegment(sketch, "E1408", {"start": v(-425.33, 232.3) * mm, "end": v(-425.41, 232.68) * mm});
            skLineSegment(sketch, "E1409", {"start": v(-425.41, 232.68) * mm, "end": v(-425.49, 233.08) * mm});
            skLineSegment(sketch, "E1410", {"start": v(-425.49, 233.08) * mm, "end": v(-425.55, 233.48) * mm});
            skLineSegment(sketch, "E1411", {"start": v(-425.55, 233.48) * mm, "end": v(-425.6, 233.88) * mm});
            skLineSegment(sketch, "E1412", {"start": v(-425.6, 233.88) * mm, "end": v(-425.64, 234.28) * mm});
            skLineSegment(sketch, "E1413", {"start": v(-425.64, 234.28) * mm, "end": v(-425.67, 234.69) * mm});
            skLineSegment(sketch, "E1414", {"start": v(-425.67, 234.69) * mm, "end": v(-425.69, 235.1) * mm});
            skLineSegment(sketch, "E1415", {"start": v(-425.69, 235.1) * mm, "end": v(-425.7, 235.5) * mm});
            skLineSegment(sketch, "E1416", {"start": v(-425.7, 235.5) * mm, "end": v(-425.7, 235.9) * mm});
            skLineSegment(sketch, "E1417", {"start": v(-425.7, 235.9) * mm, "end": v(-425.7, 236.32) * mm});
            skLineSegment(sketch, "E1418", {"start": v(-425.7, 236.32) * mm, "end": v(-425.68, 236.73) * mm});
            skLineSegment(sketch, "E1419", {"start": v(-425.68, 236.73) * mm, "end": v(-425.65, 237.15) * mm});
            skLineSegment(sketch, "E1420", {"start": v(-425.65, 237.15) * mm, "end": v(-425.62, 237.56) * mm});
            skLineSegment(sketch, "E1421", {"start": v(-425.62, 237.56) * mm, "end": v(-425.57, 237.96) * mm});
            skLineSegment(sketch, "E1422", {"start": v(-425.57, 237.96) * mm, "end": v(-425.51, 238.37) * mm});
            skLineSegment(sketch, "E1423", {"start": v(-425.51, 238.37) * mm, "end": v(-425.45, 238.78) * mm});
            skLineSegment(sketch, "E1424", {"start": v(-425.45, 238.78) * mm, "end": v(-425.37, 239.18) * mm});
            skLineSegment(sketch, "E1425", {"start": v(-425.37, 239.18) * mm, "end": v(-425.28, 239.58) * mm});
            skLineSegment(sketch, "E1426", {"start": v(-425.28, 239.58) * mm, "end": v(-425.18, 239.97) * mm});
            skLineSegment(sketch, "E1427", {"start": v(-425.18, 239.97) * mm, "end": v(-425.07, 240.37) * mm});
            skLineSegment(sketch, "E1428", {"start": v(-425.07, 240.37) * mm, "end": v(-424.96, 240.76) * mm});
            skLineSegment(sketch, "E1429", {"start": v(-424.96, 240.76) * mm, "end": v(-424.83, 241.15) * mm});
            skLineSegment(sketch, "E1430", {"start": v(-424.83, 241.15) * mm, "end": v(-424.7, 241.53) * mm});
            skLineSegment(sketch, "E1431", {"start": v(-424.7, 241.53) * mm, "end": v(-424.54, 241.91) * mm});
            skLineSegment(sketch, "E1432", {"start": v(-424.54, 241.91) * mm, "end": v(-424.39, 242.29) * mm});
            skLineSegment(sketch, "E1433", {"start": v(-424.39, 242.29) * mm, "end": v(-424.22, 242.66) * mm});
            skLineSegment(sketch, "E1434", {"start": v(-424.22, 242.66) * mm, "end": v(-424.05, 243.03) * mm});
            skLineSegment(sketch, "E1435", {"start": v(-424.05, 243.03) * mm, "end": v(-423.86, 243.4) * mm});
            skLineSegment(sketch, "E1436", {"start": v(-423.86, 243.4) * mm, "end": v(-423.67, 243.75) * mm});
            skLineSegment(sketch, "E1437", {"start": v(-423.67, 243.75) * mm, "end": v(-423.46, 244.1) * mm});
            skLineSegment(sketch, "E1438", {"start": v(-423.46, 244.1) * mm, "end": v(-423.25, 244.45) * mm});
            skLineSegment(sketch, "E1439", {"start": v(-423.25, 244.45) * mm, "end": v(-423.03, 244.8) * mm});
            skLineSegment(sketch, "E1440", {"start": v(-423.03, 244.8) * mm, "end": v(-422.8, 245.13) * mm});
            skLineSegment(sketch, "E1441", {"start": v(-422.8, 245.13) * mm, "end": v(-422.56, 245.47) * mm});
            skLineSegment(sketch, "E1442", {"start": v(-422.56, 245.47) * mm, "end": v(-422.31, 245.8) * mm});
            skLineSegment(sketch, "E1443", {"start": v(-422.31, 245.8) * mm, "end": v(-422.06, 246.11) * mm});
            skLineSegment(sketch, "E1444", {"start": v(-422.06, 246.11) * mm, "end": v(-421.79, 246.43) * mm});
            skLineSegment(sketch, "E1445", {"start": v(-421.79, 246.43) * mm, "end": v(-421.52, 246.73) * mm});
            skLineSegment(sketch, "E1446", {"start": v(-421.52, 246.73) * mm, "end": v(-421.23, 247.03) * mm});
            skLineSegment(sketch, "E1447", {"start": v(-421.23, 247.03) * mm, "end": v(-420.94, 247.33) * mm});
            skLineSegment(sketch, "E1448", {"start": v(-420.94, 247.33) * mm, "end": v(-420.64, 247.62) * mm});
            skLineSegment(sketch, "E1449", {"start": v(-420.64, 247.62) * mm, "end": v(-420.23, 247.99) * mm});
            skLineSegment(sketch, "E1450", {"start": v(-420.23, 247.99) * mm, "end": v(-419.82, 248.34) * mm});
            skLineSegment(sketch, "E1451", {"start": v(-419.82, 248.34) * mm, "end": v(-419.4, 248.7) * mm});
            skLineSegment(sketch, "E1452", {"start": v(-419.4, 248.7) * mm, "end": v(-418.96, 249.03) * mm});
            skLineSegment(sketch, "E1453", {"start": v(-418.96, 249.03) * mm, "end": v(-418.51, 249.35) * mm});
            skLineSegment(sketch, "E1454", {"start": v(-418.51, 249.35) * mm, "end": v(-418.07, 249.67) * mm});
            skLineSegment(sketch, "E1455", {"start": v(-418.07, 249.67) * mm, "end": v(-417.61, 249.97) * mm});
            skLineSegment(sketch, "E1456", {"start": v(-417.61, 249.97) * mm, "end": v(-417.15, 250.26) * mm});
            skLineSegment(sketch, "E1457", {"start": v(-417.15, 250.26) * mm, "end": v(-416.68, 250.54) * mm});
            skLineSegment(sketch, "E1458", {"start": v(-416.68, 250.54) * mm, "end": v(-416.2, 250.8) * mm});
            skLineSegment(sketch, "E1459", {"start": v(-416.2, 250.8) * mm, "end": v(-415.72, 251.06) * mm});
            skLineSegment(sketch, "E1460", {"start": v(-415.72, 251.06) * mm, "end": v(-415.23, 251.3) * mm});
            skLineSegment(sketch, "E1461", {"start": v(-415.23, 251.3) * mm, "end": v(-414.74, 251.53) * mm});
            skLineSegment(sketch, "E1462", {"start": v(-414.74, 251.53) * mm, "end": v(-414.24, 251.75) * mm});
            skLineSegment(sketch, "E1463", {"start": v(-414.24, 251.75) * mm, "end": v(-413.74, 251.95) * mm});
            skLineSegment(sketch, "E1464", {"start": v(-413.74, 251.95) * mm, "end": v(-413.23, 252.14) * mm});
            skLineSegment(sketch, "E1465", {"start": v(-413.23, 252.14) * mm, "end": v(-412.71, 252.32) * mm});
            skLineSegment(sketch, "E1466", {"start": v(-412.71, 252.32) * mm, "end": v(-412.2, 252.5) * mm});
            skLineSegment(sketch, "E1467", {"start": v(-412.2, 252.5) * mm, "end": v(-411.67, 252.64) * mm});
            skLineSegment(sketch, "E1468", {"start": v(-411.67, 252.64) * mm, "end": v(-411.15, 252.79) * mm});
            skLineSegment(sketch, "E1469", {"start": v(-411.15, 252.79) * mm, "end": v(-410.62, 252.91) * mm});
            skLineSegment(sketch, "E1470", {"start": v(-410.62, 252.91) * mm, "end": v(-410.09, 253.03) * mm});
            skLineSegment(sketch, "E1471", {"start": v(-410.09, 253.03) * mm, "end": v(-409.55, 253.13) * mm});
            skLineSegment(sketch, "E1472", {"start": v(-409.55, 253.13) * mm, "end": v(-409.01, 253.22) * mm});
            skLineSegment(sketch, "E1473", {"start": v(-409.01, 253.22) * mm, "end": v(-408.47, 253.3) * mm});
            skLineSegment(sketch, "E1474", {"start": v(-408.47, 253.3) * mm, "end": v(-407.93, 253.36) * mm});
            skLineSegment(sketch, "E1475", {"start": v(-407.93, 253.36) * mm, "end": v(-407.38, 253.41) * mm});
            skLineSegment(sketch, "E1476", {"start": v(-407.38, 253.41) * mm, "end": v(-406.84, 253.45) * mm});
            skLineSegment(sketch, "E1477", {"start": v(-406.84, 253.45) * mm, "end": v(-406.29, 253.47) * mm});
            skLineSegment(sketch, "E1478", {"start": v(-406.29, 253.47) * mm, "end": v(-405.74, 253.48) * mm});
            skLineSegment(sketch, "E1479", {"start": v(-405.74, 253.48) * mm, "end": v(-405.19, 253.47) * mm});
            skLineSegment(sketch, "E1480", {"start": v(-405.19, 253.47) * mm, "end": v(-404.64, 253.45) * mm});
            skLineSegment(sketch, "E1481", {"start": v(-404.64, 253.45) * mm, "end": v(-404.12, 253.46) * mm});
            skLineSegment(sketch, "E1482", {"start": v(-404.12, 253.46) * mm, "end": v(-403.6, 253.45) * mm});
            skLineSegment(sketch, "E1483", {"start": v(-403.6, 253.45) * mm, "end": v(-403.1, 253.44) * mm});
            skLineSegment(sketch, "E1484", {"start": v(-403.1, 253.44) * mm, "end": v(-402.58, 253.4) * mm});
            skLineSegment(sketch, "E1485", {"start": v(-402.58, 253.4) * mm, "end": v(-402.07, 253.36) * mm});
            skLineSegment(sketch, "E1486", {"start": v(-402.07, 253.36) * mm, "end": v(-401.57, 253.3) * mm});
            skLineSegment(sketch, "E1487", {"start": v(-401.57, 253.3) * mm, "end": v(-401.06, 253.24) * mm});
            skLineSegment(sketch, "E1488", {"start": v(-401.06, 253.24) * mm, "end": v(-400.56, 253.16) * mm});
            skLineSegment(sketch, "E1489", {"start": v(-400.56, 253.16) * mm, "end": v(-400.06, 253.06) * mm});
            skLineSegment(sketch, "E1490", {"start": v(-400.06, 253.06) * mm, "end": v(-399.56, 252.96) * mm});
            skLineSegment(sketch, "E1491", {"start": v(-399.56, 252.96) * mm, "end": v(-399.07, 252.84) * mm});
            skLineSegment(sketch, "E1492", {"start": v(-399.07, 252.84) * mm, "end": v(-398.58, 252.7) * mm});
            skLineSegment(sketch, "E1493", {"start": v(-398.58, 252.7) * mm, "end": v(-398.09, 252.57) * mm});
            skLineSegment(sketch, "E1494", {"start": v(-398.09, 252.57) * mm, "end": v(-397.6, 252.41) * mm});
            skLineSegment(sketch, "E1495", {"start": v(-397.6, 252.41) * mm, "end": v(-397.13, 252.24) * mm});
            skLineSegment(sketch, "E1496", {"start": v(-397.13, 252.24) * mm, "end": v(-396.65, 252.07) * mm});
            skLineSegment(sketch, "E1497", {"start": v(-396.65, 252.07) * mm, "end": v(-396.18, 251.88) * mm});
            skLineSegment(sketch, "E1498", {"start": v(-396.18, 251.88) * mm, "end": v(-395.72, 251.68) * mm});
            skLineSegment(sketch, "E1499", {"start": v(-395.72, 251.68) * mm, "end": v(-395.26, 251.46) * mm});
            skLineSegment(sketch, "E1500", {"start": v(-395.26, 251.46) * mm, "end": v(-394.8, 251.24) * mm});
            skLineSegment(sketch, "E1501", {"start": v(-394.8, 251.24) * mm, "end": v(-394.35, 251) * mm});
            skLineSegment(sketch, "E1502", {"start": v(-394.35, 251) * mm, "end": v(-393.9, 250.76) * mm});
            skLineSegment(sketch, "E1503", {"start": v(-393.9, 250.76) * mm, "end": v(-393.47, 250.5) * mm});
            skLineSegment(sketch, "E1504", {"start": v(-393.47, 250.5) * mm, "end": v(-393.04, 250.23) * mm});
            skLineSegment(sketch, "E1505", {"start": v(-393.04, 250.23) * mm, "end": v(-392.61, 249.95) * mm});
            skLineSegment(sketch, "E1506", {"start": v(-392.61, 249.95) * mm, "end": v(-392.2, 249.66) * mm});
            skLineSegment(sketch, "E1507", {"start": v(-392.2, 249.66) * mm, "end": v(-391.78, 249.36) * mm});
            skLineSegment(sketch, "E1508", {"start": v(-391.78, 249.36) * mm, "end": v(-391.38, 249.04) * mm});
            skLineSegment(sketch, "E1509", {"start": v(-391.38, 249.04) * mm, "end": v(-390.98, 248.72) * mm});
            skLineSegment(sketch, "E1510", {"start": v(-390.98, 248.72) * mm, "end": v(-390.59, 248.39) * mm});
            skLineSegment(sketch, "E1511", {"start": v(-390.59, 248.39) * mm, "end": v(-390.2, 248.04) * mm});
            skLineSegment(sketch, "E1512", {"start": v(-390.2, 248.04) * mm, "end": v(-389.83, 247.69) * mm});
            skLineSegment(sketch, "E1513", {"start": v(-389.83, 247.69) * mm, "end": v(-389.54, 247.4) * mm});
            skLineSegment(sketch, "E1514", {"start": v(-389.54, 247.4) * mm, "end": v(-389.26, 247.1) * mm});
            skLineSegment(sketch, "E1515", {"start": v(-389.26, 247.1) * mm, "end": v(-388.98, 246.79) * mm});
            skLineSegment(sketch, "E1516", {"start": v(-388.98, 246.79) * mm, "end": v(-388.72, 246.47) * mm});
            skLineSegment(sketch, "E1517", {"start": v(-388.72, 246.47) * mm, "end": v(-388.46, 246.15) * mm});
            skLineSegment(sketch, "E1518", {"start": v(-388.46, 246.15) * mm, "end": v(-388.2, 245.83) * mm});
            skLineSegment(sketch, "E1519", {"start": v(-388.2, 245.83) * mm, "end": v(-387.97, 245.5) * mm});
            skLineSegment(sketch, "E1520", {"start": v(-387.97, 245.5) * mm, "end": v(-387.74, 245.16) * mm});
            skLineSegment(sketch, "E1521", {"start": v(-387.74, 245.16) * mm, "end": v(-387.51, 244.82) * mm});
            skLineSegment(sketch, "E1522", {"start": v(-387.51, 244.82) * mm, "end": v(-387.3, 244.47) * mm});
            skLineSegment(sketch, "E1523", {"start": v(-387.3, 244.47) * mm, "end": v(-387.09, 244.12) * mm});
            skLineSegment(sketch, "E1524", {"start": v(-387.09, 244.12) * mm, "end": v(-386.9, 243.76) * mm});
            skLineSegment(sketch, "E1525", {"start": v(-386.9, 243.76) * mm, "end": v(-386.7, 243.4) * mm});
            skLineSegment(sketch, "E1526", {"start": v(-386.7, 243.4) * mm, "end": v(-386.52, 243.03) * mm});
            skLineSegment(sketch, "E1527", {"start": v(-386.52, 243.03) * mm, "end": v(-386.35, 242.66) * mm});
            skLineSegment(sketch, "E1528", {"start": v(-386.35, 242.66) * mm, "end": v(-386.2, 242.29) * mm});
            skLineSegment(sketch, "E1529", {"start": v(-386.2, 242.29) * mm, "end": v(-386.04, 241.9) * mm});
            skLineSegment(sketch, "E1530", {"start": v(-386.04, 241.9) * mm, "end": v(-385.9, 241.53) * mm});
            skLineSegment(sketch, "E1531", {"start": v(-385.9, 241.53) * mm, "end": v(-385.77, 241.14) * mm});
            skLineSegment(sketch, "E1532", {"start": v(-385.77, 241.14) * mm, "end": v(-385.64, 240.75) * mm});
            skLineSegment(sketch, "E1533", {"start": v(-385.64, 240.75) * mm, "end": v(-385.53, 240.36) * mm});
            skLineSegment(sketch, "E1534", {"start": v(-385.53, 240.36) * mm, "end": v(-385.42, 239.97) * mm});
            skLineSegment(sketch, "E1535", {"start": v(-385.42, 239.97) * mm, "end": v(-385.33, 239.57) * mm});
            skLineSegment(sketch, "E1536", {"start": v(-385.33, 239.57) * mm, "end": v(-385.25, 239.17) * mm});
            skLineSegment(sketch, "E1537", {"start": v(-385.25, 239.17) * mm, "end": v(-385.17, 238.77) * mm});
            skLineSegment(sketch, "E1538", {"start": v(-385.17, 238.77) * mm, "end": v(-385.1, 238.36) * mm});
            skLineSegment(sketch, "E1539", {"start": v(-385.1, 238.36) * mm, "end": v(-385.05, 237.95) * mm});
            skLineSegment(sketch, "E1540", {"start": v(-385.05, 237.95) * mm, "end": v(-385, 237.55) * mm});
            skLineSegment(sketch, "E1541", {"start": v(-385, 237.55) * mm, "end": v(-384.97, 237.14) * mm});
            skLineSegment(sketch, "E1542", {"start": v(-384.97, 237.14) * mm, "end": v(-384.95, 236.72) * mm});
            skLineSegment(sketch, "E1543", {"start": v(-384.95, 236.72) * mm, "end": v(-384.94, 236.31) * mm});
            skLineSegment(sketch, "E1544", {"start": v(-384.94, 236.31) * mm, "end": v(-384.93, 235.9) * mm});
            skLineSegment(sketch, "E1545", {"start": v(-384.93, 280.14) * mm, "end": v(-384.93, 279.72) * mm});
            skLineSegment(sketch, "E1546", {"start": v(-384.93, 279.72) * mm, "end": v(-384.94, 279.3) * mm});
            skLineSegment(sketch, "E1547", {"start": v(-384.94, 279.3) * mm, "end": v(-384.96, 278.89) * mm});
            skLineSegment(sketch, "E1548", {"start": v(-384.96, 278.89) * mm, "end": v(-384.98, 278.47) * mm});
            skLineSegment(sketch, "E1549", {"start": v(-384.98, 278.47) * mm, "end": v(-385.02, 278.06) * mm});
            skLineSegment(sketch, "E1550", {"start": v(-385.02, 278.06) * mm, "end": v(-385.07, 277.64) * mm});
            skLineSegment(sketch, "E1551", {"start": v(-385.07, 277.64) * mm, "end": v(-385.13, 277.23) * mm});
            skLineSegment(sketch, "E1552", {"start": v(-385.13, 277.23) * mm, "end": v(-385.2, 276.82) * mm});
            skLineSegment(sketch, "E1553", {"start": v(-385.2, 276.82) * mm, "end": v(-385.28, 276.41) * mm});
            skLineSegment(sketch, "E1554", {"start": v(-385.28, 276.41) * mm, "end": v(-385.37, 276) * mm});
            skLineSegment(sketch, "E1555", {"start": v(-385.37, 276) * mm, "end": v(-385.47, 275.6) * mm});
            skLineSegment(sketch, "E1556", {"start": v(-385.47, 275.6) * mm, "end": v(-385.58, 275.2) * mm});
            skLineSegment(sketch, "E1557", {"start": v(-385.58, 275.2) * mm, "end": v(-385.7, 274.81) * mm});
            skLineSegment(sketch, "E1558", {"start": v(-385.7, 274.81) * mm, "end": v(-385.83, 274.42) * mm});
            skLineSegment(sketch, "E1559", {"start": v(-385.83, 274.42) * mm, "end": v(-385.97, 274.03) * mm});
            skLineSegment(sketch, "E1560", {"start": v(-385.97, 274.03) * mm, "end": v(-386.11, 273.64) * mm});
            skLineSegment(sketch, "E1561", {"start": v(-386.11, 273.64) * mm, "end": v(-386.27, 273.26) * mm});
            skLineSegment(sketch, "E1562", {"start": v(-386.27, 273.26) * mm, "end": v(-386.44, 272.88) * mm});
            skLineSegment(sketch, "E1563", {"start": v(-386.44, 272.88) * mm, "end": v(-386.62, 272.5) * mm});
            skLineSegment(sketch, "E1564", {"start": v(-386.62, 272.5) * mm, "end": v(-386.8, 272.14) * mm});
            skLineSegment(sketch, "E1565", {"start": v(-386.8, 272.14) * mm, "end": v(-387, 271.77) * mm});
            skLineSegment(sketch, "E1566", {"start": v(-387, 271.77) * mm, "end": v(-387.2, 271.41) * mm});
            skLineSegment(sketch, "E1567", {"start": v(-387.2, 271.41) * mm, "end": v(-387.42, 271.05) * mm});
            skLineSegment(sketch, "E1568", {"start": v(-387.42, 271.05) * mm, "end": v(-387.64, 270.7) * mm});
            skLineSegment(sketch, "E1569", {"start": v(-387.64, 270.7) * mm, "end": v(-387.87, 270.36) * mm});
            skLineSegment(sketch, "E1570", {"start": v(-387.87, 270.36) * mm, "end": v(-388.1, 270.02) * mm});
            skLineSegment(sketch, "E1571", {"start": v(-388.1, 270.02) * mm, "end": v(-388.36, 269.69) * mm});
            skLineSegment(sketch, "E1572", {"start": v(-388.36, 269.69) * mm, "end": v(-388.61, 269.36) * mm});
            skLineSegment(sketch, "E1573", {"start": v(-388.61, 269.36) * mm, "end": v(-388.88, 269.04) * mm});
            skLineSegment(sketch, "E1574", {"start": v(-388.88, 269.04) * mm, "end": v(-389.15, 268.72) * mm});
            skLineSegment(sketch, "E1575", {"start": v(-389.15, 268.72) * mm, "end": v(-389.44, 268.41) * mm});
            skLineSegment(sketch, "E1576", {"start": v(-389.44, 268.41) * mm, "end": v(-389.73, 268.1) * mm});
            skLineSegment(sketch, "E1577", {"start": v(-389.73, 268.1) * mm, "end": v(-390.1, 267.76) * mm});
            skLineSegment(sketch, "E1578", {"start": v(-390.1, 267.76) * mm, "end": v(-390.5, 267.42) * mm});
            skLineSegment(sketch, "E1579", {"start": v(-390.5, 267.42) * mm, "end": v(-390.9, 267.1) * mm});
            skLineSegment(sketch, "E1580", {"start": v(-390.9, 267.1) * mm, "end": v(-391.3, 266.77) * mm});
            skLineSegment(sketch, "E1581", {"start": v(-391.3, 266.77) * mm, "end": v(-391.7, 266.46) * mm});
            skLineSegment(sketch, "E1582", {"start": v(-391.7, 266.46) * mm, "end": v(-392.12, 266.17) * mm});
            skLineSegment(sketch, "E1583", {"start": v(-392.12, 266.17) * mm, "end": v(-392.55, 265.88) * mm});
            skLineSegment(sketch, "E1584", {"start": v(-392.55, 265.88) * mm, "end": v(-392.98, 265.6) * mm});
            skLineSegment(sketch, "E1585", {"start": v(-392.98, 265.6) * mm, "end": v(-393.42, 265.34) * mm});
            skLineSegment(sketch, "E1586", {"start": v(-393.42, 265.34) * mm, "end": v(-393.86, 265.09) * mm});
            skLineSegment(sketch, "E1587", {"start": v(-393.86, 265.09) * mm, "end": v(-394.3, 264.84) * mm});
            skLineSegment(sketch, "E1588", {"start": v(-394.3, 264.84) * mm, "end": v(-394.76, 264.61) * mm});
            skLineSegment(sketch, "E1589", {"start": v(-394.76, 264.61) * mm, "end": v(-395.22, 264.4) * mm});
            skLineSegment(sketch, "E1590", {"start": v(-395.22, 264.4) * mm, "end": v(-395.69, 264.18) * mm});
            skLineSegment(sketch, "E1591", {"start": v(-395.69, 264.18) * mm, "end": v(-396.16, 263.99) * mm});
            skLineSegment(sketch, "E1592", {"start": v(-396.16, 263.99) * mm, "end": v(-396.63, 263.8) * mm});
            skLineSegment(sketch, "E1593", {"start": v(-396.63, 263.8) * mm, "end": v(-397.11, 263.63) * mm});
            skLineSegment(sketch, "E1594", {"start": v(-397.11, 263.63) * mm, "end": v(-397.6, 263.47) * mm});
            skLineSegment(sketch, "E1595", {"start": v(-397.6, 263.47) * mm, "end": v(-398.08, 263.32) * mm});
            skLineSegment(sketch, "E1596", {"start": v(-398.08, 263.32) * mm, "end": v(-398.57, 263.18) * mm});
            skLineSegment(sketch, "E1597", {"start": v(-398.57, 263.18) * mm, "end": v(-399.06, 263.05) * mm});
            skLineSegment(sketch, "E1598", {"start": v(-399.06, 263.05) * mm, "end": v(-399.56, 262.94) * mm});
            skLineSegment(sketch, "E1599", {"start": v(-399.56, 262.94) * mm, "end": v(-400.06, 262.84) * mm});
            skLineSegment(sketch, "E1600", {"start": v(-400.06, 262.84) * mm, "end": v(-400.56, 262.75) * mm});
            skLineSegment(sketch, "E1601", {"start": v(-400.56, 262.75) * mm, "end": v(-401.07, 262.67) * mm});
            skLineSegment(sketch, "E1602", {"start": v(-401.07, 262.67) * mm, "end": v(-401.58, 262.6) * mm});
            skLineSegment(sketch, "E1603", {"start": v(-401.58, 262.6) * mm, "end": v(-402.09, 262.55) * mm});
            skLineSegment(sketch, "E1604", {"start": v(-402.09, 262.55) * mm, "end": v(-402.6, 262.51) * mm});
            skLineSegment(sketch, "E1605", {"start": v(-402.6, 262.51) * mm, "end": v(-403.11, 262.49) * mm});
            skLineSegment(sketch, "E1606", {"start": v(-403.11, 262.49) * mm, "end": v(-403.63, 262.47) * mm});
            skLineSegment(sketch, "E1607", {"start": v(-403.63, 262.47) * mm, "end": v(-404.14, 262.47) * mm});
            skLineSegment(sketch, "E1608", {"start": v(-404.14, 262.47) * mm, "end": v(-404.66, 262.48) * mm});
            skLineSegment(sketch, "E1609", {"start": v(-404.66, 262.48) * mm, "end": v(-405.22, 262.47) * mm});
            skLineSegment(sketch, "E1610", {"start": v(-405.22, 262.47) * mm, "end": v(-405.78, 262.46) * mm});
            skLineSegment(sketch, "E1611", {"start": v(-405.78, 262.46) * mm, "end": v(-406.34, 262.48) * mm});
            skLineSegment(sketch, "E1612", {"start": v(-406.34, 262.48) * mm, "end": v(-406.9, 262.5) * mm});
            skLineSegment(sketch, "E1613", {"start": v(-406.9, 262.5) * mm, "end": v(-407.45, 262.54) * mm});
            skLineSegment(sketch, "E1614", {"start": v(-407.45, 262.54) * mm, "end": v(-408, 262.6) * mm});
            skLineSegment(sketch, "E1615", {"start": v(-408, 262.6) * mm, "end": v(-408.56, 262.67) * mm});
            skLineSegment(sketch, "E1616", {"start": v(-408.56, 262.67) * mm, "end": v(-409.1, 262.75) * mm});
            skLineSegment(sketch, "E1617", {"start": v(-409.1, 262.75) * mm, "end": v(-409.65, 262.84) * mm});
            skLineSegment(sketch, "E1618", {"start": v(-409.65, 262.84) * mm, "end": v(-410.2, 262.95) * mm});
            skLineSegment(sketch, "E1619", {"start": v(-410.2, 262.95) * mm, "end": v(-410.74, 263.08) * mm});
            skLineSegment(sketch, "E1620", {"start": v(-410.74, 263.08) * mm, "end": v(-411.27, 263.21) * mm});
            skLineSegment(sketch, "E1621", {"start": v(-411.27, 263.21) * mm, "end": v(-411.8, 263.36) * mm});
            skLineSegment(sketch, "E1622", {"start": v(-411.8, 263.36) * mm, "end": v(-412.34, 263.52) * mm});
            skLineSegment(sketch, "E1623", {"start": v(-412.34, 263.52) * mm, "end": v(-412.86, 263.7) * mm});
            skLineSegment(sketch, "E1624", {"start": v(-412.86, 263.7) * mm, "end": v(-413.38, 263.89) * mm});
            skLineSegment(sketch, "E1625", {"start": v(-413.38, 263.89) * mm, "end": v(-413.9, 264.09) * mm});
            skLineSegment(sketch, "E1626", {"start": v(-413.9, 264.09) * mm, "end": v(-414.4, 264.3) * mm});
            skLineSegment(sketch, "E1627", {"start": v(-414.4, 264.3) * mm, "end": v(-414.91, 264.53) * mm});
            skLineSegment(sketch, "E1628", {"start": v(-414.91, 264.53) * mm, "end": v(-415.4, 264.77) * mm});
            skLineSegment(sketch, "E1629", {"start": v(-415.4, 264.77) * mm, "end": v(-415.9, 265.02) * mm});
            skLineSegment(sketch, "E1630", {"start": v(-415.9, 265.02) * mm, "end": v(-416.4, 265.28) * mm});
            skLineSegment(sketch, "E1631", {"start": v(-416.4, 265.28) * mm, "end": v(-416.87, 265.56) * mm});
            skLineSegment(sketch, "E1632", {"start": v(-416.87, 265.56) * mm, "end": v(-417.35, 265.84) * mm});
            skLineSegment(sketch, "E1633", {"start": v(-417.35, 265.84) * mm, "end": v(-417.81, 266.14) * mm});
            skLineSegment(sketch, "E1634", {"start": v(-417.81, 266.14) * mm, "end": v(-418.27, 266.46) * mm});
            skLineSegment(sketch, "E1635", {"start": v(-418.27, 266.46) * mm, "end": v(-418.73, 266.78) * mm});
            skLineSegment(sketch, "E1636", {"start": v(-418.73, 266.78) * mm, "end": v(-419.17, 267.11) * mm});
            skLineSegment(sketch, "E1637", {"start": v(-419.17, 267.11) * mm, "end": v(-419.6, 267.46) * mm});
            skLineSegment(sketch, "E1638", {"start": v(-419.6, 267.46) * mm, "end": v(-420.04, 267.82) * mm});
            skLineSegment(sketch, "E1639", {"start": v(-420.04, 267.82) * mm, "end": v(-420.46, 268.2) * mm});
            skLineSegment(sketch, "E1640", {"start": v(-420.46, 268.2) * mm, "end": v(-420.87, 268.57) * mm});
            skLineSegment(sketch, "E1641", {"start": v(-420.87, 268.57) * mm, "end": v(-421.16, 268.86) * mm});
            skLineSegment(sketch, "E1642", {"start": v(-421.16, 268.86) * mm, "end": v(-421.44, 269.15) * mm});
            skLineSegment(sketch, "E1643", {"start": v(-421.44, 269.15) * mm, "end": v(-421.72, 269.45) * mm});
            skLineSegment(sketch, "E1644", {"start": v(-421.72, 269.45) * mm, "end": v(-421.98, 269.76) * mm});
            skLineSegment(sketch, "E1645", {"start": v(-421.98, 269.76) * mm, "end": v(-422.24, 270.07) * mm});
            skLineSegment(sketch, "E1646", {"start": v(-422.24, 270.07) * mm, "end": v(-422.49, 270.39) * mm});
            skLineSegment(sketch, "E1647", {"start": v(-422.49, 270.39) * mm, "end": v(-422.73, 270.71) * mm});
            skLineSegment(sketch, "E1648", {"start": v(-422.73, 270.71) * mm, "end": v(-422.96, 271.04) * mm});
            skLineSegment(sketch, "E1649", {"start": v(-422.96, 271.04) * mm, "end": v(-423.18, 271.38) * mm});
            skLineSegment(sketch, "E1650", {"start": v(-423.18, 271.38) * mm, "end": v(-423.4, 271.72) * mm});
            skLineSegment(sketch, "E1651", {"start": v(-423.4, 271.72) * mm, "end": v(-423.6, 272.06) * mm});
            skLineSegment(sketch, "E1652", {"start": v(-423.6, 272.06) * mm, "end": v(-423.8, 272.41) * mm});
            skLineSegment(sketch, "E1653", {"start": v(-423.8, 272.41) * mm, "end": v(-423.98, 272.77) * mm});
            skLineSegment(sketch, "E1654", {"start": v(-423.98, 272.77) * mm, "end": v(-424.16, 273.13) * mm});
            skLineSegment(sketch, "E1655", {"start": v(-424.16, 273.13) * mm, "end": v(-424.33, 273.5) * mm});
            skLineSegment(sketch, "E1656", {"start": v(-424.33, 273.5) * mm, "end": v(-424.49, 273.86) * mm});
            skLineSegment(sketch, "E1657", {"start": v(-424.49, 273.86) * mm, "end": v(-424.64, 274.23) * mm});
            skLineSegment(sketch, "E1658", {"start": v(-424.64, 274.23) * mm, "end": v(-424.78, 274.6) * mm});
            skLineSegment(sketch, "E1659", {"start": v(-424.78, 274.6) * mm, "end": v(-424.9, 274.99) * mm});
            skLineSegment(sketch, "E1660", {"start": v(-424.9, 274.99) * mm, "end": v(-425.03, 275.37) * mm});
            skLineSegment(sketch, "E1661", {"start": v(-425.03, 275.37) * mm, "end": v(-425.14, 275.76) * mm});
            skLineSegment(sketch, "E1662", {"start": v(-425.14, 275.76) * mm, "end": v(-425.24, 276.14) * mm});
            skLineSegment(sketch, "E1663", {"start": v(-425.24, 276.14) * mm, "end": v(-425.33, 276.54) * mm});
            skLineSegment(sketch, "E1664", {"start": v(-425.33, 276.54) * mm, "end": v(-425.41, 276.93) * mm});
            skLineSegment(sketch, "E1665", {"start": v(-425.41, 276.93) * mm, "end": v(-425.49, 277.33) * mm});
            skLineSegment(sketch, "E1666", {"start": v(-425.49, 277.33) * mm, "end": v(-425.55, 277.72) * mm});
            skLineSegment(sketch, "E1667", {"start": v(-425.55, 277.72) * mm, "end": v(-425.6, 278.13) * mm});
            skLineSegment(sketch, "E1668", {"start": v(-425.6, 278.13) * mm, "end": v(-425.64, 278.53) * mm});
            skLineSegment(sketch, "E1669", {"start": v(-425.64, 278.53) * mm, "end": v(-425.67, 278.93) * mm});
            skLineSegment(sketch, "E1670", {"start": v(-425.67, 278.93) * mm, "end": v(-425.69, 279.34) * mm});
            skLineSegment(sketch, "E1671", {"start": v(-425.69, 279.34) * mm, "end": v(-425.7, 279.74) * mm});
            skLineSegment(sketch, "E1672", {"start": v(-425.7, 279.74) * mm, "end": v(-425.7, 280.15) * mm});
            skLineSegment(sketch, "E1673", {"start": v(-425.7, 280.15) * mm, "end": v(-425.7, 280.57) * mm});
            skLineSegment(sketch, "E1674", {"start": v(-425.7, 280.57) * mm, "end": v(-425.68, 280.98) * mm});
            skLineSegment(sketch, "E1675", {"start": v(-425.68, 280.98) * mm, "end": v(-425.65, 281.4) * mm});
            skLineSegment(sketch, "E1676", {"start": v(-425.65, 281.4) * mm, "end": v(-425.62, 281.8) * mm});
            skLineSegment(sketch, "E1677", {"start": v(-425.62, 281.8) * mm, "end": v(-425.57, 282.2) * mm});
            skLineSegment(sketch, "E1678", {"start": v(-425.57, 282.2) * mm, "end": v(-425.51, 282.62) * mm});
            skLineSegment(sketch, "E1679", {"start": v(-425.51, 282.62) * mm, "end": v(-425.45, 283.02) * mm});
            skLineSegment(sketch, "E1680", {"start": v(-425.45, 283.02) * mm, "end": v(-425.37, 283.42) * mm});
            skLineSegment(sketch, "E1681", {"start": v(-425.37, 283.42) * mm, "end": v(-425.28, 283.82) * mm});
            skLineSegment(sketch, "E1682", {"start": v(-425.28, 283.82) * mm, "end": v(-425.18, 284.22) * mm});
            skLineSegment(sketch, "E1683", {"start": v(-425.18, 284.22) * mm, "end": v(-425.07, 284.61) * mm});
            skLineSegment(sketch, "E1684", {"start": v(-425.07, 284.61) * mm, "end": v(-424.96, 285) * mm});
            skLineSegment(sketch, "E1685", {"start": v(-424.96, 285) * mm, "end": v(-424.83, 285.4) * mm});
            skLineSegment(sketch, "E1686", {"start": v(-424.83, 285.4) * mm, "end": v(-424.7, 285.78) * mm});
            skLineSegment(sketch, "E1687", {"start": v(-424.7, 285.78) * mm, "end": v(-424.54, 286.16) * mm});
            skLineSegment(sketch, "E1688", {"start": v(-424.54, 286.16) * mm, "end": v(-424.39, 286.53) * mm});
            skLineSegment(sketch, "E1689", {"start": v(-424.39, 286.53) * mm, "end": v(-424.22, 286.9) * mm});
            skLineSegment(sketch, "E1690", {"start": v(-424.22, 286.9) * mm, "end": v(-424.05, 287.27) * mm});
            skLineSegment(sketch, "E1691", {"start": v(-424.05, 287.27) * mm, "end": v(-423.86, 287.64) * mm});
            skLineSegment(sketch, "E1692", {"start": v(-423.86, 287.64) * mm, "end": v(-423.67, 288) * mm});
            skLineSegment(sketch, "E1693", {"start": v(-423.67, 288) * mm, "end": v(-423.46, 288.35) * mm});
            skLineSegment(sketch, "E1694", {"start": v(-423.46, 288.35) * mm, "end": v(-423.25, 288.7) * mm});
            skLineSegment(sketch, "E1695", {"start": v(-423.25, 288.7) * mm, "end": v(-423.03, 289.04) * mm});
            skLineSegment(sketch, "E1696", {"start": v(-423.03, 289.04) * mm, "end": v(-422.8, 289.38) * mm});
            skLineSegment(sketch, "E1697", {"start": v(-422.8, 289.38) * mm, "end": v(-422.56, 289.71) * mm});
            skLineSegment(sketch, "E1698", {"start": v(-422.56, 289.71) * mm, "end": v(-422.31, 290.04) * mm});
            skLineSegment(sketch, "E1699", {"start": v(-422.31, 290.04) * mm, "end": v(-422.06, 290.36) * mm});
            skLineSegment(sketch, "E1700", {"start": v(-422.06, 290.36) * mm, "end": v(-421.79, 290.67) * mm});
            skLineSegment(sketch, "E1701", {"start": v(-421.79, 290.67) * mm, "end": v(-421.52, 290.98) * mm});
            skLineSegment(sketch, "E1702", {"start": v(-421.52, 290.98) * mm, "end": v(-421.23, 291.28) * mm});
            skLineSegment(sketch, "E1703", {"start": v(-421.23, 291.28) * mm, "end": v(-420.94, 291.57) * mm});
            skLineSegment(sketch, "E1704", {"start": v(-420.94, 291.57) * mm, "end": v(-420.64, 291.86) * mm});
            skLineSegment(sketch, "E1705", {"start": v(-420.64, 291.86) * mm, "end": v(-420.23, 292.23) * mm});
            skLineSegment(sketch, "E1706", {"start": v(-420.23, 292.23) * mm, "end": v(-419.82, 292.59) * mm});
            skLineSegment(sketch, "E1707", {"start": v(-419.82, 292.59) * mm, "end": v(-419.4, 292.94) * mm});
            skLineSegment(sketch, "E1708", {"start": v(-419.4, 292.94) * mm, "end": v(-418.96, 293.27) * mm});
            skLineSegment(sketch, "E1709", {"start": v(-418.96, 293.27) * mm, "end": v(-418.51, 293.6) * mm});
            skLineSegment(sketch, "E1710", {"start": v(-418.51, 293.6) * mm, "end": v(-418.07, 293.91) * mm});
            skLineSegment(sketch, "E1711", {"start": v(-418.07, 293.91) * mm, "end": v(-417.61, 294.21) * mm});
            skLineSegment(sketch, "E1712", {"start": v(-417.61, 294.21) * mm, "end": v(-417.15, 294.5) * mm});
            skLineSegment(sketch, "E1713", {"start": v(-417.15, 294.5) * mm, "end": v(-416.68, 294.78) * mm});
            skLineSegment(sketch, "E1714", {"start": v(-416.68, 294.78) * mm, "end": v(-416.2, 295.05) * mm});
            skLineSegment(sketch, "E1715", {"start": v(-416.2, 295.05) * mm, "end": v(-415.72, 295.3) * mm});
            skLineSegment(sketch, "E1716", {"start": v(-415.72, 295.3) * mm, "end": v(-415.23, 295.54) * mm});
            skLineSegment(sketch, "E1717", {"start": v(-415.23, 295.54) * mm, "end": v(-414.74, 295.77) * mm});
            skLineSegment(sketch, "E1718", {"start": v(-414.74, 295.77) * mm, "end": v(-414.24, 296) * mm});
            skLineSegment(sketch, "E1719", {"start": v(-414.24, 296) * mm, "end": v(-413.74, 296.2) * mm});
            skLineSegment(sketch, "E1720", {"start": v(-413.74, 296.2) * mm, "end": v(-413.23, 296.39) * mm});
            skLineSegment(sketch, "E1721", {"start": v(-413.23, 296.39) * mm, "end": v(-412.71, 296.57) * mm});
            skLineSegment(sketch, "E1722", {"start": v(-412.71, 296.57) * mm, "end": v(-412.2, 296.74) * mm});
            skLineSegment(sketch, "E1723", {"start": v(-412.2, 296.74) * mm, "end": v(-411.67, 296.89) * mm});
            skLineSegment(sketch, "E1724", {"start": v(-411.67, 296.89) * mm, "end": v(-411.15, 297.03) * mm});
            skLineSegment(sketch, "E1725", {"start": v(-411.15, 297.03) * mm, "end": v(-410.62, 297.16) * mm});
            skLineSegment(sketch, "E1726", {"start": v(-410.62, 297.16) * mm, "end": v(-410.09, 297.28) * mm});
            skLineSegment(sketch, "E1727", {"start": v(-410.09, 297.28) * mm, "end": v(-409.55, 297.38) * mm});
            skLineSegment(sketch, "E1728", {"start": v(-409.55, 297.38) * mm, "end": v(-409.01, 297.47) * mm});
            skLineSegment(sketch, "E1729", {"start": v(-409.01, 297.47) * mm, "end": v(-408.47, 297.54) * mm});
            skLineSegment(sketch, "E1730", {"start": v(-408.47, 297.54) * mm, "end": v(-407.93, 297.6) * mm});
            skLineSegment(sketch, "E1731", {"start": v(-407.93, 297.6) * mm, "end": v(-407.38, 297.66) * mm});
            skLineSegment(sketch, "E1732", {"start": v(-407.38, 297.66) * mm, "end": v(-406.84, 297.7) * mm});
            skLineSegment(sketch, "E1733", {"start": v(-406.84, 297.7) * mm, "end": v(-406.29, 297.71) * mm});
            skLineSegment(sketch, "E1734", {"start": v(-406.29, 297.71) * mm, "end": v(-405.74, 297.72) * mm});
            skLineSegment(sketch, "E1735", {"start": v(-405.74, 297.72) * mm, "end": v(-405.19, 297.72) * mm});
            skLineSegment(sketch, "E1736", {"start": v(-405.19, 297.72) * mm, "end": v(-404.64, 297.7) * mm});
            skLineSegment(sketch, "E1737", {"start": v(-404.64, 297.7) * mm, "end": v(-404.12, 297.7) * mm});
            skLineSegment(sketch, "E1738", {"start": v(-404.12, 297.7) * mm, "end": v(-403.6, 297.7) * mm});
            skLineSegment(sketch, "E1739", {"start": v(-403.6, 297.7) * mm, "end": v(-403.1, 297.68) * mm});
            skLineSegment(sketch, "E1740", {"start": v(-403.1, 297.68) * mm, "end": v(-402.58, 297.65) * mm});
            skLineSegment(sketch, "E1741", {"start": v(-402.58, 297.65) * mm, "end": v(-402.07, 297.6) * mm});
            skLineSegment(sketch, "E1742", {"start": v(-402.07, 297.6) * mm, "end": v(-401.57, 297.55) * mm});
            skLineSegment(sketch, "E1743", {"start": v(-401.57, 297.55) * mm, "end": v(-401.06, 297.48) * mm});
            skLineSegment(sketch, "E1744", {"start": v(-401.06, 297.48) * mm, "end": v(-400.56, 297.4) * mm});
            skLineSegment(sketch, "E1745", {"start": v(-400.56, 297.4) * mm, "end": v(-400.06, 297.3) * mm});
            skLineSegment(sketch, "E1746", {"start": v(-400.06, 297.3) * mm, "end": v(-399.56, 297.2) * mm});
            skLineSegment(sketch, "E1747", {"start": v(-399.56, 297.2) * mm, "end": v(-399.07, 297.08) * mm});
            skLineSegment(sketch, "E1748", {"start": v(-399.07, 297.08) * mm, "end": v(-398.58, 296.95) * mm});
            skLineSegment(sketch, "E1749", {"start": v(-398.58, 296.95) * mm, "end": v(-398.09, 296.81) * mm});
            skLineSegment(sketch, "E1750", {"start": v(-398.09, 296.81) * mm, "end": v(-397.6, 296.66) * mm});
            skLineSegment(sketch, "E1751", {"start": v(-397.6, 296.66) * mm, "end": v(-397.13, 296.5) * mm});
            skLineSegment(sketch, "E1752", {"start": v(-397.13, 296.5) * mm, "end": v(-396.65, 296.31) * mm});
            skLineSegment(sketch, "E1753", {"start": v(-396.65, 296.31) * mm, "end": v(-396.18, 296.12) * mm});
            skLineSegment(sketch, "E1754", {"start": v(-396.18, 296.12) * mm, "end": v(-395.72, 295.92) * mm});
            skLineSegment(sketch, "E1755", {"start": v(-395.72, 295.92) * mm, "end": v(-395.26, 295.7) * mm});
            skLineSegment(sketch, "E1756", {"start": v(-395.26, 295.7) * mm, "end": v(-394.8, 295.48) * mm});
            skLineSegment(sketch, "E1757", {"start": v(-394.8, 295.48) * mm, "end": v(-394.35, 295.25) * mm});
            skLineSegment(sketch, "E1758", {"start": v(-394.35, 295.25) * mm, "end": v(-393.9, 295) * mm});
            skLineSegment(sketch, "E1759", {"start": v(-393.9, 295) * mm, "end": v(-393.47, 294.74) * mm});
            skLineSegment(sketch, "E1760", {"start": v(-393.47, 294.74) * mm, "end": v(-393.04, 294.47) * mm});
            skLineSegment(sketch, "E1761", {"start": v(-393.04, 294.47) * mm, "end": v(-392.61, 294.2) * mm});
            skLineSegment(sketch, "E1762", {"start": v(-392.61, 294.2) * mm, "end": v(-392.2, 293.9) * mm});
            skLineSegment(sketch, "E1763", {"start": v(-392.2, 293.9) * mm, "end": v(-391.78, 293.6) * mm});
            skLineSegment(sketch, "E1764", {"start": v(-391.78, 293.6) * mm, "end": v(-391.38, 293.29) * mm});
            skLineSegment(sketch, "E1765", {"start": v(-391.38, 293.29) * mm, "end": v(-390.98, 292.96) * mm});
            skLineSegment(sketch, "E1766", {"start": v(-390.98, 292.96) * mm, "end": v(-390.59, 292.63) * mm});
            skLineSegment(sketch, "E1767", {"start": v(-390.59, 292.63) * mm, "end": v(-390.2, 292.29) * mm});
            skLineSegment(sketch, "E1768", {"start": v(-390.2, 292.29) * mm, "end": v(-389.83, 291.93) * mm});
            skLineSegment(sketch, "E1769", {"start": v(-389.83, 291.93) * mm, "end": v(-389.54, 291.64) * mm});
            skLineSegment(sketch, "E1770", {"start": v(-389.54, 291.64) * mm, "end": v(-389.26, 291.34) * mm});
            skLineSegment(sketch, "E1771", {"start": v(-389.26, 291.34) * mm, "end": v(-388.98, 291.03) * mm});
            skLineSegment(sketch, "E1772", {"start": v(-388.98, 291.03) * mm, "end": v(-388.72, 290.72) * mm});
            skLineSegment(sketch, "E1773", {"start": v(-388.72, 290.72) * mm, "end": v(-388.46, 290.4) * mm});
            skLineSegment(sketch, "E1774", {"start": v(-388.46, 290.4) * mm, "end": v(-388.2, 290.07) * mm});
            skLineSegment(sketch, "E1775", {"start": v(-388.2, 290.07) * mm, "end": v(-387.97, 289.74) * mm});
            skLineSegment(sketch, "E1776", {"start": v(-387.97, 289.74) * mm, "end": v(-387.74, 289.4) * mm});
            skLineSegment(sketch, "E1777", {"start": v(-387.74, 289.4) * mm, "end": v(-387.51, 289.06) * mm});
            skLineSegment(sketch, "E1778", {"start": v(-387.51, 289.06) * mm, "end": v(-387.3, 288.72) * mm});
            skLineSegment(sketch, "E1779", {"start": v(-387.3, 288.72) * mm, "end": v(-387.09, 288.36) * mm});
            skLineSegment(sketch, "E1780", {"start": v(-387.09, 288.36) * mm, "end": v(-386.9, 288) * mm});
            skLineSegment(sketch, "E1781", {"start": v(-386.9, 288) * mm, "end": v(-386.7, 287.64) * mm});
            skLineSegment(sketch, "E1782", {"start": v(-386.7, 287.64) * mm, "end": v(-386.52, 287.28) * mm});
            skLineSegment(sketch, "E1783", {"start": v(-386.52, 287.28) * mm, "end": v(-386.35, 286.9) * mm});
            skLineSegment(sketch, "E1784", {"start": v(-386.35, 286.9) * mm, "end": v(-386.2, 286.53) * mm});
            skLineSegment(sketch, "E1785", {"start": v(-386.2, 286.53) * mm, "end": v(-386.04, 286.15) * mm});
            skLineSegment(sketch, "E1786", {"start": v(-386.04, 286.15) * mm, "end": v(-385.9, 285.77) * mm});
            skLineSegment(sketch, "E1787", {"start": v(-385.9, 285.77) * mm, "end": v(-385.77, 285.39) * mm});
            skLineSegment(sketch, "E1788", {"start": v(-385.77, 285.39) * mm, "end": v(-385.64, 285) * mm});
            skLineSegment(sketch, "E1789", {"start": v(-385.64, 285) * mm, "end": v(-385.53, 284.6) * mm});
            skLineSegment(sketch, "E1790", {"start": v(-385.53, 284.6) * mm, "end": v(-385.42, 284.21) * mm});
            skLineSegment(sketch, "E1791", {"start": v(-385.42, 284.21) * mm, "end": v(-385.33, 283.81) * mm});
            skLineSegment(sketch, "E1792", {"start": v(-385.33, 283.81) * mm, "end": v(-385.25, 283.41) * mm});
            skLineSegment(sketch, "E1793", {"start": v(-385.25, 283.41) * mm, "end": v(-385.17, 283.01) * mm});
            skLineSegment(sketch, "E1794", {"start": v(-385.17, 283.01) * mm, "end": v(-385.1, 282.6) * mm});
            skLineSegment(sketch, "E1795", {"start": v(-385.1, 282.6) * mm, "end": v(-385.05, 282.2) * mm});
            skLineSegment(sketch, "E1796", {"start": v(-385.05, 282.2) * mm, "end": v(-385, 281.8) * mm});
            skLineSegment(sketch, "E1797", {"start": v(-385, 281.8) * mm, "end": v(-384.97, 281.38) * mm});
            skLineSegment(sketch, "E1798", {"start": v(-384.97, 281.38) * mm, "end": v(-384.95, 280.97) * mm});
            skLineSegment(sketch, "E1799", {"start": v(-384.95, 280.97) * mm, "end": v(-384.94, 280.56) * mm});
            skLineSegment(sketch, "E1800", {"start": v(-384.94, 280.56) * mm, "end": v(-384.93, 280.14) * mm});
            skLineSegment(sketch, "E1801", {"start": v(-385.5, 306.72) * mm, "end": v(-425.45, 306.72) * mm});
            skLineSegment(sketch, "E1802", {"start": v(-425.45, 306.72) * mm, "end": v(-425.45, 324.28) * mm});
            skLineSegment(sketch, "E1803", {"start": v(-425.45, 324.28) * mm, "end": v(-425.45, 324.77) * mm});
            skLineSegment(sketch, "E1804", {"start": v(-425.45, 324.77) * mm, "end": v(-425.42, 325.26) * mm});
            skLineSegment(sketch, "E1805", {"start": v(-425.42, 325.26) * mm, "end": v(-425.37, 325.75) * mm});
            skLineSegment(sketch, "E1806", {"start": v(-425.37, 325.75) * mm, "end": v(-425.29, 326.23) * mm});
            skLineSegment(sketch, "E1807", {"start": v(-425.29, 326.23) * mm, "end": v(-425.19, 326.71) * mm});
            skLineSegment(sketch, "E1808", {"start": v(-425.19, 326.71) * mm, "end": v(-425.06, 327.18) * mm});
            skLineSegment(sketch, "E1809", {"start": v(-425.06, 327.18) * mm, "end": v(-424.9, 327.64) * mm});
            skLineSegment(sketch, "E1810", {"start": v(-424.9, 327.64) * mm, "end": v(-424.73, 328.1) * mm});
            skLineSegment(sketch, "E1811", {"start": v(-424.73, 328.1) * mm, "end": v(-424.54, 328.54) * mm});
            skLineSegment(sketch, "E1812", {"start": v(-424.54, 328.54) * mm, "end": v(-424.32, 328.98) * mm});
            skLineSegment(sketch, "E1813", {"start": v(-424.32, 328.98) * mm, "end": v(-424.08, 329.4) * mm});
            skLineSegment(sketch, "E1814", {"start": v(-424.08, 329.4) * mm, "end": v(-423.81, 329.81) * mm});
            skLineSegment(sketch, "E1815", {"start": v(-423.81, 329.81) * mm, "end": v(-423.53, 330.21) * mm});
            skLineSegment(sketch, "E1816", {"start": v(-423.53, 330.21) * mm, "end": v(-423.22, 330.6) * mm});
            skLineSegment(sketch, "E1817", {"start": v(-423.22, 330.6) * mm, "end": v(-422.9, 330.97) * mm});
            skLineSegment(sketch, "E1818", {"start": v(-422.9, 330.97) * mm, "end": v(-422.55, 331.32) * mm});
            skLineSegment(sketch, "E1819", {"start": v(-422.55, 331.32) * mm, "end": v(-422.2, 331.66) * mm});
            skLineSegment(sketch, "E1820", {"start": v(-422.2, 331.66) * mm, "end": v(-421.83, 331.98) * mm});
            skLineSegment(sketch, "E1821", {"start": v(-421.83, 331.98) * mm, "end": v(-421.45, 332.28) * mm});
            skLineSegment(sketch, "E1822", {"start": v(-421.45, 332.28) * mm, "end": v(-421.06, 332.56) * mm});
            skLineSegment(sketch, "E1823", {"start": v(-421.06, 332.56) * mm, "end": v(-420.65, 332.82) * mm});
            skLineSegment(sketch, "E1824", {"start": v(-420.65, 332.82) * mm, "end": v(-420.23, 333.06) * mm});
            skLineSegment(sketch, "E1825", {"start": v(-420.23, 333.06) * mm, "end": v(-419.8, 333.28) * mm});
            skLineSegment(sketch, "E1826", {"start": v(-419.8, 333.28) * mm, "end": v(-419.36, 333.48) * mm});
            skLineSegment(sketch, "E1827", {"start": v(-419.36, 333.48) * mm, "end": v(-418.9, 333.66) * mm});
            skLineSegment(sketch, "E1828", {"start": v(-418.9, 333.66) * mm, "end": v(-418.45, 333.8) * mm});
            skLineSegment(sketch, "E1829", {"start": v(-418.45, 333.8) * mm, "end": v(-417.99, 333.94) * mm});
            skLineSegment(sketch, "E1830", {"start": v(-417.99, 333.94) * mm, "end": v(-417.51, 334.05) * mm});
            skLineSegment(sketch, "E1831", {"start": v(-417.51, 334.05) * mm, "end": v(-417.04, 334.13) * mm});
            skLineSegment(sketch, "E1832", {"start": v(-417.04, 334.13) * mm, "end": v(-416.55, 334.19) * mm});
            skLineSegment(sketch, "E1833", {"start": v(-416.55, 334.19) * mm, "end": v(-416.07, 334.23) * mm});
            skLineSegment(sketch, "E1834", {"start": v(-416.07, 334.23) * mm, "end": v(-415.58, 334.24) * mm});
            skLineSegment(sketch, "E1835", {"start": v(-415.58, 334.24) * mm, "end": v(-415.08, 334.24) * mm});
            skLineSegment(sketch, "E1836", {"start": v(-415.08, 334.24) * mm, "end": v(-414.58, 334.22) * mm});
            skLineSegment(sketch, "E1837", {"start": v(-414.58, 334.22) * mm, "end": v(-414.08, 334.17) * mm});
            skLineSegment(sketch, "E1838", {"start": v(-414.08, 334.17) * mm, "end": v(-413.59, 334.1) * mm});
            skLineSegment(sketch, "E1839", {"start": v(-413.59, 334.1) * mm, "end": v(-413.1, 334) * mm});
            skLineSegment(sketch, "E1840", {"start": v(-413.1, 334) * mm, "end": v(-412.62, 333.88) * mm});
            skLineSegment(sketch, "E1841", {"start": v(-412.62, 333.88) * mm, "end": v(-412.15, 333.73) * mm});
            skLineSegment(sketch, "E1842", {"start": v(-412.15, 333.73) * mm, "end": v(-411.69, 333.56) * mm});
            skLineSegment(sketch, "E1843", {"start": v(-411.69, 333.56) * mm, "end": v(-411.23, 333.37) * mm});
            skLineSegment(sketch, "E1844", {"start": v(-411.23, 333.37) * mm, "end": v(-410.79, 333.15) * mm});
            skLineSegment(sketch, "E1845", {"start": v(-410.79, 333.15) * mm, "end": v(-410.35, 332.91) * mm});
            skLineSegment(sketch, "E1846", {"start": v(-410.35, 332.91) * mm, "end": v(-409.93, 332.65) * mm});
            skLineSegment(sketch, "E1847", {"start": v(-409.93, 332.65) * mm, "end": v(-409.52, 332.37) * mm});
            skLineSegment(sketch, "E1848", {"start": v(-409.52, 332.37) * mm, "end": v(-409.13, 332.07) * mm});
            skLineSegment(sketch, "E1849", {"start": v(-409.13, 332.07) * mm, "end": v(-408.75, 331.74) * mm});
            skLineSegment(sketch, "E1850", {"start": v(-408.75, 331.74) * mm, "end": v(-408.38, 331.4) * mm});
            skLineSegment(sketch, "E1851", {"start": v(-408.38, 331.4) * mm, "end": v(-408.04, 331.04) * mm});
            skLineSegment(sketch, "E1852", {"start": v(-408.04, 331.04) * mm, "end": v(-407.71, 330.66) * mm});
            skLineSegment(sketch, "E1853", {"start": v(-407.71, 330.66) * mm, "end": v(-407.41, 330.27) * mm});
            skLineSegment(sketch, "E1854", {"start": v(-407.41, 330.27) * mm, "end": v(-407.13, 329.87) * mm});
            skLineSegment(sketch, "E1855", {"start": v(-407.13, 329.87) * mm, "end": v(-406.87, 329.45) * mm});
            skLineSegment(sketch, "E1856", {"start": v(-406.87, 329.45) * mm, "end": v(-406.63, 329.02) * mm});
            skLineSegment(sketch, "E1857", {"start": v(-406.63, 329.02) * mm, "end": v(-406.4, 328.58) * mm});
            skLineSegment(sketch, "E1858", {"start": v(-406.4, 328.58) * mm, "end": v(-406.21, 328.13) * mm});
            skLineSegment(sketch, "E1859", {"start": v(-406.21, 328.13) * mm, "end": v(-406.04, 327.67) * mm});
            skLineSegment(sketch, "E1860", {"start": v(-406.04, 327.67) * mm, "end": v(-405.89, 327.2) * mm});
            skLineSegment(sketch, "E1861", {"start": v(-405.89, 327.2) * mm, "end": v(-405.76, 326.73) * mm});
            skLineSegment(sketch, "E1862", {"start": v(-405.76, 326.73) * mm, "end": v(-405.65, 326.25) * mm});
            skLineSegment(sketch, "E1863", {"start": v(-405.65, 326.25) * mm, "end": v(-405.57, 325.76) * mm});
            skLineSegment(sketch, "E1864", {"start": v(-405.57, 325.76) * mm, "end": v(-405.52, 325.27) * mm});
            skLineSegment(sketch, "E1865", {"start": v(-405.52, 325.27) * mm, "end": v(-405.49, 324.77) * mm});
            skLineSegment(sketch, "E1866", {"start": v(-405.49, 324.77) * mm, "end": v(-405.48, 324.28) * mm});
            skLineSegment(sketch, "E1867", {"start": v(-405.48, 324.28) * mm, "end": v(-405.48, 306.72) * mm});
            skLineSegment(sketch, "E1868", {"start": v(-405.48, 324.28) * mm, "end": v(-405.48, 324.69) * mm});
            skLineSegment(sketch, "E1869", {"start": v(-405.48, 324.69) * mm, "end": v(-405.46, 325.1) * mm});
            skLineSegment(sketch, "E1870", {"start": v(-405.46, 325.1) * mm, "end": v(-405.42, 325.5) * mm});
            skLineSegment(sketch, "E1871", {"start": v(-405.42, 325.5) * mm, "end": v(-405.35, 325.9) * mm});
            skLineSegment(sketch, "E1872", {"start": v(-405.35, 325.9) * mm, "end": v(-405.27, 326.3) * mm});
            skLineSegment(sketch, "E1873", {"start": v(-405.27, 326.3) * mm, "end": v(-405.16, 326.69) * mm});
            skLineSegment(sketch, "E1874", {"start": v(-405.16, 326.69) * mm, "end": v(-405.04, 327.07) * mm});
            skLineSegment(sketch, "E1875", {"start": v(-405.04, 327.07) * mm, "end": v(-404.9, 327.45) * mm});
            skLineSegment(sketch, "E1876", {"start": v(-404.9, 327.45) * mm, "end": v(-404.74, 327.82) * mm});
            skLineSegment(sketch, "E1877", {"start": v(-404.74, 327.82) * mm, "end": v(-404.55, 328.18) * mm});
            skLineSegment(sketch, "E1878", {"start": v(-404.55, 328.18) * mm, "end": v(-404.36, 328.53) * mm});
            skLineSegment(sketch, "E1879", {"start": v(-404.36, 328.53) * mm, "end": v(-404.14, 328.87) * mm});
            skLineSegment(sketch, "E1880", {"start": v(-404.14, 328.87) * mm, "end": v(-403.9, 329.2) * mm});
            skLineSegment(sketch, "E1881", {"start": v(-403.9, 329.2) * mm, "end": v(-403.65, 329.53) * mm});
            skLineSegment(sketch, "E1882", {"start": v(-403.65, 329.53) * mm, "end": v(-403.39, 329.83) * mm});
            skLineSegment(sketch, "E1883", {"start": v(-403.39, 329.83) * mm, "end": v(-403.1, 330.13) * mm});
            skLineSegment(sketch, "E1884", {"start": v(-403.1, 330.13) * mm, "end": v(-402.6, 330.47) * mm});
            skLineSegment(sketch, "E1885", {"start": v(-402.6, 330.47) * mm, "end": v(-402.09, 330.79) * mm});
            skLineSegment(sketch, "E1886", {"start": v(-402.09, 330.79) * mm, "end": v(-401.56, 331.08) * mm});
            skLineSegment(sketch, "E1887", {"start": v(-401.56, 331.08) * mm, "end": v(-401.02, 331.35) * mm});
            skLineSegment(sketch, "E1888", {"start": v(-401.02, 331.35) * mm, "end": v(-400.48, 331.6) * mm});
            skLineSegment(sketch, "E1889", {"start": v(-400.48, 331.6) * mm, "end": v(-399.92, 331.81) * mm});
            skLineSegment(sketch, "E1890", {"start": v(-399.92, 331.81) * mm, "end": v(-399.35, 332) * mm});
            skLineSegment(sketch, "E1891", {"start": v(-399.35, 332) * mm, "end": v(-398.78, 332.18) * mm});
            skLineSegment(sketch, "E1892", {"start": v(-398.78, 332.18) * mm, "end": v(-398.2, 332.32) * mm});
            skLineSegment(sketch, "E1893", {"start": v(-398.2, 332.32) * mm, "end": v(-397.61, 332.44) * mm});
            skLineSegment(sketch, "E1894", {"start": v(-397.61, 332.44) * mm, "end": v(-397.02, 332.53) * mm});
            skLineSegment(sketch, "E1895", {"start": v(-397.02, 332.53) * mm, "end": v(-396.42, 332.6) * mm});
            skLineSegment(sketch, "E1896", {"start": v(-396.42, 332.6) * mm, "end": v(-395.82, 332.63) * mm});
            skLineSegment(sketch, "E1897", {"start": v(-395.82, 332.63) * mm, "end": v(-395.22, 332.65) * mm});
            skLineSegment(sketch, "E1898", {"start": v(-395.22, 332.65) * mm, "end": v(-394.62, 332.63) * mm});
            skLineSegment(sketch, "E1899", {"start": v(-394.62, 332.63) * mm, "end": v(-394.01, 332.59) * mm});
            skLineSegment(sketch, "E1900", {"start": v(-394.01, 332.59) * mm, "end": v(-393.48, 332.58) * mm});
            skLineSegment(sketch, "E1901", {"start": v(-393.48, 332.58) * mm, "end": v(-392.94, 332.58) * mm});
            skLineSegment(sketch, "E1902", {"start": v(-392.94, 332.58) * mm, "end": v(-392.4, 332.6) * mm});
            skLineSegment(sketch, "E1903", {"start": v(-392.4, 332.6) * mm, "end": v(-391.86, 332.62) * mm});
            skLineSegment(sketch, "E1904", {"start": v(-391.86, 332.62) * mm, "end": v(-391.33, 332.65) * mm});
            skLineSegment(sketch, "E1905", {"start": v(-391.33, 332.65) * mm, "end": v(-390.79, 332.69) * mm});
            skLineSegment(sketch, "E1906", {"start": v(-390.79, 332.69) * mm, "end": v(-390.25, 332.74) * mm});
            skLineSegment(sketch, "E1907", {"start": v(-390.25, 332.74) * mm, "end": v(-389.72, 332.8) * mm});
            skLineSegment(sketch, "E1908", {"start": v(-389.72, 332.8) * mm, "end": v(-389.18, 332.87) * mm});
            skLineSegment(sketch, "E1909", {"start": v(-389.18, 332.87) * mm, "end": v(-388.65, 332.95) * mm});
            skLineSegment(sketch, "E1910", {"start": v(-388.65, 332.95) * mm, "end": v(-388.12, 333.03) * mm});
            skLineSegment(sketch, "E1911", {"start": v(-388.12, 333.03) * mm, "end": v(-387.6, 333.13) * mm});
            skLineSegment(sketch, "E1912", {"start": v(-387.6, 333.13) * mm, "end": v(-387.06, 333.24) * mm});
            skLineSegment(sketch, "E1913", {"start": v(-387.06, 333.24) * mm, "end": v(-386.54, 333.36) * mm});
            skLineSegment(sketch, "E1914", {"start": v(-386.54, 333.36) * mm, "end": v(-386.01, 333.48) * mm});
            skLineSegment(sketch, "E1915", {"start": v(-386.01, 333.48) * mm, "end": v(-385.5, 333.62) * mm});
            skLineSegment(sketch, "E1916", {"start": v(-150.83, 345.3) * mm, "end": v(-110.84, 345.3) * mm});
            skLineSegment(sketch, "E1917", {"start": v(-110.84, 345.3) * mm, "end": v(-110.84, 320.43) * mm});
            skLineSegment(sketch, "E1918", {"start": v(-129.95, 345.3) * mm, "end": v(-129.95, 322.22) * mm});
            skLineSegment(sketch, "E1919", {"start": v(-150.8, 288.13) * mm, "end": v(-150.8, 311.63) * mm});
            skLineSegment(sketch, "E1920", {"start": v(-150.8, 311.63) * mm, "end": v(-110.86, 311.63) * mm});
            skLineSegment(sketch, "E1921", {"start": v(-151.37, 272.97) * mm, "end": v(-151.37, 273.39) * mm});
            skLineSegment(sketch, "E1922", {"start": v(-151.37, 273.39) * mm, "end": v(-151.36, 273.8) * mm});
            skLineSegment(sketch, "E1923", {"start": v(-151.36, 273.8) * mm, "end": v(-151.35, 274.23) * mm});
            skLineSegment(sketch, "E1924", {"start": v(-151.35, 274.23) * mm, "end": v(-151.32, 274.64) * mm});
            skLineSegment(sketch, "E1925", {"start": v(-151.32, 274.64) * mm, "end": v(-151.28, 275.06) * mm});
            skLineSegment(sketch, "E1926", {"start": v(-151.28, 275.06) * mm, "end": v(-151.23, 275.47) * mm});
            skLineSegment(sketch, "E1927", {"start": v(-151.23, 275.47) * mm, "end": v(-151.17, 275.88) * mm});
            skLineSegment(sketch, "E1928", {"start": v(-151.17, 275.88) * mm, "end": v(-151.1, 276.3) * mm});
            skLineSegment(sketch, "E1929", {"start": v(-151.1, 276.3) * mm, "end": v(-151.02, 276.7) * mm});
            skLineSegment(sketch, "E1930", {"start": v(-151.02, 276.7) * mm, "end": v(-150.93, 277.1) * mm});
            skLineSegment(sketch, "E1931", {"start": v(-150.93, 277.1) * mm, "end": v(-150.83, 277.5) * mm});
            skLineSegment(sketch, "E1932", {"start": v(-150.83, 277.5) * mm, "end": v(-150.72, 277.9) * mm});
            skLineSegment(sketch, "E1933", {"start": v(-150.72, 277.9) * mm, "end": v(-150.6, 278.3) * mm});
            skLineSegment(sketch, "E1934", {"start": v(-150.6, 278.3) * mm, "end": v(-150.48, 278.7) * mm});
            skLineSegment(sketch, "E1935", {"start": v(-150.48, 278.7) * mm, "end": v(-150.34, 279.08) * mm});
            skLineSegment(sketch, "E1936", {"start": v(-150.34, 279.08) * mm, "end": v(-150.19, 279.47) * mm});
            skLineSegment(sketch, "E1937", {"start": v(-150.19, 279.47) * mm, "end": v(-150.03, 279.85) * mm});
            skLineSegment(sketch, "E1938", {"start": v(-150.03, 279.85) * mm, "end": v(-149.86, 280.23) * mm});
            skLineSegment(sketch, "E1939", {"start": v(-149.86, 280.23) * mm, "end": v(-149.69, 280.6) * mm});
            skLineSegment(sketch, "E1940", {"start": v(-149.69, 280.6) * mm, "end": v(-149.5, 280.98) * mm});
            skLineSegment(sketch, "E1941", {"start": v(-149.5, 280.98) * mm, "end": v(-149.3, 281.34) * mm});
            skLineSegment(sketch, "E1942", {"start": v(-149.3, 281.34) * mm, "end": v(-149.1, 281.7) * mm});
            skLineSegment(sketch, "E1943", {"start": v(-149.1, 281.7) * mm, "end": v(-148.89, 282.06) * mm});
            skLineSegment(sketch, "E1944", {"start": v(-148.89, 282.06) * mm, "end": v(-148.67, 282.4) * mm});
            skLineSegment(sketch, "E1945", {"start": v(-148.67, 282.4) * mm, "end": v(-148.43, 282.75) * mm});
            skLineSegment(sketch, "E1946", {"start": v(-148.43, 282.75) * mm, "end": v(-148.2, 283.1) * mm});
            skLineSegment(sketch, "E1947", {"start": v(-148.2, 283.1) * mm, "end": v(-147.95, 283.43) * mm});
            skLineSegment(sketch, "E1948", {"start": v(-147.95, 283.43) * mm, "end": v(-147.69, 283.75) * mm});
            skLineSegment(sketch, "E1949", {"start": v(-147.69, 283.75) * mm, "end": v(-147.42, 284.08) * mm});
            skLineSegment(sketch, "E1950", {"start": v(-147.42, 284.08) * mm, "end": v(-147.15, 284.4) * mm});
            skLineSegment(sketch, "E1951", {"start": v(-147.15, 284.4) * mm, "end": v(-146.87, 284.7) * mm});
            skLineSegment(sketch, "E1952", {"start": v(-146.87, 284.7) * mm, "end": v(-146.57, 285) * mm});
            skLineSegment(sketch, "E1953", {"start": v(-146.57, 285) * mm, "end": v(-146.2, 285.35) * mm});
            skLineSegment(sketch, "E1954", {"start": v(-146.2, 285.35) * mm, "end": v(-145.8, 285.7) * mm});
            skLineSegment(sketch, "E1955", {"start": v(-145.8, 285.7) * mm, "end": v(-145.4, 286.02) * mm});
            skLineSegment(sketch, "E1956", {"start": v(-145.4, 286.02) * mm, "end": v(-145, 286.34) * mm});
            skLineSegment(sketch, "E1957", {"start": v(-145, 286.34) * mm, "end": v(-144.6, 286.65) * mm});
            skLineSegment(sketch, "E1958", {"start": v(-144.6, 286.65) * mm, "end": v(-144.18, 286.95) * mm});
            skLineSegment(sketch, "E1959", {"start": v(-144.18, 286.95) * mm, "end": v(-143.75, 287.23) * mm});
            skLineSegment(sketch, "E1960", {"start": v(-143.75, 287.23) * mm, "end": v(-143.32, 287.5) * mm});
            skLineSegment(sketch, "E1961", {"start": v(-143.32, 287.5) * mm, "end": v(-142.89, 287.77) * mm});
            skLineSegment(sketch, "E1962", {"start": v(-142.89, 287.77) * mm, "end": v(-142.44, 288.03) * mm});
            skLineSegment(sketch, "E1963", {"start": v(-142.44, 288.03) * mm, "end": v(-142, 288.27) * mm});
            skLineSegment(sketch, "E1964", {"start": v(-142, 288.27) * mm, "end": v(-141.54, 288.5) * mm});
            skLineSegment(sketch, "E1965", {"start": v(-141.54, 288.5) * mm, "end": v(-141.08, 288.72) * mm});
            skLineSegment(sketch, "E1966", {"start": v(-141.08, 288.72) * mm, "end": v(-140.62, 288.93) * mm});
            skLineSegment(sketch, "E1967", {"start": v(-140.62, 288.93) * mm, "end": v(-140.15, 289.13) * mm});
            skLineSegment(sketch, "E1968", {"start": v(-140.15, 289.13) * mm, "end": v(-139.67, 289.31) * mm});
            skLineSegment(sketch, "E1969", {"start": v(-139.67, 289.31) * mm, "end": v(-139.2, 289.48) * mm});
            skLineSegment(sketch, "E1970", {"start": v(-139.2, 289.48) * mm, "end": v(-138.71, 289.65) * mm});
            skLineSegment(sketch, "E1971", {"start": v(-138.71, 289.65) * mm, "end": v(-138.22, 289.8) * mm});
            skLineSegment(sketch, "E1972", {"start": v(-138.22, 289.8) * mm, "end": v(-137.73, 289.93) * mm});
            skLineSegment(sketch, "E1973", {"start": v(-137.73, 289.93) * mm, "end": v(-137.24, 290.06) * mm});
            skLineSegment(sketch, "E1974", {"start": v(-137.24, 290.06) * mm, "end": v(-136.74, 290.18) * mm});
            skLineSegment(sketch, "E1975", {"start": v(-136.74, 290.18) * mm, "end": v(-136.24, 290.28) * mm});
            skLineSegment(sketch, "E1976", {"start": v(-136.24, 290.28) * mm, "end": v(-135.74, 290.37) * mm});
            skLineSegment(sketch, "E1977", {"start": v(-135.74, 290.37) * mm, "end": v(-135.23, 290.44) * mm});
            skLineSegment(sketch, "E1978", {"start": v(-135.23, 290.44) * mm, "end": v(-134.73, 290.5) * mm});
            skLineSegment(sketch, "E1979", {"start": v(-134.73, 290.5) * mm, "end": v(-134.22, 290.56) * mm});
            skLineSegment(sketch, "E1980", {"start": v(-134.22, 290.56) * mm, "end": v(-133.7, 290.6) * mm});
            skLineSegment(sketch, "E1981", {"start": v(-133.7, 290.6) * mm, "end": v(-133.2, 290.63) * mm});
            skLineSegment(sketch, "E1982", {"start": v(-133.2, 290.63) * mm, "end": v(-132.68, 290.64) * mm});
            skLineSegment(sketch, "E1983", {"start": v(-132.68, 290.64) * mm, "end": v(-132.16, 290.64) * mm});
            skLineSegment(sketch, "E1984", {"start": v(-132.16, 290.64) * mm, "end": v(-131.64, 290.63) * mm});
            skLineSegment(sketch, "E1985", {"start": v(-131.64, 290.63) * mm, "end": v(-131.08, 290.65) * mm});
            skLineSegment(sketch, "E1986", {"start": v(-131.08, 290.65) * mm, "end": v(-130.52, 290.65) * mm});
            skLineSegment(sketch, "E1987", {"start": v(-130.52, 290.65) * mm, "end": v(-129.96, 290.64) * mm});
            skLineSegment(sketch, "E1988", {"start": v(-129.96, 290.64) * mm, "end": v(-129.4, 290.6) * mm});
            skLineSegment(sketch, "E1989", {"start": v(-129.4, 290.6) * mm, "end": v(-128.85, 290.57) * mm});
            skLineSegment(sketch, "E1990", {"start": v(-128.85, 290.57) * mm, "end": v(-128.3, 290.51) * mm});
            skLineSegment(sketch, "E1991", {"start": v(-128.3, 290.51) * mm, "end": v(-127.74, 290.45) * mm});
            skLineSegment(sketch, "E1992", {"start": v(-127.74, 290.45) * mm, "end": v(-127.2, 290.36) * mm});
            skLineSegment(sketch, "E1993", {"start": v(-127.2, 290.36) * mm, "end": v(-126.65, 290.27) * mm});
            skLineSegment(sketch, "E1994", {"start": v(-126.65, 290.27) * mm, "end": v(-126.1, 290.16) * mm});
            skLineSegment(sketch, "E1995", {"start": v(-126.1, 290.16) * mm, "end": v(-125.56, 290.04) * mm});
            skLineSegment(sketch, "E1996", {"start": v(-125.56, 290.04) * mm, "end": v(-125.03, 289.9) * mm});
            skLineSegment(sketch, "E1997", {"start": v(-125.03, 289.9) * mm, "end": v(-124.5, 289.75) * mm});
            skLineSegment(sketch, "E1998", {"start": v(-124.5, 289.75) * mm, "end": v(-123.97, 289.59) * mm});
            skLineSegment(sketch, "E1999", {"start": v(-123.97, 289.59) * mm, "end": v(-123.44, 289.41) * mm});
            skLineSegment(sketch, "E2000", {"start": v(-123.44, 289.41) * mm, "end": v(-122.92, 289.23) * mm});
            skLineSegment(sketch, "E2001", {"start": v(-122.92, 289.23) * mm, "end": v(-122.4, 289.03) * mm});
            skLineSegment(sketch, "E2002", {"start": v(-122.4, 289.03) * mm, "end": v(-121.9, 288.81) * mm});
            skLineSegment(sketch, "E2003", {"start": v(-121.9, 288.81) * mm, "end": v(-121.4, 288.59) * mm});
            skLineSegment(sketch, "E2004", {"start": v(-121.4, 288.59) * mm, "end": v(-120.9, 288.35) * mm});
            skLineSegment(sketch, "E2005", {"start": v(-120.9, 288.35) * mm, "end": v(-120.4, 288.1) * mm});
            skLineSegment(sketch, "E2006", {"start": v(-120.4, 288.1) * mm, "end": v(-119.91, 287.83) * mm});
            skLineSegment(sketch, "E2007", {"start": v(-119.91, 287.83) * mm, "end": v(-119.43, 287.56) * mm});
            skLineSegment(sketch, "E2008", {"start": v(-119.43, 287.56) * mm, "end": v(-118.96, 287.27) * mm});
            skLineSegment(sketch, "E2009", {"start": v(-118.96, 287.27) * mm, "end": v(-118.5, 286.97) * mm});
            skLineSegment(sketch, "E2010", {"start": v(-118.5, 286.97) * mm, "end": v(-118.03, 286.66) * mm});
            skLineSegment(sketch, "E2011", {"start": v(-118.03, 286.66) * mm, "end": v(-117.58, 286.33) * mm});
            skLineSegment(sketch, "E2012", {"start": v(-117.58, 286.33) * mm, "end": v(-117.13, 286) * mm});
            skLineSegment(sketch, "E2013", {"start": v(-117.13, 286) * mm, "end": v(-116.7, 285.65) * mm});
            skLineSegment(sketch, "E2014", {"start": v(-116.7, 285.65) * mm, "end": v(-116.27, 285.3) * mm});
            skLineSegment(sketch, "E2015", {"start": v(-116.27, 285.3) * mm, "end": v(-115.85, 284.92) * mm});
            skLineSegment(sketch, "E2016", {"start": v(-115.85, 284.92) * mm, "end": v(-115.44, 284.54) * mm});
            skLineSegment(sketch, "E2017", {"start": v(-115.44, 284.54) * mm, "end": v(-115.14, 284.25) * mm});
            skLineSegment(sketch, "E2018", {"start": v(-115.14, 284.25) * mm, "end": v(-114.86, 283.96) * mm});
            skLineSegment(sketch, "E2019", {"start": v(-114.86, 283.96) * mm, "end": v(-114.59, 283.66) * mm});
            skLineSegment(sketch, "E2020", {"start": v(-114.59, 283.66) * mm, "end": v(-114.32, 283.36) * mm});
            skLineSegment(sketch, "E2021", {"start": v(-114.32, 283.36) * mm, "end": v(-114.06, 283.04) * mm});
            skLineSegment(sketch, "E2022", {"start": v(-114.06, 283.04) * mm, "end": v(-113.82, 282.73) * mm});
            skLineSegment(sketch, "E2023", {"start": v(-113.82, 282.73) * mm, "end": v(-113.58, 282.4) * mm});
            skLineSegment(sketch, "E2024", {"start": v(-113.58, 282.4) * mm, "end": v(-113.34, 282.07) * mm});
            skLineSegment(sketch, "E2025", {"start": v(-113.34, 282.07) * mm, "end": v(-113.12, 281.74) * mm});
            skLineSegment(sketch, "E2026", {"start": v(-113.12, 281.74) * mm, "end": v(-112.9, 281.4) * mm});
            skLineSegment(sketch, "E2027", {"start": v(-112.9, 281.4) * mm, "end": v(-112.7, 281.05) * mm});
            skLineSegment(sketch, "E2028", {"start": v(-112.7, 281.05) * mm, "end": v(-112.5, 280.7) * mm});
            skLineSegment(sketch, "E2029", {"start": v(-112.5, 280.7) * mm, "end": v(-112.32, 280.34) * mm});
            skLineSegment(sketch, "E2030", {"start": v(-112.32, 280.34) * mm, "end": v(-112.14, 279.99) * mm});
            skLineSegment(sketch, "E2031", {"start": v(-112.14, 279.99) * mm, "end": v(-111.97, 279.62) * mm});
            skLineSegment(sketch, "E2032", {"start": v(-111.97, 279.62) * mm, "end": v(-111.81, 279.25) * mm});
            skLineSegment(sketch, "E2033", {"start": v(-111.81, 279.25) * mm, "end": v(-111.67, 278.88) * mm});
            skLineSegment(sketch, "E2034", {"start": v(-111.67, 278.88) * mm, "end": v(-111.53, 278.5) * mm});
            skLineSegment(sketch, "E2035", {"start": v(-111.53, 278.5) * mm, "end": v(-111.4, 278.13) * mm});
            skLineSegment(sketch, "E2036", {"start": v(-111.4, 278.13) * mm, "end": v(-111.27, 277.74) * mm});
            skLineSegment(sketch, "E2037", {"start": v(-111.27, 277.74) * mm, "end": v(-111.16, 277.36) * mm});
            skLineSegment(sketch, "E2038", {"start": v(-111.16, 277.36) * mm, "end": v(-111.06, 276.97) * mm});
            skLineSegment(sketch, "E2039", {"start": v(-111.06, 276.97) * mm, "end": v(-110.97, 276.58) * mm});
            skLineSegment(sketch, "E2040", {"start": v(-110.97, 276.58) * mm, "end": v(-110.89, 276.18) * mm});
            skLineSegment(sketch, "E2041", {"start": v(-110.89, 276.18) * mm, "end": v(-110.82, 275.79) * mm});
            skLineSegment(sketch, "E2042", {"start": v(-110.82, 275.79) * mm, "end": v(-110.76, 275.39) * mm});
            skLineSegment(sketch, "E2043", {"start": v(-110.76, 275.39) * mm, "end": v(-110.7, 274.99) * mm});
            skLineSegment(sketch, "E2044", {"start": v(-110.7, 274.99) * mm, "end": v(-110.67, 274.58) * mm});
            skLineSegment(sketch, "E2045", {"start": v(-110.67, 274.58) * mm, "end": v(-110.64, 274.18) * mm});
            skLineSegment(sketch, "E2046", {"start": v(-110.64, 274.18) * mm, "end": v(-110.62, 273.77) * mm});
            skLineSegment(sketch, "E2047", {"start": v(-110.62, 273.77) * mm, "end": v(-110.6, 273.37) * mm});
            skLineSegment(sketch, "E2048", {"start": v(-110.6, 273.37) * mm, "end": v(-110.6, 272.96) * mm});
            skLineSegment(sketch, "E2049", {"start": v(-110.6, 272.96) * mm, "end": v(-110.61, 272.55) * mm});
            skLineSegment(sketch, "E2050", {"start": v(-110.61, 272.55) * mm, "end": v(-110.63, 272.13) * mm});
            skLineSegment(sketch, "E2051", {"start": v(-110.63, 272.13) * mm, "end": v(-110.65, 271.72) * mm});
            skLineSegment(sketch, "E2052", {"start": v(-110.65, 271.72) * mm, "end": v(-110.69, 271.31) * mm});
            skLineSegment(sketch, "E2053", {"start": v(-110.69, 271.31) * mm, "end": v(-110.73, 270.9) * mm});
            skLineSegment(sketch, "E2054", {"start": v(-110.73, 270.9) * mm, "end": v(-110.8, 270.5) * mm});
            skLineSegment(sketch, "E2055", {"start": v(-110.8, 270.5) * mm, "end": v(-110.86, 270.1) * mm});
            skLineSegment(sketch, "E2056", {"start": v(-110.86, 270.1) * mm, "end": v(-110.94, 269.69) * mm});
            skLineSegment(sketch, "E2057", {"start": v(-110.94, 269.69) * mm, "end": v(-111.02, 269.29) * mm});
            skLineSegment(sketch, "E2058", {"start": v(-111.02, 269.29) * mm, "end": v(-111.12, 268.9) * mm});
            skLineSegment(sketch, "E2059", {"start": v(-111.12, 268.9) * mm, "end": v(-111.23, 268.5) * mm});
            skLineSegment(sketch, "E2060", {"start": v(-111.23, 268.5) * mm, "end": v(-111.35, 268.1) * mm});
            skLineSegment(sketch, "E2061", {"start": v(-111.35, 268.1) * mm, "end": v(-111.47, 267.72) * mm});
            skLineSegment(sketch, "E2062", {"start": v(-111.47, 267.72) * mm, "end": v(-111.61, 267.34) * mm});
            skLineSegment(sketch, "E2063", {"start": v(-111.61, 267.34) * mm, "end": v(-111.76, 266.96) * mm});
            skLineSegment(sketch, "E2064", {"start": v(-111.76, 266.96) * mm, "end": v(-111.91, 266.58) * mm});
            skLineSegment(sketch, "E2065", {"start": v(-111.91, 266.58) * mm, "end": v(-112.08, 266.2) * mm});
            skLineSegment(sketch, "E2066", {"start": v(-112.08, 266.2) * mm, "end": v(-112.26, 265.84) * mm});
            skLineSegment(sketch, "E2067", {"start": v(-112.26, 265.84) * mm, "end": v(-112.44, 265.48) * mm});
            skLineSegment(sketch, "E2068", {"start": v(-112.44, 265.48) * mm, "end": v(-112.64, 265.12) * mm});
            skLineSegment(sketch, "E2069", {"start": v(-112.64, 265.12) * mm, "end": v(-112.84, 264.76) * mm});
            skLineSegment(sketch, "E2070", {"start": v(-112.84, 264.76) * mm, "end": v(-113.05, 264.41) * mm});
            skLineSegment(sketch, "E2071", {"start": v(-113.05, 264.41) * mm, "end": v(-113.27, 264.07) * mm});
            skLineSegment(sketch, "E2072", {"start": v(-113.27, 264.07) * mm, "end": v(-113.5, 263.73) * mm});
            skLineSegment(sketch, "E2073", {"start": v(-113.5, 263.73) * mm, "end": v(-113.74, 263.4) * mm});
            skLineSegment(sketch, "E2074", {"start": v(-113.74, 263.4) * mm, "end": v(-114, 263.07) * mm});
            skLineSegment(sketch, "E2075", {"start": v(-114, 263.07) * mm, "end": v(-114.25, 262.75) * mm});
            skLineSegment(sketch, "E2076", {"start": v(-114.25, 262.75) * mm, "end": v(-114.51, 262.44) * mm});
            skLineSegment(sketch, "E2077", {"start": v(-114.51, 262.44) * mm, "end": v(-114.79, 262.13) * mm});
            skLineSegment(sketch, "E2078", {"start": v(-114.79, 262.13) * mm, "end": v(-115.07, 261.83) * mm});
            skLineSegment(sketch, "E2079", {"start": v(-115.07, 261.83) * mm, "end": v(-115.36, 261.54) * mm});
            skLineSegment(sketch, "E2080", {"start": v(-115.36, 261.54) * mm, "end": v(-115.66, 261.25) * mm});
            skLineSegment(sketch, "E2081", {"start": v(-115.66, 261.25) * mm, "end": v(-116.07, 260.88) * mm});
            skLineSegment(sketch, "E2082", {"start": v(-116.07, 260.88) * mm, "end": v(-116.49, 260.52) * mm});
            skLineSegment(sketch, "E2083", {"start": v(-116.49, 260.52) * mm, "end": v(-116.91, 260.17) * mm});
            skLineSegment(sketch, "E2084", {"start": v(-116.91, 260.17) * mm, "end": v(-117.35, 259.84) * mm});
            skLineSegment(sketch, "E2085", {"start": v(-117.35, 259.84) * mm, "end": v(-117.79, 259.51) * mm});
            skLineSegment(sketch, "E2086", {"start": v(-117.79, 259.51) * mm, "end": v(-118.24, 259.2) * mm});
            skLineSegment(sketch, "E2087", {"start": v(-118.24, 259.2) * mm, "end": v(-118.7, 258.9) * mm});
            skLineSegment(sketch, "E2088", {"start": v(-118.7, 258.9) * mm, "end": v(-119.16, 258.6) * mm});
            skLineSegment(sketch, "E2089", {"start": v(-119.16, 258.6) * mm, "end": v(-119.63, 258.33) * mm});
            skLineSegment(sketch, "E2090", {"start": v(-119.63, 258.33) * mm, "end": v(-120.1, 258.06) * mm});
            skLineSegment(sketch, "E2091", {"start": v(-120.1, 258.06) * mm, "end": v(-120.58, 257.81) * mm});
            skLineSegment(sketch, "E2092", {"start": v(-120.58, 257.81) * mm, "end": v(-121.07, 257.57) * mm});
            skLineSegment(sketch, "E2093", {"start": v(-121.07, 257.57) * mm, "end": v(-121.56, 257.34) * mm});
            skLineSegment(sketch, "E2094", {"start": v(-121.56, 257.34) * mm, "end": v(-122.06, 257.12) * mm});
            skLineSegment(sketch, "E2095", {"start": v(-122.06, 257.12) * mm, "end": v(-122.57, 256.92) * mm});
            skLineSegment(sketch, "E2096", {"start": v(-122.57, 256.92) * mm, "end": v(-123.08, 256.72) * mm});
            skLineSegment(sketch, "E2097", {"start": v(-123.08, 256.72) * mm, "end": v(-123.59, 256.54) * mm});
            skLineSegment(sketch, "E2098", {"start": v(-123.59, 256.54) * mm, "end": v(-124.1, 256.38) * mm});
            skLineSegment(sketch, "E2099", {"start": v(-124.1, 256.38) * mm, "end": v(-124.63, 256.22) * mm});
            skLineSegment(sketch, "E2100", {"start": v(-124.63, 256.22) * mm, "end": v(-125.15, 256.08) * mm});
            skLineSegment(sketch, "E2101", {"start": v(-125.15, 256.08) * mm, "end": v(-125.68, 255.95) * mm});
            skLineSegment(sketch, "E2102", {"start": v(-125.68, 255.95) * mm, "end": v(-126.22, 255.84) * mm});
            skLineSegment(sketch, "E2103", {"start": v(-126.22, 255.84) * mm, "end": v(-126.75, 255.73) * mm});
            skLineSegment(sketch, "E2104", {"start": v(-126.75, 255.73) * mm, "end": v(-127.29, 255.64) * mm});
            skLineSegment(sketch, "E2105", {"start": v(-127.29, 255.64) * mm, "end": v(-127.83, 255.57) * mm});
            skLineSegment(sketch, "E2106", {"start": v(-127.83, 255.57) * mm, "end": v(-128.37, 255.5) * mm});
            skLineSegment(sketch, "E2107", {"start": v(-128.37, 255.5) * mm, "end": v(-128.92, 255.46) * mm});
            skLineSegment(sketch, "E2108", {"start": v(-128.92, 255.46) * mm, "end": v(-129.47, 255.42) * mm});
            skLineSegment(sketch, "E2109", {"start": v(-129.47, 255.42) * mm, "end": v(-130.01, 255.4) * mm});
            skLineSegment(sketch, "E2110", {"start": v(-130.01, 255.4) * mm, "end": v(-130.56, 255.4) * mm});
            skLineSegment(sketch, "E2111", {"start": v(-130.56, 255.4) * mm, "end": v(-131.12, 255.4) * mm});
            skLineSegment(sketch, "E2112", {"start": v(-131.12, 255.4) * mm, "end": v(-131.67, 255.42) * mm});
            skLineSegment(sketch, "E2113", {"start": v(-131.67, 255.42) * mm, "end": v(-132.18, 255.4) * mm});
            skLineSegment(sketch, "E2114", {"start": v(-132.18, 255.4) * mm, "end": v(-132.7, 255.41) * mm});
            skLineSegment(sketch, "E2115", {"start": v(-132.7, 255.41) * mm, "end": v(-133.2, 255.43) * mm});
            skLineSegment(sketch, "E2116", {"start": v(-133.2, 255.43) * mm, "end": v(-133.72, 255.46) * mm});
            skLineSegment(sketch, "E2117", {"start": v(-133.72, 255.46) * mm, "end": v(-134.23, 255.5) * mm});
            skLineSegment(sketch, "E2118", {"start": v(-134.23, 255.5) * mm, "end": v(-134.74, 255.56) * mm});
            skLineSegment(sketch, "E2119", {"start": v(-134.74, 255.56) * mm, "end": v(-135.24, 255.63) * mm});
            skLineSegment(sketch, "E2120", {"start": v(-135.24, 255.63) * mm, "end": v(-135.74, 255.71) * mm});
            skLineSegment(sketch, "E2121", {"start": v(-135.74, 255.71) * mm, "end": v(-136.24, 255.8) * mm});
            skLineSegment(sketch, "E2122", {"start": v(-136.24, 255.8) * mm, "end": v(-136.74, 255.9) * mm});
            skLineSegment(sketch, "E2123", {"start": v(-136.74, 255.9) * mm, "end": v(-137.24, 256.03) * mm});
            skLineSegment(sketch, "E2124", {"start": v(-137.24, 256.03) * mm, "end": v(-137.73, 256.16) * mm});
            skLineSegment(sketch, "E2125", {"start": v(-137.73, 256.16) * mm, "end": v(-138.21, 256.3) * mm});
            skLineSegment(sketch, "E2126", {"start": v(-138.21, 256.3) * mm, "end": v(-138.7, 256.46) * mm});
            skLineSegment(sketch, "E2127", {"start": v(-138.7, 256.46) * mm, "end": v(-139.18, 256.62) * mm});
            skLineSegment(sketch, "E2128", {"start": v(-139.18, 256.62) * mm, "end": v(-139.65, 256.8) * mm});
            skLineSegment(sketch, "E2129", {"start": v(-139.65, 256.8) * mm, "end": v(-140.12, 256.99) * mm});
            skLineSegment(sketch, "E2130", {"start": v(-140.12, 256.99) * mm, "end": v(-140.59, 257.2) * mm});
            skLineSegment(sketch, "E2131", {"start": v(-140.59, 257.2) * mm, "end": v(-141.05, 257.4) * mm});
            skLineSegment(sketch, "E2132", {"start": v(-141.05, 257.4) * mm, "end": v(-141.5, 257.63) * mm});
            skLineSegment(sketch, "E2133", {"start": v(-141.5, 257.63) * mm, "end": v(-141.95, 257.86) * mm});
            skLineSegment(sketch, "E2134", {"start": v(-141.95, 257.86) * mm, "end": v(-142.4, 258.11) * mm});
            skLineSegment(sketch, "E2135", {"start": v(-142.4, 258.11) * mm, "end": v(-142.84, 258.37) * mm});
            skLineSegment(sketch, "E2136", {"start": v(-142.84, 258.37) * mm, "end": v(-143.27, 258.64) * mm});
            skLineSegment(sketch, "E2137", {"start": v(-143.27, 258.64) * mm, "end": v(-143.7, 258.92) * mm});
            skLineSegment(sketch, "E2138", {"start": v(-143.7, 258.92) * mm, "end": v(-144.11, 259.2) * mm});
            skLineSegment(sketch, "E2139", {"start": v(-144.11, 259.2) * mm, "end": v(-144.52, 259.51) * mm});
            skLineSegment(sketch, "E2140", {"start": v(-144.52, 259.51) * mm, "end": v(-144.93, 259.82) * mm});
            skLineSegment(sketch, "E2141", {"start": v(-144.93, 259.82) * mm, "end": v(-145.32, 260.15) * mm});
            skLineSegment(sketch, "E2142", {"start": v(-145.32, 260.15) * mm, "end": v(-145.71, 260.48) * mm});
            skLineSegment(sketch, "E2143", {"start": v(-145.71, 260.48) * mm, "end": v(-146.1, 260.82) * mm});
            skLineSegment(sketch, "E2144", {"start": v(-146.1, 260.82) * mm, "end": v(-146.47, 261.18) * mm});
            skLineSegment(sketch, "E2145", {"start": v(-146.47, 261.18) * mm, "end": v(-146.76, 261.47) * mm});
            skLineSegment(sketch, "E2146", {"start": v(-146.76, 261.47) * mm, "end": v(-147.04, 261.77) * mm});
            skLineSegment(sketch, "E2147", {"start": v(-147.04, 261.77) * mm, "end": v(-147.32, 262.08) * mm});
            skLineSegment(sketch, "E2148", {"start": v(-147.32, 262.08) * mm, "end": v(-147.59, 262.4) * mm});
            skLineSegment(sketch, "E2149", {"start": v(-147.59, 262.4) * mm, "end": v(-147.84, 262.71) * mm});
            skLineSegment(sketch, "E2150", {"start": v(-147.84, 262.71) * mm, "end": v(-148.1, 263.04) * mm});
            skLineSegment(sketch, "E2151", {"start": v(-148.1, 263.04) * mm, "end": v(-148.34, 263.37) * mm});
            skLineSegment(sketch, "E2152", {"start": v(-148.34, 263.37) * mm, "end": v(-148.57, 263.7) * mm});
            skLineSegment(sketch, "E2153", {"start": v(-148.57, 263.7) * mm, "end": v(-148.8, 264.05) * mm});
            skLineSegment(sketch, "E2154", {"start": v(-148.8, 264.05) * mm, "end": v(-149, 264.4) * mm});
            skLineSegment(sketch, "E2155", {"start": v(-149, 264.4) * mm, "end": v(-149.21, 264.75) * mm});
            skLineSegment(sketch, "E2156", {"start": v(-149.21, 264.75) * mm, "end": v(-149.41, 265.1) * mm});
            skLineSegment(sketch, "E2157", {"start": v(-149.41, 265.1) * mm, "end": v(-149.6, 265.47) * mm});
            skLineSegment(sketch, "E2158", {"start": v(-149.6, 265.47) * mm, "end": v(-149.78, 265.83) * mm});
            skLineSegment(sketch, "E2159", {"start": v(-149.78, 265.83) * mm, "end": v(-149.95, 266.2) * mm});
            skLineSegment(sketch, "E2160", {"start": v(-149.95, 266.2) * mm, "end": v(-150.11, 266.58) * mm});
            skLineSegment(sketch, "E2161", {"start": v(-150.11, 266.58) * mm, "end": v(-150.26, 266.96) * mm});
            skLineSegment(sketch, "E2162", {"start": v(-150.26, 266.96) * mm, "end": v(-150.4, 267.34) * mm});
            skLineSegment(sketch, "E2163", {"start": v(-150.4, 267.34) * mm, "end": v(-150.54, 267.72) * mm});
            skLineSegment(sketch, "E2164", {"start": v(-150.54, 267.72) * mm, "end": v(-150.66, 268.11) * mm});
            skLineSegment(sketch, "E2165", {"start": v(-150.66, 268.11) * mm, "end": v(-150.77, 268.5) * mm});
            skLineSegment(sketch, "E2166", {"start": v(-150.77, 268.5) * mm, "end": v(-150.88, 268.9) * mm});
            skLineSegment(sketch, "E2167", {"start": v(-150.88, 268.9) * mm, "end": v(-150.97, 269.3) * mm});
            skLineSegment(sketch, "E2168", {"start": v(-150.97, 269.3) * mm, "end": v(-151.06, 269.7) * mm});
            skLineSegment(sketch, "E2169", {"start": v(-151.06, 269.7) * mm, "end": v(-151.13, 270.1) * mm});
            skLineSegment(sketch, "E2170", {"start": v(-151.13, 270.1) * mm, "end": v(-151.2, 270.5) * mm});
            skLineSegment(sketch, "E2171", {"start": v(-151.2, 270.5) * mm, "end": v(-151.25, 270.91) * mm});
            skLineSegment(sketch, "E2172", {"start": v(-151.25, 270.91) * mm, "end": v(-151.3, 271.32) * mm});
            skLineSegment(sketch, "E2173", {"start": v(-151.3, 271.32) * mm, "end": v(-151.33, 271.73) * mm});
            skLineSegment(sketch, "E2174", {"start": v(-151.33, 271.73) * mm, "end": v(-151.35, 272.14) * mm});
            skLineSegment(sketch, "E2175", {"start": v(-151.35, 272.14) * mm, "end": v(-151.37, 272.55) * mm});
            skLineSegment(sketch, "E2176", {"start": v(-151.37, 272.55) * mm, "end": v(-151.37, 272.97) * mm});
            skLineSegment(sketch, "E2177", {"start": v(-151.37, 228.72) * mm, "end": v(-151.37, 229.14) * mm});
            skLineSegment(sketch, "E2178", {"start": v(-151.37, 229.14) * mm, "end": v(-151.36, 229.56) * mm});
            skLineSegment(sketch, "E2179", {"start": v(-151.36, 229.56) * mm, "end": v(-151.35, 229.98) * mm});
            skLineSegment(sketch, "E2180", {"start": v(-151.35, 229.98) * mm, "end": v(-151.32, 230.4) * mm});
            skLineSegment(sketch, "E2181", {"start": v(-151.32, 230.4) * mm, "end": v(-151.28, 230.81) * mm});
            skLineSegment(sketch, "E2182", {"start": v(-151.28, 230.81) * mm, "end": v(-151.23, 231.23) * mm});
            skLineSegment(sketch, "E2183", {"start": v(-151.23, 231.23) * mm, "end": v(-151.17, 231.64) * mm});
            skLineSegment(sketch, "E2184", {"start": v(-151.17, 231.64) * mm, "end": v(-151.1, 232.05) * mm});
            skLineSegment(sketch, "E2185", {"start": v(-151.1, 232.05) * mm, "end": v(-151.02, 232.45) * mm});
            skLineSegment(sketch, "E2186", {"start": v(-151.02, 232.45) * mm, "end": v(-150.93, 232.86) * mm});
            skLineSegment(sketch, "E2187", {"start": v(-150.93, 232.86) * mm, "end": v(-150.83, 233.26) * mm});
            skLineSegment(sketch, "E2188", {"start": v(-150.83, 233.26) * mm, "end": v(-150.72, 233.66) * mm});
            skLineSegment(sketch, "E2189", {"start": v(-150.72, 233.66) * mm, "end": v(-150.6, 234.06) * mm});
            skLineSegment(sketch, "E2190", {"start": v(-150.6, 234.06) * mm, "end": v(-150.48, 234.45) * mm});
            skLineSegment(sketch, "E2191", {"start": v(-150.48, 234.45) * mm, "end": v(-150.34, 234.84) * mm});
            skLineSegment(sketch, "E2192", {"start": v(-150.34, 234.84) * mm, "end": v(-150.19, 235.23) * mm});
            skLineSegment(sketch, "E2193", {"start": v(-150.19, 235.23) * mm, "end": v(-150.03, 235.6) * mm});
            skLineSegment(sketch, "E2194", {"start": v(-150.03, 235.6) * mm, "end": v(-149.86, 235.99) * mm});
            skLineSegment(sketch, "E2195", {"start": v(-149.86, 235.99) * mm, "end": v(-149.69, 236.36) * mm});
            skLineSegment(sketch, "E2196", {"start": v(-149.69, 236.36) * mm, "end": v(-149.5, 236.73) * mm});
            skLineSegment(sketch, "E2197", {"start": v(-149.5, 236.73) * mm, "end": v(-149.3, 237.1) * mm});
            skLineSegment(sketch, "E2198", {"start": v(-149.3, 237.1) * mm, "end": v(-149.1, 237.46) * mm});
            skLineSegment(sketch, "E2199", {"start": v(-149.1, 237.46) * mm, "end": v(-148.89, 237.81) * mm});
            skLineSegment(sketch, "E2200", {"start": v(-148.89, 237.81) * mm, "end": v(-148.67, 238.16) * mm});
            skLineSegment(sketch, "E2201", {"start": v(-148.67, 238.16) * mm, "end": v(-148.43, 238.5) * mm});
            skLineSegment(sketch, "E2202", {"start": v(-148.43, 238.5) * mm, "end": v(-148.2, 238.85) * mm});
            skLineSegment(sketch, "E2203", {"start": v(-148.2, 238.85) * mm, "end": v(-147.95, 239.18) * mm});
            skLineSegment(sketch, "E2204", {"start": v(-147.95, 239.18) * mm, "end": v(-147.69, 239.5) * mm});
            skLineSegment(sketch, "E2205", {"start": v(-147.69, 239.5) * mm, "end": v(-147.42, 239.83) * mm});
            skLineSegment(sketch, "E2206", {"start": v(-147.42, 239.83) * mm, "end": v(-147.15, 240.15) * mm});
            skLineSegment(sketch, "E2207", {"start": v(-147.15, 240.15) * mm, "end": v(-146.87, 240.46) * mm});
            skLineSegment(sketch, "E2208", {"start": v(-146.87, 240.46) * mm, "end": v(-146.57, 240.76) * mm});
            skLineSegment(sketch, "E2209", {"start": v(-146.57, 240.76) * mm, "end": v(-146.2, 241.1) * mm});
            skLineSegment(sketch, "E2210", {"start": v(-146.2, 241.1) * mm, "end": v(-145.8, 241.45) * mm});
            skLineSegment(sketch, "E2211", {"start": v(-145.8, 241.45) * mm, "end": v(-145.4, 241.78) * mm});
            skLineSegment(sketch, "E2212", {"start": v(-145.4, 241.78) * mm, "end": v(-145, 242.1) * mm});
            skLineSegment(sketch, "E2213", {"start": v(-145, 242.1) * mm, "end": v(-144.6, 242.4) * mm});
            skLineSegment(sketch, "E2214", {"start": v(-144.6, 242.4) * mm, "end": v(-144.18, 242.7) * mm});
            skLineSegment(sketch, "E2215", {"start": v(-144.18, 242.7) * mm, "end": v(-143.75, 242.99) * mm});
            skLineSegment(sketch, "E2216", {"start": v(-143.75, 242.99) * mm, "end": v(-143.32, 243.26) * mm});
            skLineSegment(sketch, "E2217", {"start": v(-143.32, 243.26) * mm, "end": v(-142.89, 243.53) * mm});
            skLineSegment(sketch, "E2218", {"start": v(-142.89, 243.53) * mm, "end": v(-142.44, 243.78) * mm});
            skLineSegment(sketch, "E2219", {"start": v(-142.44, 243.78) * mm, "end": v(-142, 244.02) * mm});
            skLineSegment(sketch, "E2220", {"start": v(-142, 244.02) * mm, "end": v(-141.54, 244.25) * mm});
            skLineSegment(sketch, "E2221", {"start": v(-141.54, 244.25) * mm, "end": v(-141.08, 244.47) * mm});
            skLineSegment(sketch, "E2222", {"start": v(-141.08, 244.47) * mm, "end": v(-140.62, 244.68) * mm});
            skLineSegment(sketch, "E2223", {"start": v(-140.62, 244.68) * mm, "end": v(-140.15, 244.88) * mm});
            skLineSegment(sketch, "E2224", {"start": v(-140.15, 244.88) * mm, "end": v(-139.67, 245.07) * mm});
            skLineSegment(sketch, "E2225", {"start": v(-139.67, 245.07) * mm, "end": v(-139.2, 245.24) * mm});
            skLineSegment(sketch, "E2226", {"start": v(-139.2, 245.24) * mm, "end": v(-138.71, 245.4) * mm});
            skLineSegment(sketch, "E2227", {"start": v(-138.71, 245.4) * mm, "end": v(-138.22, 245.55) * mm});
            skLineSegment(sketch, "E2228", {"start": v(-138.22, 245.55) * mm, "end": v(-137.73, 245.69) * mm});
            skLineSegment(sketch, "E2229", {"start": v(-137.73, 245.69) * mm, "end": v(-137.24, 245.82) * mm});
            skLineSegment(sketch, "E2230", {"start": v(-137.24, 245.82) * mm, "end": v(-136.74, 245.93) * mm});
            skLineSegment(sketch, "E2231", {"start": v(-136.74, 245.93) * mm, "end": v(-136.24, 246.03) * mm});
            skLineSegment(sketch, "E2232", {"start": v(-136.24, 246.03) * mm, "end": v(-135.74, 246.12) * mm});
            skLineSegment(sketch, "E2233", {"start": v(-135.74, 246.12) * mm, "end": v(-135.23, 246.2) * mm});
            skLineSegment(sketch, "E2234", {"start": v(-135.23, 246.2) * mm, "end": v(-134.73, 246.26) * mm});
            skLineSegment(sketch, "E2235", {"start": v(-134.73, 246.26) * mm, "end": v(-134.22, 246.32) * mm});
            skLineSegment(sketch, "E2236", {"start": v(-134.22, 246.32) * mm, "end": v(-133.7, 246.35) * mm});
            skLineSegment(sketch, "E2237", {"start": v(-133.7, 246.35) * mm, "end": v(-133.2, 246.38) * mm});
            skLineSegment(sketch, "E2238", {"start": v(-133.2, 246.38) * mm, "end": v(-132.68, 246.4) * mm});
            skLineSegment(sketch, "E2239", {"start": v(-132.68, 246.4) * mm, "end": v(-132.16, 246.4) * mm});
            skLineSegment(sketch, "E2240", {"start": v(-132.16, 246.4) * mm, "end": v(-131.64, 246.38) * mm});
            skLineSegment(sketch, "E2241", {"start": v(-131.64, 246.38) * mm, "end": v(-131.08, 246.4) * mm});
            skLineSegment(sketch, "E2242", {"start": v(-131.08, 246.4) * mm, "end": v(-130.52, 246.4) * mm});
            skLineSegment(sketch, "E2243", {"start": v(-130.52, 246.4) * mm, "end": v(-129.96, 246.4) * mm});
            skLineSegment(sketch, "E2244", {"start": v(-129.96, 246.4) * mm, "end": v(-129.4, 246.36) * mm});
            skLineSegment(sketch, "E2245", {"start": v(-129.4, 246.36) * mm, "end": v(-128.85, 246.32) * mm});
            skLineSegment(sketch, "E2246", {"start": v(-128.85, 246.32) * mm, "end": v(-128.3, 246.27) * mm});
            skLineSegment(sketch, "E2247", {"start": v(-128.3, 246.27) * mm, "end": v(-127.74, 246.2) * mm});
            skLineSegment(sketch, "E2248", {"start": v(-127.74, 246.2) * mm, "end": v(-127.2, 246.12) * mm});
            skLineSegment(sketch, "E2249", {"start": v(-127.2, 246.12) * mm, "end": v(-126.65, 246.02) * mm});
            skLineSegment(sketch, "E2250", {"start": v(-126.65, 246.02) * mm, "end": v(-126.1, 245.91) * mm});
            skLineSegment(sketch, "E2251", {"start": v(-126.1, 245.91) * mm, "end": v(-125.56, 245.8) * mm});
            skLineSegment(sketch, "E2252", {"start": v(-125.56, 245.8) * mm, "end": v(-125.03, 245.66) * mm});
            skLineSegment(sketch, "E2253", {"start": v(-125.03, 245.66) * mm, "end": v(-124.5, 245.5) * mm});
            skLineSegment(sketch, "E2254", {"start": v(-124.5, 245.5) * mm, "end": v(-123.97, 245.34) * mm});
            skLineSegment(sketch, "E2255", {"start": v(-123.97, 245.34) * mm, "end": v(-123.44, 245.17) * mm});
            skLineSegment(sketch, "E2256", {"start": v(-123.44, 245.17) * mm, "end": v(-122.92, 244.98) * mm});
            skLineSegment(sketch, "E2257", {"start": v(-122.92, 244.98) * mm, "end": v(-122.4, 244.78) * mm});
            skLineSegment(sketch, "E2258", {"start": v(-122.4, 244.78) * mm, "end": v(-121.9, 244.57) * mm});
            skLineSegment(sketch, "E2259", {"start": v(-121.9, 244.57) * mm, "end": v(-121.4, 244.34) * mm});
            skLineSegment(sketch, "E2260", {"start": v(-121.4, 244.34) * mm, "end": v(-120.9, 244.1) * mm});
            skLineSegment(sketch, "E2261", {"start": v(-120.9, 244.1) * mm, "end": v(-120.4, 243.85) * mm});
            skLineSegment(sketch, "E2262", {"start": v(-120.4, 243.85) * mm, "end": v(-119.91, 243.59) * mm});
            skLineSegment(sketch, "E2263", {"start": v(-119.91, 243.59) * mm, "end": v(-119.43, 243.31) * mm});
            skLineSegment(sketch, "E2264", {"start": v(-119.43, 243.31) * mm, "end": v(-118.96, 243.02) * mm});
            skLineSegment(sketch, "E2265", {"start": v(-118.96, 243.02) * mm, "end": v(-118.5, 242.72) * mm});
            skLineSegment(sketch, "E2266", {"start": v(-118.5, 242.72) * mm, "end": v(-118.03, 242.41) * mm});
            skLineSegment(sketch, "E2267", {"start": v(-118.03, 242.41) * mm, "end": v(-117.58, 242.09) * mm});
            skLineSegment(sketch, "E2268", {"start": v(-117.58, 242.09) * mm, "end": v(-117.13, 241.75) * mm});
            skLineSegment(sketch, "E2269", {"start": v(-117.13, 241.75) * mm, "end": v(-116.7, 241.4) * mm});
            skLineSegment(sketch, "E2270", {"start": v(-116.7, 241.4) * mm, "end": v(-116.27, 241.05) * mm});
            skLineSegment(sketch, "E2271", {"start": v(-116.27, 241.05) * mm, "end": v(-115.85, 240.68) * mm});
            skLineSegment(sketch, "E2272", {"start": v(-115.85, 240.68) * mm, "end": v(-115.44, 240.3) * mm});
            skLineSegment(sketch, "E2273", {"start": v(-115.44, 240.3) * mm, "end": v(-115.14, 240) * mm});
            skLineSegment(sketch, "E2274", {"start": v(-115.14, 240) * mm, "end": v(-114.86, 239.72) * mm});
            skLineSegment(sketch, "E2275", {"start": v(-114.86, 239.72) * mm, "end": v(-114.59, 239.42) * mm});
            skLineSegment(sketch, "E2276", {"start": v(-114.59, 239.42) * mm, "end": v(-114.32, 239.11) * mm});
            skLineSegment(sketch, "E2277", {"start": v(-114.32, 239.11) * mm, "end": v(-114.06, 238.8) * mm});
            skLineSegment(sketch, "E2278", {"start": v(-114.06, 238.8) * mm, "end": v(-113.82, 238.48) * mm});
            skLineSegment(sketch, "E2279", {"start": v(-113.82, 238.48) * mm, "end": v(-113.58, 238.16) * mm});
            skLineSegment(sketch, "E2280", {"start": v(-113.58, 238.16) * mm, "end": v(-113.34, 237.83) * mm});
            skLineSegment(sketch, "E2281", {"start": v(-113.34, 237.83) * mm, "end": v(-113.12, 237.5) * mm});
            skLineSegment(sketch, "E2282", {"start": v(-113.12, 237.5) * mm, "end": v(-112.9, 237.15) * mm});
            skLineSegment(sketch, "E2283", {"start": v(-112.9, 237.15) * mm, "end": v(-112.7, 236.8) * mm});
            skLineSegment(sketch, "E2284", {"start": v(-112.7, 236.8) * mm, "end": v(-112.5, 236.45) * mm});
            skLineSegment(sketch, "E2285", {"start": v(-112.5, 236.45) * mm, "end": v(-112.32, 236.1) * mm});
            skLineSegment(sketch, "E2286", {"start": v(-112.32, 236.1) * mm, "end": v(-112.14, 235.74) * mm});
            skLineSegment(sketch, "E2287", {"start": v(-112.14, 235.74) * mm, "end": v(-111.97, 235.38) * mm});
            skLineSegment(sketch, "E2288", {"start": v(-111.97, 235.38) * mm, "end": v(-111.81, 235) * mm});
            skLineSegment(sketch, "E2289", {"start": v(-111.81, 235) * mm, "end": v(-111.67, 234.64) * mm});
            skLineSegment(sketch, "E2290", {"start": v(-111.67, 234.64) * mm, "end": v(-111.53, 234.26) * mm});
            skLineSegment(sketch, "E2291", {"start": v(-111.53, 234.26) * mm, "end": v(-111.4, 233.88) * mm});
            skLineSegment(sketch, "E2292", {"start": v(-111.4, 233.88) * mm, "end": v(-111.27, 233.5) * mm});
            skLineSegment(sketch, "E2293", {"start": v(-111.27, 233.5) * mm, "end": v(-111.16, 233.11) * mm});
            skLineSegment(sketch, "E2294", {"start": v(-111.16, 233.11) * mm, "end": v(-111.06, 232.72) * mm});
            skLineSegment(sketch, "E2295", {"start": v(-111.06, 232.72) * mm, "end": v(-110.97, 232.33) * mm});
            skLineSegment(sketch, "E2296", {"start": v(-110.97, 232.33) * mm, "end": v(-110.89, 231.94) * mm});
            skLineSegment(sketch, "E2297", {"start": v(-110.89, 231.94) * mm, "end": v(-110.82, 231.54) * mm});
            skLineSegment(sketch, "E2298", {"start": v(-110.82, 231.54) * mm, "end": v(-110.76, 231.14) * mm});
            skLineSegment(sketch, "E2299", {"start": v(-110.76, 231.14) * mm, "end": v(-110.7, 230.74) * mm});
            skLineSegment(sketch, "E2300", {"start": v(-110.7, 230.74) * mm, "end": v(-110.67, 230.34) * mm});
            skLineSegment(sketch, "E2301", {"start": v(-110.67, 230.34) * mm, "end": v(-110.64, 229.93) * mm});
            skLineSegment(sketch, "E2302", {"start": v(-110.64, 229.93) * mm, "end": v(-110.62, 229.53) * mm});
            skLineSegment(sketch, "E2303", {"start": v(-110.62, 229.53) * mm, "end": v(-110.6, 229.12) * mm});
            skLineSegment(sketch, "E2304", {"start": v(-110.6, 229.12) * mm, "end": v(-110.6, 228.72) * mm});
            skLineSegment(sketch, "E2305", {"start": v(-110.6, 228.72) * mm, "end": v(-110.61, 228.3) * mm});
            skLineSegment(sketch, "E2306", {"start": v(-110.61, 228.3) * mm, "end": v(-110.63, 227.89) * mm});
            skLineSegment(sketch, "E2307", {"start": v(-110.63, 227.89) * mm, "end": v(-110.65, 227.48) * mm});
            skLineSegment(sketch, "E2308", {"start": v(-110.65, 227.48) * mm, "end": v(-110.69, 227.07) * mm});
            skLineSegment(sketch, "E2309", {"start": v(-110.69, 227.07) * mm, "end": v(-110.73, 226.66) * mm});
            skLineSegment(sketch, "E2310", {"start": v(-110.73, 226.66) * mm, "end": v(-110.8, 226.25) * mm});
            skLineSegment(sketch, "E2311", {"start": v(-110.8, 226.25) * mm, "end": v(-110.86, 225.85) * mm});
            skLineSegment(sketch, "E2312", {"start": v(-110.86, 225.85) * mm, "end": v(-110.94, 225.44) * mm});
            skLineSegment(sketch, "E2313", {"start": v(-110.94, 225.44) * mm, "end": v(-111.02, 225.04) * mm});
            skLineSegment(sketch, "E2314", {"start": v(-111.02, 225.04) * mm, "end": v(-111.12, 224.65) * mm});
            skLineSegment(sketch, "E2315", {"start": v(-111.12, 224.65) * mm, "end": v(-111.23, 224.25) * mm});
            skLineSegment(sketch, "E2316", {"start": v(-111.23, 224.25) * mm, "end": v(-111.35, 223.86) * mm});
            skLineSegment(sketch, "E2317", {"start": v(-111.35, 223.86) * mm, "end": v(-111.47, 223.48) * mm});
            skLineSegment(sketch, "E2318", {"start": v(-111.47, 223.48) * mm, "end": v(-111.61, 223.1) * mm});
            skLineSegment(sketch, "E2319", {"start": v(-111.61, 223.1) * mm, "end": v(-111.76, 222.71) * mm});
            skLineSegment(sketch, "E2320", {"start": v(-111.76, 222.71) * mm, "end": v(-111.91, 222.33) * mm});
            skLineSegment(sketch, "E2321", {"start": v(-111.91, 222.33) * mm, "end": v(-112.08, 221.96) * mm});
            skLineSegment(sketch, "E2322", {"start": v(-112.08, 221.96) * mm, "end": v(-112.26, 221.6) * mm});
            skLineSegment(sketch, "E2323", {"start": v(-112.26, 221.6) * mm, "end": v(-112.44, 221.23) * mm});
            skLineSegment(sketch, "E2324", {"start": v(-112.44, 221.23) * mm, "end": v(-112.64, 220.87) * mm});
            skLineSegment(sketch, "E2325", {"start": v(-112.64, 220.87) * mm, "end": v(-112.84, 220.52) * mm});
            skLineSegment(sketch, "E2326", {"start": v(-112.84, 220.52) * mm, "end": v(-113.05, 220.17) * mm});
            skLineSegment(sketch, "E2327", {"start": v(-113.05, 220.17) * mm, "end": v(-113.27, 219.83) * mm});
            skLineSegment(sketch, "E2328", {"start": v(-113.27, 219.83) * mm, "end": v(-113.5, 219.49) * mm});
            skLineSegment(sketch, "E2329", {"start": v(-113.5, 219.49) * mm, "end": v(-113.74, 219.16) * mm});
            skLineSegment(sketch, "E2330", {"start": v(-113.74, 219.16) * mm, "end": v(-114, 218.83) * mm});
            skLineSegment(sketch, "E2331", {"start": v(-114, 218.83) * mm, "end": v(-114.25, 218.5) * mm});
            skLineSegment(sketch, "E2332", {"start": v(-114.25, 218.5) * mm, "end": v(-114.51, 218.2) * mm});
            skLineSegment(sketch, "E2333", {"start": v(-114.51, 218.2) * mm, "end": v(-114.79, 217.89) * mm});
            skLineSegment(sketch, "E2334", {"start": v(-114.79, 217.89) * mm, "end": v(-115.07, 217.59) * mm});
            skLineSegment(sketch, "E2335", {"start": v(-115.07, 217.59) * mm, "end": v(-115.36, 217.3) * mm});
            skLineSegment(sketch, "E2336", {"start": v(-115.36, 217.3) * mm, "end": v(-115.66, 217) * mm});
            skLineSegment(sketch, "E2337", {"start": v(-115.66, 217) * mm, "end": v(-116.07, 216.64) * mm});
            skLineSegment(sketch, "E2338", {"start": v(-116.07, 216.64) * mm, "end": v(-116.49, 216.28) * mm});
            skLineSegment(sketch, "E2339", {"start": v(-116.49, 216.28) * mm, "end": v(-116.91, 215.93) * mm});
            skLineSegment(sketch, "E2340", {"start": v(-116.91, 215.93) * mm, "end": v(-117.35, 215.6) * mm});
            skLineSegment(sketch, "E2341", {"start": v(-117.35, 215.6) * mm, "end": v(-117.79, 215.27) * mm});
            skLineSegment(sketch, "E2342", {"start": v(-117.79, 215.27) * mm, "end": v(-118.24, 214.95) * mm});
            skLineSegment(sketch, "E2343", {"start": v(-118.24, 214.95) * mm, "end": v(-118.7, 214.65) * mm});
            skLineSegment(sketch, "E2344", {"start": v(-118.7, 214.65) * mm, "end": v(-119.16, 214.36) * mm});
            skLineSegment(sketch, "E2345", {"start": v(-119.16, 214.36) * mm, "end": v(-119.63, 214.09) * mm});
            skLineSegment(sketch, "E2346", {"start": v(-119.63, 214.09) * mm, "end": v(-120.1, 213.82) * mm});
            skLineSegment(sketch, "E2347", {"start": v(-120.1, 213.82) * mm, "end": v(-120.58, 213.57) * mm});
            skLineSegment(sketch, "E2348", {"start": v(-120.58, 213.57) * mm, "end": v(-121.07, 213.32) * mm});
            skLineSegment(sketch, "E2349", {"start": v(-121.07, 213.32) * mm, "end": v(-121.56, 213.1) * mm});
            skLineSegment(sketch, "E2350", {"start": v(-121.56, 213.1) * mm, "end": v(-122.06, 212.88) * mm});
            skLineSegment(sketch, "E2351", {"start": v(-122.06, 212.88) * mm, "end": v(-122.57, 212.67) * mm});
            skLineSegment(sketch, "E2352", {"start": v(-122.57, 212.67) * mm, "end": v(-123.08, 212.48) * mm});
            skLineSegment(sketch, "E2353", {"start": v(-123.08, 212.48) * mm, "end": v(-123.59, 212.3) * mm});
            skLineSegment(sketch, "E2354", {"start": v(-123.59, 212.3) * mm, "end": v(-124.1, 212.13) * mm});
            skLineSegment(sketch, "E2355", {"start": v(-124.1, 212.13) * mm, "end": v(-124.63, 211.98) * mm});
            skLineSegment(sketch, "E2356", {"start": v(-124.63, 211.98) * mm, "end": v(-125.15, 211.84) * mm});
            skLineSegment(sketch, "E2357", {"start": v(-125.15, 211.84) * mm, "end": v(-125.68, 211.7) * mm});
            skLineSegment(sketch, "E2358", {"start": v(-125.68, 211.7) * mm, "end": v(-126.22, 211.6) * mm});
            skLineSegment(sketch, "E2359", {"start": v(-126.22, 211.6) * mm, "end": v(-126.75, 211.49) * mm});
            skLineSegment(sketch, "E2360", {"start": v(-126.75, 211.49) * mm, "end": v(-127.29, 211.4) * mm});
            skLineSegment(sketch, "E2361", {"start": v(-127.29, 211.4) * mm, "end": v(-127.83, 211.32) * mm});
            skLineSegment(sketch, "E2362", {"start": v(-127.83, 211.32) * mm, "end": v(-128.37, 211.26) * mm});
            skLineSegment(sketch, "E2363", {"start": v(-128.37, 211.26) * mm, "end": v(-128.92, 211.21) * mm});
            skLineSegment(sketch, "E2364", {"start": v(-128.92, 211.21) * mm, "end": v(-129.47, 211.18) * mm});
            skLineSegment(sketch, "E2365", {"start": v(-129.47, 211.18) * mm, "end": v(-130.01, 211.15) * mm});
            skLineSegment(sketch, "E2366", {"start": v(-130.01, 211.15) * mm, "end": v(-130.56, 211.15) * mm});
            skLineSegment(sketch, "E2367", {"start": v(-130.56, 211.15) * mm, "end": v(-131.12, 211.15) * mm});
            skLineSegment(sketch, "E2368", {"start": v(-131.12, 211.15) * mm, "end": v(-131.67, 211.17) * mm});
            skLineSegment(sketch, "E2369", {"start": v(-131.67, 211.17) * mm, "end": v(-132.18, 211.16) * mm});
            skLineSegment(sketch, "E2370", {"start": v(-132.18, 211.16) * mm, "end": v(-132.7, 211.17) * mm});
            skLineSegment(sketch, "E2371", {"start": v(-132.7, 211.17) * mm, "end": v(-133.2, 211.19) * mm});
            skLineSegment(sketch, "E2372", {"start": v(-133.2, 211.19) * mm, "end": v(-133.72, 211.22) * mm});
            skLineSegment(sketch, "E2373", {"start": v(-133.72, 211.22) * mm, "end": v(-134.23, 211.26) * mm});
            skLineSegment(sketch, "E2374", {"start": v(-134.23, 211.26) * mm, "end": v(-134.74, 211.32) * mm});
            skLineSegment(sketch, "E2375", {"start": v(-134.74, 211.32) * mm, "end": v(-135.24, 211.38) * mm});
            skLineSegment(sketch, "E2376", {"start": v(-135.24, 211.38) * mm, "end": v(-135.74, 211.46) * mm});
            skLineSegment(sketch, "E2377", {"start": v(-135.74, 211.46) * mm, "end": v(-136.24, 211.56) * mm});
            skLineSegment(sketch, "E2378", {"start": v(-136.24, 211.56) * mm, "end": v(-136.74, 211.66) * mm});
            skLineSegment(sketch, "E2379", {"start": v(-136.74, 211.66) * mm, "end": v(-137.24, 211.78) * mm});
            skLineSegment(sketch, "E2380", {"start": v(-137.24, 211.78) * mm, "end": v(-137.73, 211.91) * mm});
            skLineSegment(sketch, "E2381", {"start": v(-137.73, 211.91) * mm, "end": v(-138.21, 212.06) * mm});
            skLineSegment(sketch, "E2382", {"start": v(-138.21, 212.06) * mm, "end": v(-138.7, 212.21) * mm});
            skLineSegment(sketch, "E2383", {"start": v(-138.7, 212.21) * mm, "end": v(-139.18, 212.38) * mm});
            skLineSegment(sketch, "E2384", {"start": v(-139.18, 212.38) * mm, "end": v(-139.65, 212.55) * mm});
            skLineSegment(sketch, "E2385", {"start": v(-139.65, 212.55) * mm, "end": v(-140.12, 212.74) * mm});
            skLineSegment(sketch, "E2386", {"start": v(-140.12, 212.74) * mm, "end": v(-140.59, 212.95) * mm});
            skLineSegment(sketch, "E2387", {"start": v(-140.59, 212.95) * mm, "end": v(-141.05, 213.16) * mm});
            skLineSegment(sketch, "E2388", {"start": v(-141.05, 213.16) * mm, "end": v(-141.5, 213.38) * mm});
            skLineSegment(sketch, "E2389", {"start": v(-141.5, 213.38) * mm, "end": v(-141.95, 213.62) * mm});
            skLineSegment(sketch, "E2390", {"start": v(-141.95, 213.62) * mm, "end": v(-142.4, 213.87) * mm});
            skLineSegment(sketch, "E2391", {"start": v(-142.4, 213.87) * mm, "end": v(-142.84, 214.12) * mm});
            skLineSegment(sketch, "E2392", {"start": v(-142.84, 214.12) * mm, "end": v(-143.27, 214.4) * mm});
            skLineSegment(sketch, "E2393", {"start": v(-143.27, 214.4) * mm, "end": v(-143.7, 214.67) * mm});
            skLineSegment(sketch, "E2394", {"start": v(-143.7, 214.67) * mm, "end": v(-144.11, 214.96) * mm});
            skLineSegment(sketch, "E2395", {"start": v(-144.11, 214.96) * mm, "end": v(-144.52, 215.27) * mm});
            skLineSegment(sketch, "E2396", {"start": v(-144.52, 215.27) * mm, "end": v(-144.93, 215.58) * mm});
            skLineSegment(sketch, "E2397", {"start": v(-144.93, 215.58) * mm, "end": v(-145.32, 215.9) * mm});
            skLineSegment(sketch, "E2398", {"start": v(-145.32, 215.9) * mm, "end": v(-145.71, 216.24) * mm});
            skLineSegment(sketch, "E2399", {"start": v(-145.71, 216.24) * mm, "end": v(-146.1, 216.58) * mm});
            skLineSegment(sketch, "E2400", {"start": v(-146.1, 216.58) * mm, "end": v(-146.47, 216.93) * mm});
            skLineSegment(sketch, "E2401", {"start": v(-146.47, 216.93) * mm, "end": v(-146.76, 217.23) * mm});
            skLineSegment(sketch, "E2402", {"start": v(-146.76, 217.23) * mm, "end": v(-147.04, 217.53) * mm});
            skLineSegment(sketch, "E2403", {"start": v(-147.04, 217.53) * mm, "end": v(-147.32, 217.84) * mm});
            skLineSegment(sketch, "E2404", {"start": v(-147.32, 217.84) * mm, "end": v(-147.59, 218.15) * mm});
            skLineSegment(sketch, "E2405", {"start": v(-147.59, 218.15) * mm, "end": v(-147.84, 218.47) * mm});
            skLineSegment(sketch, "E2406", {"start": v(-147.84, 218.47) * mm, "end": v(-148.1, 218.8) * mm});
            skLineSegment(sketch, "E2407", {"start": v(-148.1, 218.8) * mm, "end": v(-148.34, 219.13) * mm});
            skLineSegment(sketch, "E2408", {"start": v(-148.34, 219.13) * mm, "end": v(-148.57, 219.46) * mm});
            skLineSegment(sketch, "E2409", {"start": v(-148.57, 219.46) * mm, "end": v(-148.8, 219.8) * mm});
            skLineSegment(sketch, "E2410", {"start": v(-148.8, 219.8) * mm, "end": v(-149, 220.15) * mm});
            skLineSegment(sketch, "E2411", {"start": v(-149, 220.15) * mm, "end": v(-149.21, 220.5) * mm});
            skLineSegment(sketch, "E2412", {"start": v(-149.21, 220.5) * mm, "end": v(-149.41, 220.86) * mm});
            skLineSegment(sketch, "E2413", {"start": v(-149.41, 220.86) * mm, "end": v(-149.6, 221.22) * mm});
            skLineSegment(sketch, "E2414", {"start": v(-149.6, 221.22) * mm, "end": v(-149.78, 221.59) * mm});
            skLineSegment(sketch, "E2415", {"start": v(-149.78, 221.59) * mm, "end": v(-149.95, 221.96) * mm});
            skLineSegment(sketch, "E2416", {"start": v(-149.95, 221.96) * mm, "end": v(-150.11, 222.33) * mm});
            skLineSegment(sketch, "E2417", {"start": v(-150.11, 222.33) * mm, "end": v(-150.26, 222.71) * mm});
            skLineSegment(sketch, "E2418", {"start": v(-150.26, 222.71) * mm, "end": v(-150.4, 223.1) * mm});
            skLineSegment(sketch, "E2419", {"start": v(-150.4, 223.1) * mm, "end": v(-150.54, 223.48) * mm});
            skLineSegment(sketch, "E2420", {"start": v(-150.54, 223.48) * mm, "end": v(-150.66, 223.87) * mm});
            skLineSegment(sketch, "E2421", {"start": v(-150.66, 223.87) * mm, "end": v(-150.77, 224.26) * mm});
            skLineSegment(sketch, "E2422", {"start": v(-150.77, 224.26) * mm, "end": v(-150.88, 224.66) * mm});
            skLineSegment(sketch, "E2423", {"start": v(-150.88, 224.66) * mm, "end": v(-150.97, 225.05) * mm});
            skLineSegment(sketch, "E2424", {"start": v(-150.97, 225.05) * mm, "end": v(-151.06, 225.45) * mm});
            skLineSegment(sketch, "E2425", {"start": v(-151.06, 225.45) * mm, "end": v(-151.13, 225.86) * mm});
            skLineSegment(sketch, "E2426", {"start": v(-151.13, 225.86) * mm, "end": v(-151.2, 226.26) * mm});
            skLineSegment(sketch, "E2427", {"start": v(-151.2, 226.26) * mm, "end": v(-151.25, 226.67) * mm});
            skLineSegment(sketch, "E2428", {"start": v(-151.25, 226.67) * mm, "end": v(-151.3, 227.08) * mm});
            skLineSegment(sketch, "E2429", {"start": v(-151.3, 227.08) * mm, "end": v(-151.33, 227.49) * mm});
            skLineSegment(sketch, "E2430", {"start": v(-151.33, 227.49) * mm, "end": v(-151.35, 227.9) * mm});
            skLineSegment(sketch, "E2431", {"start": v(-151.35, 227.9) * mm, "end": v(-151.37, 228.3) * mm});
            skLineSegment(sketch, "E2432", {"start": v(-151.37, 228.3) * mm, "end": v(-151.37, 228.72) * mm});
            skLineSegment(sketch, "E2433", {"start": v(-150.8, 202.15) * mm, "end": v(-110.85, 202.15) * mm});
            skLineSegment(sketch, "E2434", {"start": v(-110.85, 202.15) * mm, "end": v(-110.85, 184.59) * mm});
            skLineSegment(sketch, "E2435", {"start": v(-110.85, 184.59) * mm, "end": v(-110.85, 184.1) * mm});
            skLineSegment(sketch, "E2436", {"start": v(-110.85, 184.1) * mm, "end": v(-110.88, 183.6) * mm});
            skLineSegment(sketch, "E2437", {"start": v(-110.88, 183.6) * mm, "end": v(-110.94, 183.12) * mm});
            skLineSegment(sketch, "E2438", {"start": v(-110.94, 183.12) * mm, "end": v(-111.01, 182.63) * mm});
            skLineSegment(sketch, "E2439", {"start": v(-111.01, 182.63) * mm, "end": v(-111.12, 182.16) * mm});
            skLineSegment(sketch, "E2440", {"start": v(-111.12, 182.16) * mm, "end": v(-111.24, 181.69) * mm});
            skLineSegment(sketch, "E2441", {"start": v(-111.24, 181.69) * mm, "end": v(-111.4, 181.22) * mm});
            skLineSegment(sketch, "E2442", {"start": v(-111.4, 181.22) * mm, "end": v(-111.57, 180.77) * mm});
            skLineSegment(sketch, "E2443", {"start": v(-111.57, 180.77) * mm, "end": v(-111.77, 180.32) * mm});
            skLineSegment(sketch, "E2444", {"start": v(-111.77, 180.32) * mm, "end": v(-111.99, 179.89) * mm});
            skLineSegment(sketch, "E2445", {"start": v(-111.99, 179.89) * mm, "end": v(-112.23, 179.46) * mm});
            skLineSegment(sketch, "E2446", {"start": v(-112.23, 179.46) * mm, "end": v(-112.49, 179.05) * mm});
            skLineSegment(sketch, "E2447", {"start": v(-112.49, 179.05) * mm, "end": v(-112.77, 178.65) * mm});
            skLineSegment(sketch, "E2448", {"start": v(-112.77, 178.65) * mm, "end": v(-113.08, 178.27) * mm});
            skLineSegment(sketch, "E2449", {"start": v(-113.08, 178.27) * mm, "end": v(-113.4, 177.9) * mm});
            skLineSegment(sketch, "E2450", {"start": v(-113.4, 177.9) * mm, "end": v(-113.75, 177.55) * mm});
            skLineSegment(sketch, "E2451", {"start": v(-113.75, 177.55) * mm, "end": v(-114.1, 177.2) * mm});
            skLineSegment(sketch, "E2452", {"start": v(-114.1, 177.2) * mm, "end": v(-114.47, 176.89) * mm});
            skLineSegment(sketch, "E2453", {"start": v(-114.47, 176.89) * mm, "end": v(-114.85, 176.58) * mm});
            skLineSegment(sketch, "E2454", {"start": v(-114.85, 176.58) * mm, "end": v(-115.24, 176.3) * mm});
            skLineSegment(sketch, "E2455", {"start": v(-115.24, 176.3) * mm, "end": v(-115.65, 176.04) * mm});
            skLineSegment(sketch, "E2456", {"start": v(-115.65, 176.04) * mm, "end": v(-116.07, 175.8) * mm});
            skLineSegment(sketch, "E2457", {"start": v(-116.07, 175.8) * mm, "end": v(-116.5, 175.58) * mm});
            skLineSegment(sketch, "E2458", {"start": v(-116.5, 175.58) * mm, "end": v(-116.94, 175.39) * mm});
            skLineSegment(sketch, "E2459", {"start": v(-116.94, 175.39) * mm, "end": v(-117.4, 175.21) * mm});
            skLineSegment(sketch, "E2460", {"start": v(-117.4, 175.21) * mm, "end": v(-117.85, 175.06) * mm});
            skLineSegment(sketch, "E2461", {"start": v(-117.85, 175.06) * mm, "end": v(-118.32, 174.93) * mm});
            skLineSegment(sketch, "E2462", {"start": v(-118.32, 174.93) * mm, "end": v(-118.79, 174.82) * mm});
            skLineSegment(sketch, "E2463", {"start": v(-118.79, 174.82) * mm, "end": v(-119.27, 174.74) * mm});
            skLineSegment(sketch, "E2464", {"start": v(-119.27, 174.74) * mm, "end": v(-119.75, 174.68) * mm});
            skLineSegment(sketch, "E2465", {"start": v(-119.75, 174.68) * mm, "end": v(-120.24, 174.64) * mm});
            skLineSegment(sketch, "E2466", {"start": v(-120.24, 174.64) * mm, "end": v(-120.73, 174.63) * mm});
            skLineSegment(sketch, "E2467", {"start": v(-120.73, 174.63) * mm, "end": v(-121.23, 174.63) * mm});
            skLineSegment(sketch, "E2468", {"start": v(-121.23, 174.63) * mm, "end": v(-121.73, 174.65) * mm});
            skLineSegment(sketch, "E2469", {"start": v(-121.73, 174.65) * mm, "end": v(-122.22, 174.7) * mm});
            skLineSegment(sketch, "E2470", {"start": v(-122.22, 174.7) * mm, "end": v(-122.71, 174.77) * mm});
            skLineSegment(sketch, "E2471", {"start": v(-122.71, 174.77) * mm, "end": v(-123.2, 174.87) * mm});
            skLineSegment(sketch, "E2472", {"start": v(-123.2, 174.87) * mm, "end": v(-123.68, 175) * mm});
            skLineSegment(sketch, "E2473", {"start": v(-123.68, 175) * mm, "end": v(-124.15, 175.14) * mm});
            skLineSegment(sketch, "E2474", {"start": v(-124.15, 175.14) * mm, "end": v(-124.62, 175.3) * mm});
            skLineSegment(sketch, "E2475", {"start": v(-124.62, 175.3) * mm, "end": v(-125.07, 175.5) * mm});
            skLineSegment(sketch, "E2476", {"start": v(-125.07, 175.5) * mm, "end": v(-125.52, 175.72) * mm});
            skLineSegment(sketch, "E2477", {"start": v(-125.52, 175.72) * mm, "end": v(-125.95, 175.95) * mm});
            skLineSegment(sketch, "E2478", {"start": v(-125.95, 175.95) * mm, "end": v(-126.37, 176.21) * mm});
            skLineSegment(sketch, "E2479", {"start": v(-126.37, 176.21) * mm, "end": v(-126.78, 176.5) * mm});
            skLineSegment(sketch, "E2480", {"start": v(-126.78, 176.5) * mm, "end": v(-127.18, 176.8) * mm});
            skLineSegment(sketch, "E2481", {"start": v(-127.18, 176.8) * mm, "end": v(-127.56, 177.12) * mm});
            skLineSegment(sketch, "E2482", {"start": v(-127.56, 177.12) * mm, "end": v(-127.92, 177.47) * mm});
            skLineSegment(sketch, "E2483", {"start": v(-127.92, 177.47) * mm, "end": v(-128.26, 177.83) * mm});
            skLineSegment(sketch, "E2484", {"start": v(-128.26, 177.83) * mm, "end": v(-128.59, 178.2) * mm});
            skLineSegment(sketch, "E2485", {"start": v(-128.59, 178.2) * mm, "end": v(-128.9, 178.6) * mm});
            skLineSegment(sketch, "E2486", {"start": v(-128.9, 178.6) * mm, "end": v(-129.18, 179) * mm});
            skLineSegment(sketch, "E2487", {"start": v(-129.18, 179) * mm, "end": v(-129.44, 179.42) * mm});
            skLineSegment(sketch, "E2488", {"start": v(-129.44, 179.42) * mm, "end": v(-129.68, 179.84) * mm});
            skLineSegment(sketch, "E2489", {"start": v(-129.68, 179.84) * mm, "end": v(-129.9, 180.28) * mm});
            skLineSegment(sketch, "E2490", {"start": v(-129.9, 180.28) * mm, "end": v(-130.1, 180.73) * mm});
            skLineSegment(sketch, "E2491", {"start": v(-130.1, 180.73) * mm, "end": v(-130.27, 181.2) * mm});
            skLineSegment(sketch, "E2492", {"start": v(-130.27, 181.2) * mm, "end": v(-130.42, 181.66) * mm});
            skLineSegment(sketch, "E2493", {"start": v(-130.42, 181.66) * mm, "end": v(-130.54, 182.14) * mm});
            skLineSegment(sketch, "E2494", {"start": v(-130.54, 182.14) * mm, "end": v(-130.65, 182.62) * mm});
            skLineSegment(sketch, "E2495", {"start": v(-130.65, 182.62) * mm, "end": v(-130.73, 183.1) * mm});
            skLineSegment(sketch, "E2496", {"start": v(-130.73, 183.1) * mm, "end": v(-130.78, 183.6) * mm});
            skLineSegment(sketch, "E2497", {"start": v(-130.78, 183.6) * mm, "end": v(-130.81, 184.1) * mm});
            skLineSegment(sketch, "E2498", {"start": v(-130.81, 184.1) * mm, "end": v(-130.82, 184.59) * mm});
            skLineSegment(sketch, "E2499", {"start": v(-130.82, 184.59) * mm, "end": v(-130.82, 202.15) * mm});
            skLineSegment(sketch, "E2500", {"start": v(-130.82, 184.59) * mm, "end": v(-130.82, 184.18) * mm});
            skLineSegment(sketch, "E2501", {"start": v(-130.82, 184.18) * mm, "end": v(-130.84, 183.77) * mm});
            skLineSegment(sketch, "E2502", {"start": v(-130.84, 183.77) * mm, "end": v(-130.89, 183.37) * mm});
            skLineSegment(sketch, "E2503", {"start": v(-130.89, 183.37) * mm, "end": v(-130.95, 182.97) * mm});
            skLineSegment(sketch, "E2504", {"start": v(-130.95, 182.97) * mm, "end": v(-131.04, 182.57) * mm});
            skLineSegment(sketch, "E2505", {"start": v(-131.04, 182.57) * mm, "end": v(-131.14, 182.18) * mm});
            skLineSegment(sketch, "E2506", {"start": v(-131.14, 182.18) * mm, "end": v(-131.26, 181.8) * mm});
            skLineSegment(sketch, "E2507", {"start": v(-131.26, 181.8) * mm, "end": v(-131.4, 181.42) * mm});
            skLineSegment(sketch, "E2508", {"start": v(-131.4, 181.42) * mm, "end": v(-131.57, 181.05) * mm});
            skLineSegment(sketch, "E2509", {"start": v(-131.57, 181.05) * mm, "end": v(-131.75, 180.69) * mm});
            skLineSegment(sketch, "E2510", {"start": v(-131.75, 180.69) * mm, "end": v(-131.95, 180.33) * mm});
            skLineSegment(sketch, "E2511", {"start": v(-131.95, 180.33) * mm, "end": v(-132.16, 180) * mm});
            skLineSegment(sketch, "E2512", {"start": v(-132.16, 180) * mm, "end": v(-132.4, 179.66) * mm});
            skLineSegment(sketch, "E2513", {"start": v(-132.4, 179.66) * mm, "end": v(-132.65, 179.34) * mm});
            skLineSegment(sketch, "E2514", {"start": v(-132.65, 179.34) * mm, "end": v(-132.92, 179.03) * mm});
            skLineSegment(sketch, "E2515", {"start": v(-132.92, 179.03) * mm, "end": v(-133.2, 178.74) * mm});
            skLineSegment(sketch, "E2516", {"start": v(-133.2, 178.74) * mm, "end": v(-133.7, 178.4) * mm});
            skLineSegment(sketch, "E2517", {"start": v(-133.7, 178.4) * mm, "end": v(-134.22, 178.08) * mm});
            skLineSegment(sketch, "E2518", {"start": v(-134.22, 178.08) * mm, "end": v(-134.74, 177.79) * mm});
            skLineSegment(sketch, "E2519", {"start": v(-134.74, 177.79) * mm, "end": v(-135.28, 177.52) * mm});
            skLineSegment(sketch, "E2520", {"start": v(-135.28, 177.52) * mm, "end": v(-135.83, 177.27) * mm});
            skLineSegment(sketch, "E2521", {"start": v(-135.83, 177.27) * mm, "end": v(-136.38, 177.05) * mm});
            skLineSegment(sketch, "E2522", {"start": v(-136.38, 177.05) * mm, "end": v(-136.95, 176.86) * mm});
            skLineSegment(sketch, "E2523", {"start": v(-136.95, 176.86) * mm, "end": v(-137.52, 176.7) * mm});
            skLineSegment(sketch, "E2524", {"start": v(-137.52, 176.7) * mm, "end": v(-138.1, 176.55) * mm});
            skLineSegment(sketch, "E2525", {"start": v(-138.1, 176.55) * mm, "end": v(-138.7, 176.43) * mm});
            skLineSegment(sketch, "E2526", {"start": v(-138.7, 176.43) * mm, "end": v(-139.28, 176.34) * mm});
            skLineSegment(sketch, "E2527", {"start": v(-139.28, 176.34) * mm, "end": v(-139.88, 176.27) * mm});
            skLineSegment(sketch, "E2528", {"start": v(-139.88, 176.27) * mm, "end": v(-140.48, 176.23) * mm});
            skLineSegment(sketch, "E2529", {"start": v(-140.48, 176.23) * mm, "end": v(-141.08, 176.22) * mm});
            skLineSegment(sketch, "E2530", {"start": v(-141.08, 176.22) * mm, "end": v(-141.69, 176.24) * mm});
            skLineSegment(sketch, "E2531", {"start": v(-141.69, 176.24) * mm, "end": v(-142.29, 176.28) * mm});
            skLineSegment(sketch, "E2532", {"start": v(-142.29, 176.28) * mm, "end": v(-142.83, 176.29) * mm});
            skLineSegment(sketch, "E2533", {"start": v(-142.83, 176.29) * mm, "end": v(-143.36, 176.28) * mm});
            skLineSegment(sketch, "E2534", {"start": v(-143.36, 176.28) * mm, "end": v(-143.9, 176.27) * mm});
            skLineSegment(sketch, "E2535", {"start": v(-143.9, 176.27) * mm, "end": v(-144.44, 176.25) * mm});
            skLineSegment(sketch, "E2536", {"start": v(-144.44, 176.25) * mm, "end": v(-144.98, 176.22) * mm});
            skLineSegment(sketch, "E2537", {"start": v(-144.98, 176.22) * mm, "end": v(-145.51, 176.18) * mm});
            skLineSegment(sketch, "E2538", {"start": v(-145.51, 176.18) * mm, "end": v(-146.05, 176.13) * mm});
            skLineSegment(sketch, "E2539", {"start": v(-146.05, 176.13) * mm, "end": v(-146.59, 176.07) * mm});
            skLineSegment(sketch, "E2540", {"start": v(-146.59, 176.07) * mm, "end": v(-147.12, 176) * mm});
            skLineSegment(sketch, "E2541", {"start": v(-147.12, 176) * mm, "end": v(-147.65, 175.92) * mm});
            skLineSegment(sketch, "E2542", {"start": v(-147.65, 175.92) * mm, "end": v(-148.18, 175.83) * mm});
            skLineSegment(sketch, "E2543", {"start": v(-148.18, 175.83) * mm, "end": v(-148.71, 175.73) * mm});
            skLineSegment(sketch, "E2544", {"start": v(-148.71, 175.73) * mm, "end": v(-149.24, 175.63) * mm});
            skLineSegment(sketch, "E2545", {"start": v(-149.24, 175.63) * mm, "end": v(-149.77, 175.5) * mm});
            skLineSegment(sketch, "E2546", {"start": v(-149.77, 175.5) * mm, "end": v(-150.29, 175.38) * mm});
            skLineSegment(sketch, "E2547", {"start": v(-150.29, 175.38) * mm, "end": v(-150.8, 175.25) * mm});
            skArc(sketch, "E2548", {"start": v(-573.41, 1165.93) * mm, "mid": v(-576.07, 1164.83) * mm, "end": v(-577.16, 1162.18) * mm});
            skArc(sketch, "E2549", {"start": v(-577.16, 1162.18) * mm, "mid": v(-576.07, 1159.53) * mm, "end": v(-573.41, 1158.43) * mm});
            skArc(sketch, "E2550", {"start": v(-573.41, 1158.43) * mm, "mid": v(-570.76, 1159.53) * mm, "end": v(-569.66, 1162.18) * mm});
            skArc(sketch, "E2551", {"start": v(-569.66, 1162.18) * mm, "mid": v(-570.76, 1164.83) * mm, "end": v(-573.41, 1165.93) * mm});
            skArc(sketch, "E2552", {"start": v(-573.5, 494.64) * mm, "mid": v(-576.15, 493.54) * mm, "end": v(-577.24, 490.89) * mm});
            skArc(sketch, "E2553", {"start": v(-577.24, 490.89) * mm, "mid": v(-576.15, 488.24) * mm, "end": v(-573.5, 487.14) * mm});
            skArc(sketch, "E2554", {"start": v(-573.5, 487.14) * mm, "mid": v(-570.84, 488.24) * mm, "end": v(-569.74, 490.89) * mm});
            skArc(sketch, "E2555", {"start": v(-569.74, 490.89) * mm, "mid": v(-570.84, 493.54) * mm, "end": v(-573.5, 494.64) * mm});
            skArc(sketch, "E2556", {"start": v(-578.19, -186.04) * mm, "mid": v(-580.84, -187.14) * mm, "end": v(-581.94, -189.8) * mm});
            skArc(sketch, "E2557", {"start": v(-581.94, -189.8) * mm, "mid": v(-580.84, -192.45) * mm, "end": v(-578.19, -193.54) * mm});
            skArc(sketch, "E2558", {"start": v(-578.19, -193.54) * mm, "mid": v(-575.54, -192.45) * mm, "end": v(-574.44, -189.8) * mm});
            skArc(sketch, "E2559", {"start": v(-574.44, -189.8) * mm, "mid": v(-575.54, -187.14) * mm, "end": v(-578.19, -186.04) * mm});
            skArc(sketch, "E2560", {"start": v(-585.06, -696.15) * mm, "mid": v(-587.71, -697.25) * mm, "end": v(-588.81, -699.9) * mm});
            skArc(sketch, "E2561", {"start": v(-588.81, -699.9) * mm, "mid": v(-587.71, -702.55) * mm, "end": v(-585.06, -703.65) * mm});
            skArc(sketch, "E2562", {"start": v(-585.06, -703.65) * mm, "mid": v(-582.4, -702.55) * mm, "end": v(-581.31, -699.9) * mm});
            skArc(sketch, "E2563", {"start": v(-581.31, -699.9) * mm, "mid": v(-582.4, -697.25) * mm, "end": v(-585.06, -696.15) * mm});
            skArc(sketch, "E2564", {"start": v(505, -791.3) * mm, "mid": v(502.35, -792.4) * mm, "end": v(501.25, -795.04) * mm});
            skArc(sketch, "E2565", {"start": v(501.25, -795.04) * mm, "mid": v(502.35, -797.7) * mm, "end": v(505, -798.8) * mm});
            skArc(sketch, "E2566", {"start": v(505, -798.8) * mm, "mid": v(507.65, -797.7) * mm, "end": v(508.75, -795.04) * mm});
            skArc(sketch, "E2567", {"start": v(508.75, -795.04) * mm, "mid": v(507.65, -792.4) * mm, "end": v(505, -791.3) * mm});
            skArc(sketch, "E2568", {"start": v(291.18, -592.86) * mm, "mid": v(288.53, -593.96) * mm, "end": v(287.43, -596.6) * mm});
            skArc(sketch, "E2569", {"start": v(287.43, -596.6) * mm, "mid": v(288.53, -599.26) * mm, "end": v(291.18, -600.36) * mm});
            skArc(sketch, "E2570", {"start": v(291.18, -600.36) * mm, "mid": v(293.83, -599.26) * mm, "end": v(294.93, -596.6) * mm});
            skArc(sketch, "E2571", {"start": v(294.93, -596.6) * mm, "mid": v(293.83, -593.96) * mm, "end": v(291.18, -592.86) * mm});
            skArc(sketch, "E2572", {"start": v(80.44, -777.45) * mm, "mid": v(77.8, -778.55) * mm, "end": v(76.7, -781.2) * mm});
            skArc(sketch, "E2573", {"start": v(76.7, -781.2) * mm, "mid": v(77.8, -783.85) * mm, "end": v(80.44, -784.95) * mm});
            skArc(sketch, "E2574", {"start": v(80.44, -784.95) * mm, "mid": v(83.1, -783.85) * mm, "end": v(84.2, -781.2) * mm});
            skArc(sketch, "E2575", {"start": v(84.2, -781.2) * mm, "mid": v(83.1, -778.55) * mm, "end": v(80.44, -777.45) * mm});
            skArc(sketch, "E2576", {"start": v(-147.22, -748.22) * mm, "mid": v(-149.87, -749.32) * mm, "end": v(-150.97, -751.97) * mm});
            skArc(sketch, "E2577", {"start": v(-150.97, -751.97) * mm, "mid": v(-149.87, -754.62) * mm, "end": v(-147.22, -755.72) * mm});
            skArc(sketch, "E2578", {"start": v(-147.22, -755.72) * mm, "mid": v(-144.57, -754.62) * mm, "end": v(-143.47, -751.97) * mm});
            skArc(sketch, "E2579", {"start": v(-143.47, -751.97) * mm, "mid": v(-144.57, -749.32) * mm, "end": v(-147.22, -748.22) * mm});
            skArc(sketch, "E2580", {"start": v(-361.03, -806.67) * mm, "mid": v(-363.69, -807.77) * mm, "end": v(-364.78, -810.42) * mm});
            skArc(sketch, "E2581", {"start": v(-364.78, -810.42) * mm, "mid": v(-363.69, -813.08) * mm, "end": v(-361.03, -814.17) * mm});
            skArc(sketch, "E2582", {"start": v(-361.03, -814.17) * mm, "mid": v(-358.38, -813.08) * mm, "end": v(-357.28, -810.42) * mm});
            skArc(sketch, "E2583", {"start": v(-357.28, -810.42) * mm, "mid": v(-358.38, -807.77) * mm, "end": v(-361.03, -806.67) * mm});
            skArc(sketch, "E2584", {"start": v(-267.72, -332.87) * mm, "mid": v(-270.37, -333.97) * mm, "end": v(-271.47, -336.62) * mm});
            skArc(sketch, "E2585", {"start": v(-271.47, -336.62) * mm, "mid": v(-270.37, -339.27) * mm, "end": v(-267.72, -340.37) * mm});
            skArc(sketch, "E2586", {"start": v(-267.72, -340.37) * mm, "mid": v(-265.07, -339.27) * mm, "end": v(-263.97, -336.62) * mm});
            skArc(sketch, "E2587", {"start": v(-263.97, -336.62) * mm, "mid": v(-265.07, -333.97) * mm, "end": v(-267.72, -332.87) * mm});
            skArc(sketch, "E2588", {"start": v(-267.72, 240.9) * mm, "mid": v(-270.37, 239.8) * mm, "end": v(-271.47, 237.15) * mm});
            skArc(sketch, "E2589", {"start": v(-271.47, 237.15) * mm, "mid": v(-270.37, 234.5) * mm, "end": v(-267.72, 233.4) * mm});
            skArc(sketch, "E2590", {"start": v(-267.72, 233.4) * mm, "mid": v(-265.07, 234.5) * mm, "end": v(-263.97, 237.15) * mm});
            skArc(sketch, "E2591", {"start": v(-263.97, 237.15) * mm, "mid": v(-265.07, 239.8) * mm, "end": v(-267.72, 240.9) * mm});
            skArc(sketch, "E2592", {"start": v(-267.72, 800.82) * mm, "mid": v(-270.37, 799.72) * mm, "end": v(-271.47, 797.07) * mm});
            skArc(sketch, "E2593", {"start": v(-271.47, 797.07) * mm, "mid": v(-270.37, 794.42) * mm, "end": v(-267.72, 793.32) * mm});
            skArc(sketch, "E2594", {"start": v(-267.72, 793.32) * mm, "mid": v(-265.07, 794.42) * mm, "end": v(-263.97, 797.07) * mm});
            skArc(sketch, "E2595", {"start": v(-263.97, 797.07) * mm, "mid": v(-265.07, 799.72) * mm, "end": v(-267.72, 800.82) * mm});
            skArc(sketch, "E2596", {"start": v(12.24, 565.46) * mm, "mid": v(9.6, 564.37) * mm, "end": v(8.5, 561.71) * mm});
            skArc(sketch, "E2597", {"start": v(8.5, 561.71) * mm, "mid": v(9.6, 559.06) * mm, "end": v(12.24, 557.96) * mm});
            skArc(sketch, "E2598", {"start": v(12.24, 557.96) * mm, "mid": v(14.9, 559.06) * mm, "end": v(16, 561.71) * mm});
            skArc(sketch, "E2599", {"start": v(16, 561.71) * mm, "mid": v(14.9, 564.37) * mm, "end": v(12.24, 565.46) * mm});
            skArc(sketch, "E2600", {"start": v(292.2, 810.05) * mm, "mid": v(289.55, 808.95) * mm, "end": v(288.45, 806.3) * mm});
            skArc(sketch, "E2601", {"start": v(288.45, 806.3) * mm, "mid": v(289.55, 803.64) * mm, "end": v(292.2, 802.55) * mm});
            skArc(sketch, "E2602", {"start": v(292.2, 802.55) * mm, "mid": v(294.85, 803.64) * mm, "end": v(295.95, 806.3) * mm});
            skArc(sketch, "E2603", {"start": v(295.95, 806.3) * mm, "mid": v(294.85, 808.95) * mm, "end": v(292.2, 810.05) * mm});
            skArc(sketch, "E2604", {"start": v(570.63, 1183.84) * mm, "mid": v(567.97, 1182.74) * mm, "end": v(566.88, 1180.09) * mm});
            skArc(sketch, "E2605", {"start": v(566.88, 1180.09) * mm, "mid": v(567.97, 1177.44) * mm, "end": v(570.63, 1176.34) * mm});
            skArc(sketch, "E2606", {"start": v(570.63, 1176.34) * mm, "mid": v(573.28, 1177.44) * mm, "end": v(574.38, 1180.09) * mm});
            skArc(sketch, "E2607", {"start": v(574.38, 1180.09) * mm, "mid": v(573.28, 1182.74) * mm, "end": v(570.63, 1183.84) * mm});
            skArc(sketch, "E2608", {"start": v(10.7, 1186.92) * mm, "mid": v(8.05, 1185.82) * mm, "end": v(6.95, 1183.17) * mm});
            skArc(sketch, "E2609", {"start": v(6.95, 1183.17) * mm, "mid": v(8.05, 1180.52) * mm, "end": v(10.7, 1179.42) * mm});
            skArc(sketch, "E2610", {"start": v(10.7, 1179.42) * mm, "mid": v(13.36, 1180.52) * mm, "end": v(14.45, 1183.17) * mm});
            skArc(sketch, "E2611", {"start": v(14.45, 1183.17) * mm, "mid": v(13.36, 1185.82) * mm, "end": v(10.7, 1186.92) * mm});
            skArc(sketch, "E2612", {"start": v(291.72, 212.98) * mm, "mid": v(289.07, 211.88) * mm, "end": v(287.97, 209.23) * mm});
            skArc(sketch, "E2613", {"start": v(287.97, 209.23) * mm, "mid": v(289.07, 206.57) * mm, "end": v(291.72, 205.48) * mm});
            skArc(sketch, "E2614", {"start": v(291.72, 205.48) * mm, "mid": v(294.37, 206.57) * mm, "end": v(295.47, 209.23) * mm});
            skArc(sketch, "E2615", {"start": v(295.47, 209.23) * mm, "mid": v(294.37, 211.88) * mm, "end": v(291.72, 212.98) * mm});
            skArc(sketch, "E2616", {"start": v(571.53, 525.49) * mm, "mid": v(568.88, 524.4) * mm, "end": v(567.78, 521.74) * mm});
            skArc(sketch, "E2617", {"start": v(567.78, 521.74) * mm, "mid": v(568.88, 519.09) * mm, "end": v(571.53, 517.99) * mm});
            skArc(sketch, "E2618", {"start": v(571.53, 517.99) * mm, "mid": v(574.18, 519.09) * mm, "end": v(575.28, 521.74) * mm});
            skArc(sketch, "E2619", {"start": v(575.28, 521.74) * mm, "mid": v(574.18, 524.4) * mm, "end": v(571.53, 525.49) * mm});
            skArc(sketch, "E2620", {"start": v(11.3, -111.82) * mm, "mid": v(8.64, -112.92) * mm, "end": v(7.55, -115.57) * mm});
            skArc(sketch, "E2621", {"start": v(7.55, -115.57) * mm, "mid": v(8.64, -118.23) * mm, "end": v(11.3, -119.32) * mm});
            skArc(sketch, "E2622", {"start": v(11.3, -119.32) * mm, "mid": v(13.95, -118.23) * mm, "end": v(15.05, -115.57) * mm});
            skArc(sketch, "E2623", {"start": v(15.05, -115.57) * mm, "mid": v(13.95, -112.92) * mm, "end": v(11.3, -111.82) * mm});
            skArc(sketch, "E2624", {"start": v(573.17, -268.2) * mm, "mid": v(570.52, -269.3) * mm, "end": v(569.42, -271.95) * mm});
            skArc(sketch, "E2625", {"start": v(569.42, -271.95) * mm, "mid": v(570.52, -274.6) * mm, "end": v(573.17, -275.7) * mm});
            skArc(sketch, "E2626", {"start": v(573.17, -275.7) * mm, "mid": v(575.82, -274.6) * mm, "end": v(576.92, -271.95) * mm});
            skArc(sketch, "E2627", {"start": v(576.92, -271.95) * mm, "mid": v(575.82, -269.3) * mm, "end": v(573.17, -268.2) * mm});
            skArc(sketch, "E2628", {"start": v(-411.34, -457.08) * mm, "mid": v(-414, -458.18) * mm, "end": v(-415.1, -460.83) * mm});
            skArc(sketch, "E2629", {"start": v(-415.1, -460.83) * mm, "mid": v(-414, -463.48) * mm, "end": v(-411.34, -464.58) * mm});
            skArc(sketch, "E2630", {"start": v(-411.34, -464.58) * mm, "mid": v(-408.7, -463.48) * mm, "end": v(-407.6, -460.83) * mm});
            skArc(sketch, "E2631", {"start": v(-407.6, -460.83) * mm, "mid": v(-408.7, -458.18) * mm, "end": v(-411.34, -457.08) * mm});
            skArc(sketch, "E2632", {"start": v(-406.65, 73.38) * mm, "mid": v(-409.3, 72.28) * mm, "end": v(-410.4, 69.63) * mm});
            skArc(sketch, "E2633", {"start": v(-410.4, 69.63) * mm, "mid": v(-409.3, 66.98) * mm, "end": v(-406.65, 65.88) * mm});
            skArc(sketch, "E2634", {"start": v(-406.65, 65.88) * mm, "mid": v(-404, 66.98) * mm, "end": v(-402.9, 69.63) * mm});
            skArc(sketch, "E2635", {"start": v(-402.9, 69.63) * mm, "mid": v(-404, 72.28) * mm, "end": v(-406.65, 73.38) * mm});
            skArc(sketch, "E2636", {"start": v(-420.73, 960.61) * mm, "mid": v(-423.38, 959.52) * mm, "end": v(-424.48, 956.86) * mm});
            skArc(sketch, "E2637", {"start": v(-424.48, 956.86) * mm, "mid": v(-423.38, 954.21) * mm, "end": v(-420.73, 953.11) * mm});
            skArc(sketch, "E2638", {"start": v(-420.73, 953.11) * mm, "mid": v(-418.08, 954.21) * mm, "end": v(-416.98, 956.86) * mm});
            skArc(sketch, "E2639", {"start": v(-416.98, 956.86) * mm, "mid": v(-418.08, 959.52) * mm, "end": v(-420.73, 960.61) * mm});
            skArc(sketch, "E2640", {"start": v(-124.99, 1007.56) * mm, "mid": v(-127.64, 1006.46) * mm, "end": v(-128.74, 1003.8) * mm});
            skArc(sketch, "E2641", {"start": v(-128.74, 1003.8) * mm, "mid": v(-127.64, 1001.16) * mm, "end": v(-124.99, 1000.06) * mm});
            skArc(sketch, "E2642", {"start": v(-124.99, 1000.06) * mm, "mid": v(-122.34, 1001.16) * mm, "end": v(-121.24, 1003.8) * mm});
            skArc(sketch, "E2643", {"start": v(-121.24, 1003.8) * mm, "mid": v(-122.34, 1006.46) * mm, "end": v(-124.99, 1007.56) * mm});
            skArc(sketch, "E2644", {"start": v(-139.07, 472.4) * mm, "mid": v(-141.72, 471.3) * mm, "end": v(-142.82, 468.65) * mm});
            skArc(sketch, "E2645", {"start": v(-142.82, 468.65) * mm, "mid": v(-141.72, 466) * mm, "end": v(-139.07, 464.9) * mm});
            skArc(sketch, "E2646", {"start": v(-139.07, 464.9) * mm, "mid": v(-136.42, 466) * mm, "end": v(-135.32, 468.65) * mm});
            skArc(sketch, "E2647", {"start": v(-135.32, 468.65) * mm, "mid": v(-136.42, 471.3) * mm, "end": v(-139.07, 472.4) * mm});
            skArc(sketch, "E2648", {"start": v(-134.38, -250.53) * mm, "mid": v(-137.03, -251.63) * mm, "end": v(-138.13, -254.28) * mm});
            skArc(sketch, "E2649", {"start": v(-138.13, -254.28) * mm, "mid": v(-137.03, -256.93) * mm, "end": v(-134.38, -258.03) * mm});
            skArc(sketch, "E2650", {"start": v(-134.38, -258.03) * mm, "mid": v(-131.72, -256.93) * mm, "end": v(-130.63, -254.28) * mm});
            skArc(sketch, "E2651", {"start": v(-130.63, -254.28) * mm, "mid": v(-131.72, -251.63) * mm, "end": v(-134.38, -250.53) * mm});
            skArc(sketch, "E2652", {"start": v(147.28, -448.44) * mm, "mid": v(145.16, -449.32) * mm, "end": v(144.28, -451.44) * mm});
            skArc(sketch, "E2653", {"start": v(144.28, -451.44) * mm, "mid": v(145.16, -453.56) * mm, "end": v(147.28, -454.44) * mm});
            skArc(sketch, "E2654", {"start": v(147.28, -454.44) * mm, "mid": v(149.4, -453.56) * mm, "end": v(150.28, -451.44) * mm});
            skArc(sketch, "E2655", {"start": v(150.28, -451.44) * mm, "mid": v(149.4, -449.32) * mm, "end": v(147.28, -448.44) * mm});
            skArc(sketch, "E2656", {"start": v(151.98, 100.8) * mm, "mid": v(149.86, 99.92) * mm, "end": v(148.98, 97.8) * mm});
            skArc(sketch, "E2657", {"start": v(148.98, 97.8) * mm, "mid": v(149.86, 95.68) * mm, "end": v(151.98, 94.8) * mm});
            skArc(sketch, "E2658", {"start": v(151.98, 94.8) * mm, "mid": v(154.1, 95.68) * mm, "end": v(154.98, 97.8) * mm});
            skArc(sketch, "E2659", {"start": v(154.98, 97.8) * mm, "mid": v(154.1, 99.92) * mm, "end": v(151.98, 100.8) * mm});
            skArc(sketch, "E2660", {"start": v(438.33, -387.42) * mm, "mid": v(436.21, -388.3) * mm, "end": v(435.33, -390.42) * mm});
            skArc(sketch, "E2661", {"start": v(435.33, -390.42) * mm, "mid": v(436.21, -392.54) * mm, "end": v(438.33, -393.42) * mm});
            skArc(sketch, "E2662", {"start": v(438.33, -393.42) * mm, "mid": v(440.46, -392.54) * mm, "end": v(441.33, -390.42) * mm});
            skArc(sketch, "E2663", {"start": v(441.33, -390.42) * mm, "mid": v(440.46, -388.3) * mm, "end": v(438.33, -387.42) * mm});
            skArc(sketch, "E2664", {"start": v(438.33, 396.54) * mm, "mid": v(436.21, 395.66) * mm, "end": v(435.33, 393.54) * mm});
            skArc(sketch, "E2665", {"start": v(435.33, 393.54) * mm, "mid": v(436.21, 391.42) * mm, "end": v(438.33, 390.54) * mm});
            skArc(sketch, "E2666", {"start": v(438.33, 390.54) * mm, "mid": v(440.46, 391.42) * mm, "end": v(441.33, 393.54) * mm});
            skArc(sketch, "E2667", {"start": v(441.33, 393.54) * mm, "mid": v(440.46, 395.66) * mm, "end": v(438.33, 396.54) * mm});
            skArc(sketch, "E2668", {"start": v(147.28, 917.61) * mm, "mid": v(145.16, 916.74) * mm, "end": v(144.28, 914.61) * mm});
            skArc(sketch, "E2669", {"start": v(144.28, 914.61) * mm, "mid": v(145.16, 912.5) * mm, "end": v(147.28, 911.61) * mm});
            skArc(sketch, "E2670", {"start": v(147.28, 911.61) * mm, "mid": v(149.4, 912.5) * mm, "end": v(150.28, 914.61) * mm});
            skArc(sketch, "E2671", {"start": v(150.28, 914.61) * mm, "mid": v(149.4, 916.74) * mm, "end": v(147.28, 917.61) * mm});
            skArc(sketch, "E2672", {"start": v(414.86, 955.17) * mm, "mid": v(412.74, 954.3) * mm, "end": v(411.86, 952.17) * mm});
            skArc(sketch, "E2673", {"start": v(411.86, 952.17) * mm, "mid": v(412.74, 950.05) * mm, "end": v(414.86, 949.17) * mm});
            skArc(sketch, "E2674", {"start": v(414.86, 949.17) * mm, "mid": v(416.98, 950.05) * mm, "end": v(417.86, 952.17) * mm});
            skArc(sketch, "E2675", {"start": v(417.86, 952.17) * mm, "mid": v(416.98, 954.3) * mm, "end": v(414.86, 955.17) * mm});
            skSolve(sketch);
        }
        {
            var Q0;
            Q0=makeQuery(id+"F0.imprint","IMPRINT",FACE,{"disambiguationData":[TD([[makeQuery(id+"F0.imprint","IMPRINT",EDGE,{"derivedFrom":sQuery(id+"F0.wireOp",EDGE,"E4")}),1.0]])]});
            var Q1;
            {var subQ0=sQuery(id+"F0.wireOp",EDGE,"E1802");Q1=makeQuery(id+"F0.imprint","IMPRINT",FACE,{"disambiguationData":[TD([[makeQuery(id+"F0.imprint","IMPRINT",EDGE,{"derivedFrom":subQ0}),-1.0]])]});}
            var Q2;
            Q2=makeQuery(id+"F0.imprint","IMPRINT",FACE,{"disambiguationData":[TD([[makeQuery(id+"F0.imprint","IMPRINT",EDGE,{"derivedFrom":sQuery(id+"F0.wireOp",EDGE,"E1545")}),-1.0]])]});
            var Q3;
            Q3=makeQuery(id+"F0.imprint","IMPRINT",FACE,{"disambiguationData":[TD([[makeQuery(id+"F0.imprint","IMPRINT",EDGE,{"derivedFrom":sQuery(id+"F0.wireOp",EDGE,"E1289")}),-1.0]])]});
            extrude(context, id + "F1", {"entities" : qUnion([Q0, Q1, Q2, Q3]), "depth" : 18 * mm});
        }
    });
